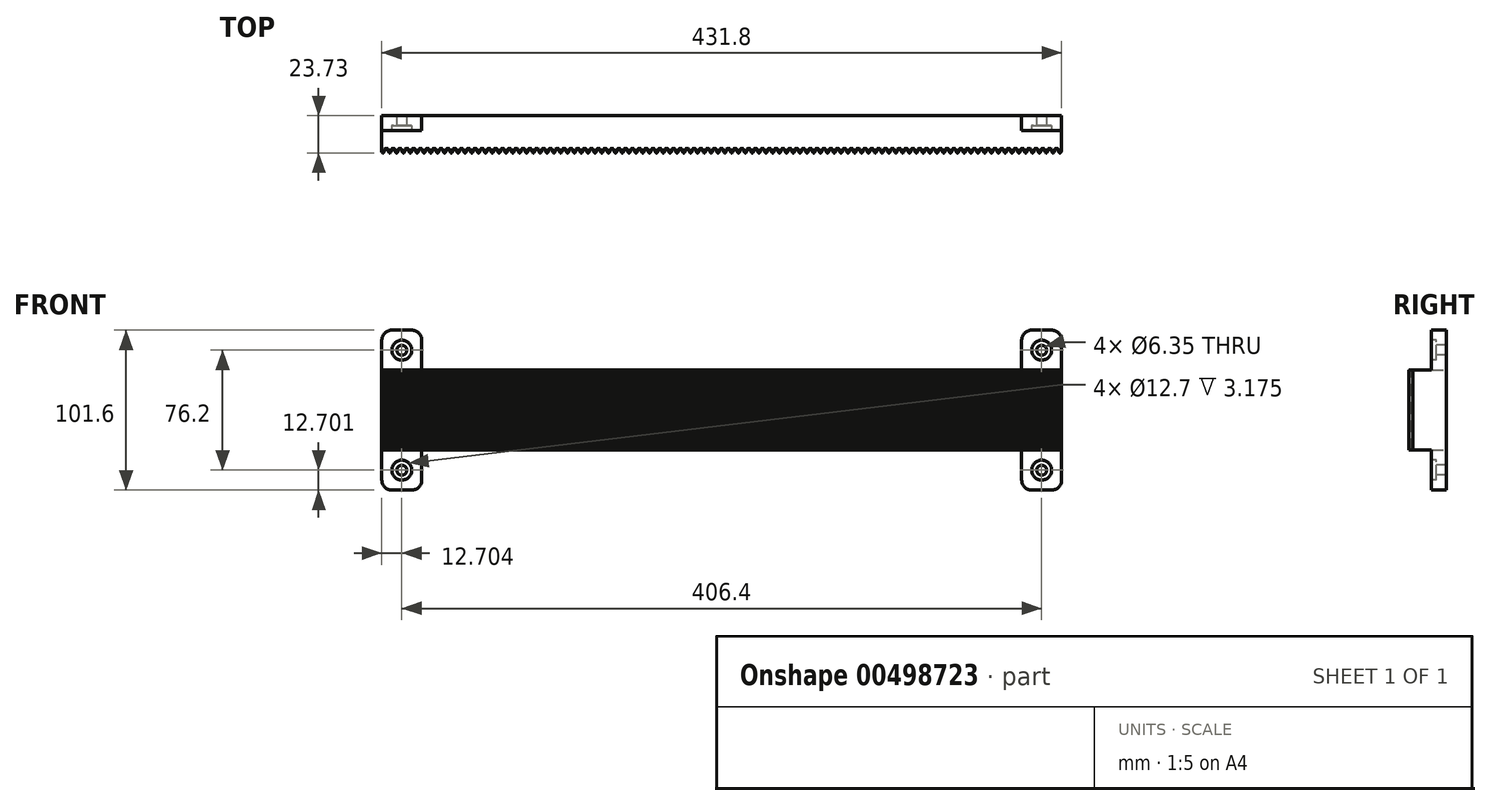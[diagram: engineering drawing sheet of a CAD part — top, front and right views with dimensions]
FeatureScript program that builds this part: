
annotation { "Feature Type Name" : "Feature", "Feature Type Description" : "" }
export const myFeature = defineFeature(function(context is Context, id is Id, definition is map)
    precondition{}
    {
        {
            var Q0;
            Q0=qCreatedBy(makeId("Front.planeOp"),FACE);
            var sketch = newSketch(context, id + "F0", { "sketchPlane" : qUnion([Q0])});
            skLineSegment(sketch, "E0.bottom", {"start": v(-70.87, -34.72) * mm, "end": v(360.93, -34.72) * mm});
            skLineSegment(sketch, "E0.top", {"start": v(-70.87, 16.08) * mm, "end": v(360.93, 16.08) * mm});
            skLineSegment(sketch, "E0.left", {"start": v(-70.87, -34.72) * mm, "end": v(-70.87, 16.08) * mm});
            skLineSegment(sketch, "E0.right", {"start": v(360.93, -34.72) * mm, "end": v(360.93, 16.08) * mm});
            skLineSegment(sketch, "E1", {"start": v(-70.87, 16.08) * mm, "end": v(-70.87, 35.13) * mm});
            skLineSegment(sketch, "E2", {"start": v(-64.52, 41.48) * mm, "end": v(-51.82, 41.48) * mm});
            skLineSegment(sketch, "E3", {"start": v(-45.47, 35.13) * mm, "end": v(-45.47, 16.08) * mm});
            skLineSegment(sketch, "E4", {"start": v(-70.87, -34.72) * mm, "end": v(-70.87, -53.77) * mm});
            skLineSegment(sketch, "E5", {"start": v(-64.52, -60.12) * mm, "end": v(-51.82, -60.12) * mm});
            skLineSegment(sketch, "E6", {"start": v(-45.47, -53.77) * mm, "end": v(-45.47, -34.72) * mm});
            skLineSegment(sketch, "E7", {"start": v(360.93, 16.08) * mm, "end": v(360.93, 35.13) * mm});
            skLineSegment(sketch, "E8", {"start": v(354.58, 41.48) * mm, "end": v(341.88, 41.48) * mm});
            skLineSegment(sketch, "E9", {"start": v(335.53, 35.13) * mm, "end": v(335.53, 16.08) * mm});
            skLineSegment(sketch, "E10", {"start": v(360.93, -34.72) * mm, "end": v(360.93, -53.77) * mm});
            skLineSegment(sketch, "E11", {"start": v(354.58, -60.12) * mm, "end": v(341.88, -60.12) * mm});
            skLineSegment(sketch, "E12", {"start": v(335.53, -53.77) * mm, "end": v(335.53, -34.72) * mm});
            skPoint(sketch, "E13.visualSharp", {"position": v(-70.87, 41.48) * mm});
            skArc(sketch, "E13.filletArc", {"start": v(-64.52, 41.48) * mm, "mid": v(-69, 39.62) * mm, "end": v(-70.87, 35.13) * mm});
            skPoint(sketch, "E14.visualSharp", {"position": v(-45.47, 41.48) * mm});
            skArc(sketch, "E14.filletArc", {"start": v(-45.47, 35.13) * mm, "mid": v(-47.33, 39.62) * mm, "end": v(-51.82, 41.48) * mm});
            skPoint(sketch, "E15.visualSharp", {"position": v(-45.47, -60.12) * mm});
            skArc(sketch, "E15.filletArc", {"start": v(-51.82, -60.12) * mm, "mid": v(-47.33, -58.26) * mm, "end": v(-45.47, -53.77) * mm});
            skPoint(sketch, "E16.visualSharp", {"position": v(360.93, -60.12) * mm});
            skArc(sketch, "E16.filletArc", {"start": v(354.58, -60.12) * mm, "mid": v(359.07, -58.26) * mm, "end": v(360.93, -53.77) * mm});
            skPoint(sketch, "E17.visualSharp", {"position": v(360.93, 41.48) * mm});
            skArc(sketch, "E17.filletArc", {"start": v(360.93, 35.13) * mm, "mid": v(359.07, 39.62) * mm, "end": v(354.58, 41.48) * mm});
            skPoint(sketch, "E18.visualSharp", {"position": v(335.53, 41.48) * mm});
            skArc(sketch, "E18.filletArc", {"start": v(341.88, 41.48) * mm, "mid": v(337.4, 39.62) * mm, "end": v(335.53, 35.13) * mm});
            skPoint(sketch, "E19.visualSharp", {"position": v(335.53, -60.12) * mm});
            skArc(sketch, "E19.filletArc", {"start": v(335.53, -53.77) * mm, "mid": v(337.4, -58.26) * mm, "end": v(341.88, -60.12) * mm});
            skPoint(sketch, "E20.visualSharp", {"position": v(-70.87, -60.12) * mm});
            skArc(sketch, "E20.filletArc", {"start": v(-70.87, -53.77) * mm, "mid": v(-69, -58.26) * mm, "end": v(-64.52, -60.12) * mm});
            skSolve(sketch);
        }
        {
            var Q0;
            {var subQ1=sQuery(id+"F0.wireOp",EDGE,"E4");Q0=makeQuery(id+"F0.imprint","IMPRINT",FACE,{"disambiguationData":[TD([[makeQuery(id+"F0.imprint","IMPRINT",EDGE,{"derivedFrom":subQ1}),1.0]])]});}
            var Q1;
            {var subQ1=sQuery(id+"F0.wireOp",EDGE,"E10");Q1=makeQuery(id+"F0.imprint","IMPRINT",FACE,{"disambiguationData":[TD([[makeQuery(id+"F0.imprint","IMPRINT",EDGE,{"derivedFrom":subQ1}),-1.0]])]});}
            var Q2;
            {var subQ1=sQuery(id+"F0.wireOp",EDGE,"E1");Q2=makeQuery(id+"F0.imprint","IMPRINT",FACE,{"disambiguationData":[TD([[makeQuery(id+"F0.imprint","IMPRINT",EDGE,{"derivedFrom":subQ1}),-1.0]])]});}
            var Q3;
            {var subQ1=sQuery(id+"F0.wireOp",EDGE,"E7");Q3=makeQuery(id+"F0.imprint","IMPRINT",FACE,{"disambiguationData":[TD([[makeQuery(id+"F0.imprint","IMPRINT",EDGE,{"derivedFrom":subQ1}),1.0]])]});}
            var Q4;
            {var subQ0=sQuery(id+"F0.wireOp",EDGE,"E0.left");Q4=makeQuery(id+"F0.imprint","IMPRINT",FACE,{"disambiguationData":[TD([[makeQuery(id+"F0.imprint","IMPRINT",EDGE,{"derivedFrom":subQ0}),-1.0]])]});}
            extrude(context, id + "F1", {"entities" : qUnion([Q0, Q1, Q2, Q3, Q4]), "depth" : 9.52 * mm});
        }
        {
            var Q0;
            Q0=makeQuery(id+"F1.opExtrude","CAP_FACE",FACE,{"disambiguationData":[OSD([sQuery(id+"F0.wireOp",EDGE,"E0.bottom"),sQuery(id+"F0.wireOp",EDGE,"E0.top"),sQuery(id+"F0.wireOp",EDGE,"E0.left"),sQuery(id+"F0.wireOp",EDGE,"E0.right"),sQuery(id+"F0.wireOp",EDGE,"E1"),sQuery(id+"F0.wireOp",EDGE,"E2"),sQuery(id+"F0.wireOp",EDGE,"E3"),sQuery(id+"F0.wireOp",EDGE,"E4"),sQuery(id+"F0.wireOp",EDGE,"E5"),sQuery(id+"F0.wireOp",EDGE,"E6"),sQuery(id+"F0.wireOp",EDGE,"E7"),sQuery(id+"F0.wireOp",EDGE,"E8"),sQuery(id+"F0.wireOp",EDGE,"E9"),sQuery(id+"F0.wireOp",EDGE,"E10"),sQuery(id+"F0.wireOp",EDGE,"E11"),sQuery(id+"F0.wireOp",EDGE,"E12"),sQuery(id+"F0.wireOp",EDGE,"E13.filletArc"),sQuery(id+"F0.wireOp",EDGE,"E14.filletArc"),sQuery(id+"F0.wireOp",EDGE,"E15.filletArc"),sQuery(id+"F0.wireOp",EDGE,"E16.filletArc"),sQuery(id+"F0.wireOp",EDGE,"E17.filletArc"),sQuery(id+"F0.wireOp",EDGE,"E18.filletArc"),sQuery(id+"F0.wireOp",EDGE,"E19.filletArc"),sQuery(id+"F0.wireOp",EDGE,"E20.filletArc")])],"isStart":false});
            var sketch = newSketch(context, id + "F2", { "sketchPlane" : qUnion([Q0])});
            skLineSegment(sketch, "E21", {"start": v(-45.47, -34.72) * mm, "end": v(-70.87, -34.72) * mm});
            skLineSegment(sketch, "E22", {"start": v(-45.47, 16.08) * mm, "end": v(-70.87, 16.08) * mm});
            skLineSegment(sketch, "E23", {"start": v(335.53, 16.08) * mm, "end": v(360.93, 16.08) * mm});
            skLineSegment(sketch, "E24", {"start": v(335.53, -34.72) * mm, "end": v(360.93, -34.72) * mm});
            skCircle(sketch, "E25", {"center": v(-58.17, 28.78) * mm, "radius": 6.35 * mm});
            skCircle(sketch, "E26", {"center": v(-58.17, -47.42) * mm, "radius": 6.35 * mm});
            skCircle(sketch, "E27", {"center": v(348.23, 28.78) * mm, "radius": 6.35 * mm});
            skCircle(sketch, "E28", {"center": v(348.23, -47.42) * mm, "radius": 6.35 * mm});
            skSolve(sketch);
        }
        {
            var Q0;
            Q0=sQuery(id+"F2.wireOp",VERTEX,"E25.center");
            var Q1;
            Q1=sQuery(id+"F2.wireOp",VERTEX,"E26.center");
            var Q2;
            Q2=sQuery(id+"F2.wireOp",VERTEX,"E27.center");
            var Q3;
            Q3=sQuery(id+"F2.wireOp",VERTEX,"E28.center");
            var Q4;
            Q4=makeQuery(id+"F1.opExtrude","SWEPT_BODY",BODY,{"disambiguationData":[OSD([sQuery(id+"F0.wireOp",EDGE,"E0.bottom"),sQuery(id+"F0.wireOp",EDGE,"E0.top"),sQuery(id+"F0.wireOp",EDGE,"E0.left"),sQuery(id+"F0.wireOp",EDGE,"E0.right"),sQuery(id+"F0.wireOp",EDGE,"E1"),sQuery(id+"F0.wireOp",EDGE,"E2"),sQuery(id+"F0.wireOp",EDGE,"E3"),sQuery(id+"F0.wireOp",EDGE,"E4"),sQuery(id+"F0.wireOp",EDGE,"E5"),sQuery(id+"F0.wireOp",EDGE,"E6"),sQuery(id+"F0.wireOp",EDGE,"E7"),sQuery(id+"F0.wireOp",EDGE,"E8"),sQuery(id+"F0.wireOp",EDGE,"E9"),sQuery(id+"F0.wireOp",EDGE,"E10"),sQuery(id+"F0.wireOp",EDGE,"E11"),sQuery(id+"F0.wireOp",EDGE,"E12"),sQuery(id+"F0.wireOp",EDGE,"E13.filletArc"),sQuery(id+"F0.wireOp",EDGE,"E14.filletArc"),sQuery(id+"F0.wireOp",EDGE,"E15.filletArc"),sQuery(id+"F0.wireOp",EDGE,"E16.filletArc"),sQuery(id+"F0.wireOp",EDGE,"E17.filletArc"),sQuery(id+"F0.wireOp",EDGE,"E18.filletArc"),sQuery(id+"F0.wireOp",EDGE,"E19.filletArc"),sQuery(id+"F0.wireOp",EDGE,"E20.filletArc")])]});
            hole(context, id + "F3", {"style" : HoleStyle.C_BORE, "endStyle" : HoleEndStyle.BLIND, "holeDiameter" : 6.35 * mm, "cBoreDiameter" : 12.7 * mm, "cBoreDepth" : 3.17 * mm, "holeDepth" : 76.2 * mm, "tappedDepth" : 12.7 * mm, "tapClearance" : 3, "startFromSketch" : true, "locations" : qUnion([Q0, Q1, Q2, Q3]), "scope" : qUnion([Q4])});
        }
        {
            var Q0;
            {var subQ3=sQuery(id+"F2.wireOp",EDGE,"E21");Q0=makeQuery(id+"F2.imprint","IMPRINT",FACE,{"disambiguationData":[TD([[makeQuery(id+"F2.imprint","IMPRINT",EDGE,{"derivedFrom":subQ3}),-1.0]])]});}
            extrude(context, id + "F4", {"entities" : qUnion([Q0]), "operationType" : NewBodyOperationType.ADD, "depth" : 11.2 * mm});
        }
        {
            var Q0;
            {var subQ0=sQuery(id+"F0.wireOp",EDGE,"E0.top");Q0=makeQuery(id+"F4.boolean.opBoolean","MERGE",FACE,{"derivedFrom":[makeQuery(id+"F1.opExtrude","SWEPT_FACE",FACE,{"disambiguationData":[OSD([subQ0])]}),makeQuery(id+"F4.opExtrude","SWEPT_FACE",FACE,{"disambiguationData":[OSD([subQ0,sQuery(id+"F2.wireOp",EDGE,"E22"),sQuery(id+"F2.wireOp",EDGE,"E23")])]})]});}
            var sketch = newSketch(context, id + "F5", { "sketchPlane" : qUnion([Q0])});
            skArc(sketch, "E29.trimOffspring", {"start": v(358.88, -22.45) * mm, "mid": v(359.12, -22.98) * mm, "end": v(359.4, -23.48) * mm});
            skLineSegment(sketch, "E30", {"start": v(359.83, -23.72) * mm, "end": v(359.84, -23.73) * mm});
            skLineSegment(sketch, "E31", {"start": v(358.77, -21.8) * mm, "end": v(358.78, -21.55) * mm});
            skLineSegment(sketch, "E32.MirrorCS", {"start": v(359.84, -23.73) * mm, "end": v(359.83, -23.72) * mm});
            skArc(sketch, "E33.MirrorCS", {"start": v(360.8, -22.45) * mm, "mid": v(360.56, -22.98) * mm, "end": v(360.28, -23.48) * mm});
            skLineSegment(sketch, "E34.MirrorCS", {"start": v(360.9, -21.8) * mm, "end": v(360.9, -21.55) * mm});
            skPoint(sketch, "E35.orphan", {"position": v(358.82, -20.63) * mm});
            skPoint(sketch, "E36.visualSharp", {"position": v(360.12, -23.73) * mm});
            skArc(sketch, "E36.filletArc", {"start": v(359.84, -23.73) * mm, "mid": v(360.1, -23.66) * mm, "end": v(360.28, -23.48) * mm});
            skPoint(sketch, "E37.visualSharp", {"position": v(359.55, -23.72) * mm});
            skArc(sketch, "E37.filletArc", {"start": v(359.4, -23.48) * mm, "mid": v(359.58, -23.66) * mm, "end": v(359.83, -23.72) * mm});
            skPoint(sketch, "E38.visualSharp", {"position": v(358.76, -22.11) * mm});
            skArc(sketch, "E38.filletArc", {"start": v(358.77, -21.8) * mm, "mid": v(358.8, -22.13) * mm, "end": v(358.88, -22.45) * mm});
            skPoint(sketch, "E39.visualSharp", {"position": v(360.92, -22.11) * mm});
            skArc(sketch, "E39.filletArc", {"start": v(360.8, -22.45) * mm, "mid": v(360.88, -22.13) * mm, "end": v(360.9, -21.8) * mm});
            skPoint(sketch, "E40.orphan", {"position": v(359.93, -23.73) * mm});
            skArc(sketch, "E41.filletArc", {"start": v(358.78, -21.55) * mm, "mid": v(358.57, -20.97) * mm, "end": v(358, -20.73) * mm});
            skArc(sketch, "E42.filletArc", {"start": v(360.93, -21.26) * mm, "mid": v(360.9, -21.4) * mm, "end": v(360.9, -21.55) * mm});
            skArc(sketch, "E43.1.0.0", {"start": v(354.54, -22.45) * mm, "mid": v(354.78, -22.98) * mm, "end": v(355.06, -23.48) * mm});
            skPoint(sketch, "E43.1.0.1", {"position": v(354.48, -20.63) * mm});
            skLineSegment(sketch, "E43.1.0.2", {"start": v(354.43, -21.8) * mm, "end": v(354.44, -21.55) * mm});
            skPoint(sketch, "E43.1.0.3", {"position": v(356.57, -22.11) * mm});
            skPoint(sketch, "E43.1.0.4", {"position": v(355.78, -23.73) * mm});
            skArc(sketch, "E43.1.0.5", {"start": v(356.45, -22.45) * mm, "mid": v(356.21, -22.98) * mm, "end": v(355.94, -23.48) * mm});
            skPoint(sketch, "E43.1.0.6", {"position": v(354.42, -22.11) * mm});
            skLineSegment(sketch, "E43.1.0.7", {"start": v(356.56, -21.8) * mm, "end": v(356.55, -21.55) * mm});
            skPoint(sketch, "E43.1.0.8", {"position": v(355.21, -23.72) * mm});
            skArc(sketch, "E43.1.0.9", {"start": v(354.44, -21.55) * mm, "mid": v(354.22, -20.97) * mm, "end": v(353.65, -20.73) * mm});
            skLineSegment(sketch, "E43.1.0.10", {"start": v(357.34, -20.73) * mm, "end": v(356.6, -20.73) * mm});
            skArc(sketch, "E43.1.0.11", {"start": v(356.45, -22.45) * mm, "mid": v(356.54, -22.13) * mm, "end": v(356.56, -21.8) * mm});
            skArc(sketch, "E43.1.0.12", {"start": v(354.43, -21.8) * mm, "mid": v(354.45, -22.13) * mm, "end": v(354.54, -22.45) * mm});
            skPoint(sketch, "E43.1.0.13", {"position": v(355.59, -23.73) * mm});
            skArc(sketch, "E43.1.0.14", {"start": v(355.06, -23.48) * mm, "mid": v(355.24, -23.66) * mm, "end": v(355.48, -23.72) * mm});
            skArc(sketch, "E43.1.0.15", {"start": v(357.34, -20.73) * mm, "mid": v(356.77, -20.97) * mm, "end": v(356.55, -21.55) * mm});
            skArc(sketch, "E43.1.0.16", {"start": v(355.5, -23.73) * mm, "mid": v(355.75, -23.66) * mm, "end": v(355.94, -23.48) * mm});
            skLineSegment(sketch, "E43.1.0.17", {"start": v(355.5, -23.73) * mm, "end": v(355.48, -23.72) * mm});
            skLineSegment(sketch, "E43.1.0.18", {"start": v(355.48, -23.72) * mm, "end": v(355.5, -23.73) * mm});
            skArc(sketch, "E43.2.0.0", {"start": v(350.2, -22.45) * mm, "mid": v(350.43, -22.98) * mm, "end": v(350.71, -23.48) * mm});
            skPoint(sketch, "E43.2.0.1", {"position": v(350.14, -20.63) * mm});
            skLineSegment(sketch, "E43.2.0.2", {"start": v(350.09, -21.8) * mm, "end": v(350.1, -21.55) * mm});
            skPoint(sketch, "E43.2.0.3", {"position": v(352.23, -22.11) * mm});
            skPoint(sketch, "E43.2.0.4", {"position": v(351.43, -23.73) * mm});
            skArc(sketch, "E43.2.0.5", {"start": v(352.1, -22.45) * mm, "mid": v(351.87, -22.98) * mm, "end": v(351.6, -23.48) * mm});
            skPoint(sketch, "E43.2.0.6", {"position": v(350.07, -22.11) * mm});
            skLineSegment(sketch, "E43.2.0.7", {"start": v(352.22, -21.8) * mm, "end": v(352.2, -21.55) * mm});
            skPoint(sketch, "E43.2.0.8", {"position": v(350.87, -23.72) * mm});
            skArc(sketch, "E43.2.0.9", {"start": v(350.1, -21.55) * mm, "mid": v(349.88, -20.97) * mm, "end": v(349.31, -20.73) * mm});
            skLineSegment(sketch, "E43.2.0.10", {"start": v(353, -20.73) * mm, "end": v(352.25, -20.73) * mm});
            skArc(sketch, "E43.2.0.11", {"start": v(352.1, -22.45) * mm, "mid": v(352.2, -22.13) * mm, "end": v(352.22, -21.8) * mm});
            skArc(sketch, "E43.2.0.12", {"start": v(350.09, -21.8) * mm, "mid": v(350.1, -22.13) * mm, "end": v(350.2, -22.45) * mm});
            skPoint(sketch, "E43.2.0.13", {"position": v(351.24, -23.73) * mm});
            skArc(sketch, "E43.2.0.14", {"start": v(350.71, -23.48) * mm, "mid": v(350.9, -23.66) * mm, "end": v(351.14, -23.72) * mm});
            skArc(sketch, "E43.2.0.15", {"start": v(353, -20.73) * mm, "mid": v(352.42, -20.97) * mm, "end": v(352.2, -21.55) * mm});
            skArc(sketch, "E43.2.0.16", {"start": v(351.15, -23.73) * mm, "mid": v(351.4, -23.66) * mm, "end": v(351.6, -23.48) * mm});
            skLineSegment(sketch, "E43.2.0.17", {"start": v(351.15, -23.73) * mm, "end": v(351.14, -23.72) * mm});
            skLineSegment(sketch, "E43.2.0.18", {"start": v(351.14, -23.72) * mm, "end": v(351.15, -23.73) * mm});
            skArc(sketch, "E43.3.0.0", {"start": v(345.85, -22.45) * mm, "mid": v(346.1, -22.98) * mm, "end": v(346.37, -23.48) * mm});
            skPoint(sketch, "E43.3.0.1", {"position": v(345.8, -20.63) * mm});
            skLineSegment(sketch, "E43.3.0.2", {"start": v(345.74, -21.8) * mm, "end": v(345.75, -21.55) * mm});
            skPoint(sketch, "E43.3.0.3", {"position": v(347.89, -22.11) * mm});
            skPoint(sketch, "E43.3.0.4", {"position": v(347.1, -23.73) * mm});
            skArc(sketch, "E43.3.0.5", {"start": v(347.76, -22.45) * mm, "mid": v(347.53, -22.98) * mm, "end": v(347.25, -23.48) * mm});
            skPoint(sketch, "E43.3.0.6", {"position": v(345.73, -22.11) * mm});
            skLineSegment(sketch, "E43.3.0.7", {"start": v(347.87, -21.8) * mm, "end": v(347.86, -21.55) * mm});
            skPoint(sketch, "E43.3.0.8", {"position": v(346.52, -23.72) * mm});
            skArc(sketch, "E43.3.0.9", {"start": v(345.75, -21.55) * mm, "mid": v(345.54, -20.97) * mm, "end": v(344.97, -20.73) * mm});
            skLineSegment(sketch, "E43.3.0.10", {"start": v(348.65, -20.73) * mm, "end": v(347.9, -20.73) * mm});
            skArc(sketch, "E43.3.0.11", {"start": v(347.76, -22.45) * mm, "mid": v(347.85, -22.13) * mm, "end": v(347.87, -21.8) * mm});
            skArc(sketch, "E43.3.0.12", {"start": v(345.74, -21.8) * mm, "mid": v(345.76, -22.13) * mm, "end": v(345.85, -22.45) * mm});
            skPoint(sketch, "E43.3.0.13", {"position": v(346.9, -23.73) * mm});
            skArc(sketch, "E43.3.0.14", {"start": v(346.37, -23.48) * mm, "mid": v(346.55, -23.66) * mm, "end": v(346.8, -23.72) * mm});
            skArc(sketch, "E43.3.0.15", {"start": v(348.65, -20.73) * mm, "mid": v(348.08, -20.97) * mm, "end": v(347.86, -21.55) * mm});
            skArc(sketch, "E43.3.0.16", {"start": v(346.8, -23.73) * mm, "mid": v(347.06, -23.66) * mm, "end": v(347.25, -23.48) * mm});
            skLineSegment(sketch, "E43.3.0.17", {"start": v(346.8, -23.73) * mm, "end": v(346.8, -23.72) * mm});
            skLineSegment(sketch, "E43.3.0.18", {"start": v(346.8, -23.72) * mm, "end": v(346.8, -23.73) * mm});
            skArc(sketch, "E43.4.0.0", {"start": v(341.51, -22.45) * mm, "mid": v(341.75, -22.98) * mm, "end": v(342.03, -23.48) * mm});
            skPoint(sketch, "E43.4.0.1", {"position": v(341.45, -20.63) * mm});
            skLineSegment(sketch, "E43.4.0.2", {"start": v(341.4, -21.8) * mm, "end": v(341.41, -21.55) * mm});
            skPoint(sketch, "E43.4.0.3", {"position": v(343.54, -22.11) * mm});
            skPoint(sketch, "E43.4.0.4", {"position": v(342.75, -23.73) * mm});
            skArc(sketch, "E43.4.0.5", {"start": v(343.42, -22.45) * mm, "mid": v(343.18, -22.98) * mm, "end": v(342.9, -23.48) * mm});
            skPoint(sketch, "E43.4.0.6", {"position": v(341.39, -22.11) * mm});
            skLineSegment(sketch, "E43.4.0.7", {"start": v(343.53, -21.8) * mm, "end": v(343.52, -21.55) * mm});
            skPoint(sketch, "E43.4.0.8", {"position": v(342.18, -23.72) * mm});
            skArc(sketch, "E43.4.0.9", {"start": v(341.41, -21.55) * mm, "mid": v(341.2, -20.97) * mm, "end": v(340.62, -20.73) * mm});
            skLineSegment(sketch, "E43.4.0.10", {"start": v(344.3, -20.73) * mm, "end": v(343.56, -20.73) * mm});
            skArc(sketch, "E43.4.0.11", {"start": v(343.42, -22.45) * mm, "mid": v(343.51, -22.13) * mm, "end": v(343.53, -21.8) * mm});
            skArc(sketch, "E43.4.0.12", {"start": v(341.4, -21.8) * mm, "mid": v(341.42, -22.13) * mm, "end": v(341.51, -22.45) * mm});
            skPoint(sketch, "E43.4.0.13", {"position": v(342.56, -23.73) * mm});
            skArc(sketch, "E43.4.0.14", {"start": v(342.03, -23.48) * mm, "mid": v(342.2, -23.66) * mm, "end": v(342.45, -23.72) * mm});
            skArc(sketch, "E43.4.0.15", {"start": v(344.3, -20.73) * mm, "mid": v(343.74, -20.97) * mm, "end": v(343.52, -21.55) * mm});
            skArc(sketch, "E43.4.0.16", {"start": v(342.47, -23.73) * mm, "mid": v(342.72, -23.66) * mm, "end": v(342.9, -23.48) * mm});
            skLineSegment(sketch, "E43.4.0.17", {"start": v(342.47, -23.73) * mm, "end": v(342.45, -23.72) * mm});
            skLineSegment(sketch, "E43.4.0.18", {"start": v(342.45, -23.72) * mm, "end": v(342.47, -23.73) * mm});
            skArc(sketch, "E43.5.0.0", {"start": v(337.17, -22.45) * mm, "mid": v(337.4, -22.98) * mm, "end": v(337.68, -23.48) * mm});
            skPoint(sketch, "E43.5.0.1", {"position": v(337.1, -20.63) * mm});
            skLineSegment(sketch, "E43.5.0.2", {"start": v(337.06, -21.8) * mm, "end": v(337.07, -21.55) * mm});
            skPoint(sketch, "E43.5.0.3", {"position": v(339.2, -22.11) * mm});
            skPoint(sketch, "E43.5.0.4", {"position": v(338.4, -23.73) * mm});
            skArc(sketch, "E43.5.0.5", {"start": v(339.08, -22.45) * mm, "mid": v(338.84, -22.98) * mm, "end": v(338.56, -23.48) * mm});
            skPoint(sketch, "E43.5.0.6", {"position": v(337.04, -22.11) * mm});
            skLineSegment(sketch, "E43.5.0.7", {"start": v(339.19, -21.8) * mm, "end": v(339.18, -21.55) * mm});
            skPoint(sketch, "E43.5.0.8", {"position": v(337.84, -23.72) * mm});
            skArc(sketch, "E43.5.0.9", {"start": v(337.07, -21.55) * mm, "mid": v(336.85, -20.97) * mm, "end": v(336.28, -20.73) * mm});
            skLineSegment(sketch, "E43.5.0.10", {"start": v(339.96, -20.73) * mm, "end": v(339.22, -20.73) * mm});
            skArc(sketch, "E43.5.0.11", {"start": v(339.08, -22.45) * mm, "mid": v(339.17, -22.13) * mm, "end": v(339.19, -21.8) * mm});
            skArc(sketch, "E43.5.0.12", {"start": v(337.06, -21.8) * mm, "mid": v(337.08, -22.13) * mm, "end": v(337.17, -22.45) * mm});
            skPoint(sketch, "E43.5.0.13", {"position": v(338.21, -23.73) * mm});
            skArc(sketch, "E43.5.0.14", {"start": v(337.68, -23.48) * mm, "mid": v(337.87, -23.66) * mm, "end": v(338.1, -23.72) * mm});
            skArc(sketch, "E43.5.0.15", {"start": v(339.96, -20.73) * mm, "mid": v(339.4, -20.97) * mm, "end": v(339.18, -21.55) * mm});
            skArc(sketch, "E43.5.0.16", {"start": v(338.12, -23.73) * mm, "mid": v(338.37, -23.66) * mm, "end": v(338.56, -23.48) * mm});
            skLineSegment(sketch, "E43.5.0.17", {"start": v(338.12, -23.73) * mm, "end": v(338.1, -23.72) * mm});
            skLineSegment(sketch, "E43.5.0.18", {"start": v(338.1, -23.72) * mm, "end": v(338.12, -23.73) * mm});
            skArc(sketch, "E43.6.0.0", {"start": v(332.82, -22.45) * mm, "mid": v(333.06, -22.98) * mm, "end": v(333.34, -23.48) * mm});
            skPoint(sketch, "E43.6.0.1", {"position": v(332.76, -20.63) * mm});
            skLineSegment(sketch, "E43.6.0.2", {"start": v(332.71, -21.8) * mm, "end": v(332.72, -21.55) * mm});
            skPoint(sketch, "E43.6.0.3", {"position": v(334.86, -22.11) * mm});
            skPoint(sketch, "E43.6.0.4", {"position": v(334.06, -23.73) * mm});
            skArc(sketch, "E43.6.0.5", {"start": v(334.73, -22.45) * mm, "mid": v(334.5, -22.98) * mm, "end": v(334.22, -23.48) * mm});
            skPoint(sketch, "E43.6.0.6", {"position": v(332.7, -22.11) * mm});
            skLineSegment(sketch, "E43.6.0.7", {"start": v(334.84, -21.8) * mm, "end": v(334.83, -21.55) * mm});
            skPoint(sketch, "E43.6.0.8", {"position": v(333.5, -23.72) * mm});
            skArc(sketch, "E43.6.0.9", {"start": v(332.72, -21.55) * mm, "mid": v(332.5, -20.97) * mm, "end": v(331.94, -20.73) * mm});
            skLineSegment(sketch, "E43.6.0.10", {"start": v(335.62, -20.73) * mm, "end": v(334.87, -20.73) * mm});
            skArc(sketch, "E43.6.0.11", {"start": v(334.73, -22.45) * mm, "mid": v(334.82, -22.13) * mm, "end": v(334.84, -21.8) * mm});
            skArc(sketch, "E43.6.0.12", {"start": v(332.71, -21.8) * mm, "mid": v(332.73, -22.13) * mm, "end": v(332.82, -22.45) * mm});
            skPoint(sketch, "E43.6.0.13", {"position": v(333.87, -23.73) * mm});
            skArc(sketch, "E43.6.0.14", {"start": v(333.34, -23.48) * mm, "mid": v(333.52, -23.66) * mm, "end": v(333.77, -23.72) * mm});
            skArc(sketch, "E43.6.0.15", {"start": v(335.62, -20.73) * mm, "mid": v(335.05, -20.97) * mm, "end": v(334.83, -21.55) * mm});
            skArc(sketch, "E43.6.0.16", {"start": v(333.78, -23.73) * mm, "mid": v(334.03, -23.66) * mm, "end": v(334.22, -23.48) * mm});
            skLineSegment(sketch, "E43.6.0.17", {"start": v(333.78, -23.73) * mm, "end": v(333.77, -23.72) * mm});
            skLineSegment(sketch, "E43.6.0.18", {"start": v(333.77, -23.72) * mm, "end": v(333.78, -23.73) * mm});
            skArc(sketch, "E43.7.0.0", {"start": v(328.48, -22.45) * mm, "mid": v(328.72, -22.98) * mm, "end": v(329, -23.48) * mm});
            skPoint(sketch, "E43.7.0.1", {"position": v(328.42, -20.63) * mm});
            skLineSegment(sketch, "E43.7.0.2", {"start": v(328.37, -21.8) * mm, "end": v(328.38, -21.55) * mm});
            skPoint(sketch, "E43.7.0.3", {"position": v(330.51, -22.11) * mm});
            skPoint(sketch, "E43.7.0.4", {"position": v(329.72, -23.73) * mm});
            skArc(sketch, "E43.7.0.5", {"start": v(330.39, -22.45) * mm, "mid": v(330.15, -22.98) * mm, "end": v(329.87, -23.48) * mm});
            skPoint(sketch, "E43.7.0.6", {"position": v(328.36, -22.11) * mm});
            skLineSegment(sketch, "E43.7.0.7", {"start": v(330.5, -21.8) * mm, "end": v(330.49, -21.55) * mm});
            skPoint(sketch, "E43.7.0.8", {"position": v(329.15, -23.72) * mm});
            skArc(sketch, "E43.7.0.9", {"start": v(328.38, -21.55) * mm, "mid": v(328.16, -20.97) * mm, "end": v(327.6, -20.73) * mm});
            skLineSegment(sketch, "E43.7.0.10", {"start": v(331.28, -20.73) * mm, "end": v(330.53, -20.73) * mm});
            skArc(sketch, "E43.7.0.11", {"start": v(330.39, -22.45) * mm, "mid": v(330.48, -22.13) * mm, "end": v(330.5, -21.8) * mm});
            skArc(sketch, "E43.7.0.12", {"start": v(328.37, -21.8) * mm, "mid": v(328.4, -22.13) * mm, "end": v(328.48, -22.45) * mm});
            skPoint(sketch, "E43.7.0.13", {"position": v(329.53, -23.73) * mm});
            skArc(sketch, "E43.7.0.14", {"start": v(329, -23.48) * mm, "mid": v(329.18, -23.66) * mm, "end": v(329.42, -23.72) * mm});
            skArc(sketch, "E43.7.0.15", {"start": v(331.28, -20.73) * mm, "mid": v(330.7, -20.97) * mm, "end": v(330.49, -21.55) * mm});
            skArc(sketch, "E43.7.0.16", {"start": v(329.44, -23.73) * mm, "mid": v(329.69, -23.66) * mm, "end": v(329.87, -23.48) * mm});
            skLineSegment(sketch, "E43.7.0.17", {"start": v(329.44, -23.73) * mm, "end": v(329.42, -23.72) * mm});
            skLineSegment(sketch, "E43.7.0.18", {"start": v(329.42, -23.72) * mm, "end": v(329.44, -23.73) * mm});
            skArc(sketch, "E43.8.0.0", {"start": v(324.14, -22.45) * mm, "mid": v(324.37, -22.98) * mm, "end": v(324.65, -23.48) * mm});
            skPoint(sketch, "E43.8.0.1", {"position": v(324.08, -20.63) * mm});
            skLineSegment(sketch, "E43.8.0.2", {"start": v(324.03, -21.8) * mm, "end": v(324.04, -21.55) * mm});
            skPoint(sketch, "E43.8.0.3", {"position": v(326.17, -22.11) * mm});
            skPoint(sketch, "E43.8.0.4", {"position": v(325.37, -23.73) * mm});
            skArc(sketch, "E43.8.0.5", {"start": v(326.05, -22.45) * mm, "mid": v(325.81, -22.98) * mm, "end": v(325.53, -23.48) * mm});
            skPoint(sketch, "E43.8.0.6", {"position": v(324.01, -22.11) * mm});
            skLineSegment(sketch, "E43.8.0.7", {"start": v(326.16, -21.8) * mm, "end": v(326.15, -21.55) * mm});
            skPoint(sketch, "E43.8.0.8", {"position": v(324.8, -23.72) * mm});
            skArc(sketch, "E43.8.0.9", {"start": v(324.04, -21.55) * mm, "mid": v(323.82, -20.97) * mm, "end": v(323.25, -20.73) * mm});
            skLineSegment(sketch, "E43.8.0.10", {"start": v(326.93, -20.73) * mm, "end": v(326.19, -20.73) * mm});
            skArc(sketch, "E43.8.0.11", {"start": v(326.05, -22.45) * mm, "mid": v(326.14, -22.13) * mm, "end": v(326.16, -21.8) * mm});
            skArc(sketch, "E43.8.0.12", {"start": v(324.03, -21.8) * mm, "mid": v(324.05, -22.13) * mm, "end": v(324.14, -22.45) * mm});
            skPoint(sketch, "E43.8.0.13", {"position": v(325.18, -23.73) * mm});
            skArc(sketch, "E43.8.0.14", {"start": v(324.65, -23.48) * mm, "mid": v(324.84, -23.66) * mm, "end": v(325.08, -23.72) * mm});
            skArc(sketch, "E43.8.0.15", {"start": v(326.93, -20.73) * mm, "mid": v(326.36, -20.97) * mm, "end": v(326.15, -21.55) * mm});
            skArc(sketch, "E43.8.0.16", {"start": v(325.1, -23.73) * mm, "mid": v(325.34, -23.66) * mm, "end": v(325.53, -23.48) * mm});
            skLineSegment(sketch, "E43.8.0.17", {"start": v(325.1, -23.73) * mm, "end": v(325.08, -23.72) * mm});
            skLineSegment(sketch, "E43.8.0.18", {"start": v(325.08, -23.72) * mm, "end": v(325.1, -23.73) * mm});
            skArc(sketch, "E43.9.0.0", {"start": v(319.8, -22.45) * mm, "mid": v(320.03, -22.98) * mm, "end": v(320.3, -23.48) * mm});
            skPoint(sketch, "E43.9.0.1", {"position": v(319.73, -20.63) * mm});
            skLineSegment(sketch, "E43.9.0.2", {"start": v(319.68, -21.8) * mm, "end": v(319.7, -21.55) * mm});
            skPoint(sketch, "E43.9.0.3", {"position": v(321.83, -22.11) * mm});
            skPoint(sketch, "E43.9.0.4", {"position": v(321.03, -23.73) * mm});
            skArc(sketch, "E43.9.0.5", {"start": v(321.7, -22.45) * mm, "mid": v(321.47, -22.98) * mm, "end": v(321.19, -23.48) * mm});
            skPoint(sketch, "E43.9.0.6", {"position": v(319.67, -22.11) * mm});
            skLineSegment(sketch, "E43.9.0.7", {"start": v(321.81, -21.8) * mm, "end": v(321.8, -21.55) * mm});
            skPoint(sketch, "E43.9.0.8", {"position": v(320.46, -23.72) * mm});
            skArc(sketch, "E43.9.0.9", {"start": v(319.7, -21.55) * mm, "mid": v(319.47, -20.97) * mm, "end": v(318.9, -20.73) * mm});
            skLineSegment(sketch, "E43.9.0.10", {"start": v(322.59, -20.73) * mm, "end": v(321.84, -20.73) * mm});
            skArc(sketch, "E43.9.0.11", {"start": v(321.7, -22.45) * mm, "mid": v(321.8, -22.13) * mm, "end": v(321.81, -21.8) * mm});
            skArc(sketch, "E43.9.0.12", {"start": v(319.68, -21.8) * mm, "mid": v(319.7, -22.13) * mm, "end": v(319.8, -22.45) * mm});
            skPoint(sketch, "E43.9.0.13", {"position": v(320.84, -23.73) * mm});
            skArc(sketch, "E43.9.0.14", {"start": v(320.3, -23.48) * mm, "mid": v(320.5, -23.66) * mm, "end": v(320.74, -23.72) * mm});
            skArc(sketch, "E43.9.0.15", {"start": v(322.59, -20.73) * mm, "mid": v(322.02, -20.97) * mm, "end": v(321.8, -21.55) * mm});
            skArc(sketch, "E43.9.0.16", {"start": v(320.75, -23.73) * mm, "mid": v(321, -23.66) * mm, "end": v(321.19, -23.48) * mm});
            skLineSegment(sketch, "E43.9.0.17", {"start": v(320.75, -23.73) * mm, "end": v(320.74, -23.72) * mm});
            skLineSegment(sketch, "E43.9.0.18", {"start": v(320.74, -23.72) * mm, "end": v(320.75, -23.73) * mm});
            skArc(sketch, "E43.10.0.0", {"start": v(315.45, -22.45) * mm, "mid": v(315.69, -22.98) * mm, "end": v(315.97, -23.48) * mm});
            skPoint(sketch, "E43.10.0.1", {"position": v(315.39, -20.63) * mm});
            skLineSegment(sketch, "E43.10.0.2", {"start": v(315.34, -21.8) * mm, "end": v(315.35, -21.55) * mm});
            skPoint(sketch, "E43.10.0.3", {"position": v(317.48, -22.11) * mm});
            skPoint(sketch, "E43.10.0.4", {"position": v(316.69, -23.73) * mm});
            skArc(sketch, "E43.10.0.5", {"start": v(317.36, -22.45) * mm, "mid": v(317.12, -22.98) * mm, "end": v(316.84, -23.48) * mm});
            skPoint(sketch, "E43.10.0.6", {"position": v(315.33, -22.11) * mm});
            skLineSegment(sketch, "E43.10.0.7", {"start": v(317.47, -21.8) * mm, "end": v(317.46, -21.55) * mm});
            skPoint(sketch, "E43.10.0.8", {"position": v(316.12, -23.72) * mm});
            skArc(sketch, "E43.10.0.9", {"start": v(315.35, -21.55) * mm, "mid": v(315.13, -20.97) * mm, "end": v(314.56, -20.73) * mm});
            skLineSegment(sketch, "E43.10.0.10", {"start": v(318.25, -20.73) * mm, "end": v(317.5, -20.73) * mm});
            skArc(sketch, "E43.10.0.11", {"start": v(317.36, -22.45) * mm, "mid": v(317.45, -22.13) * mm, "end": v(317.47, -21.8) * mm});
            skArc(sketch, "E43.10.0.12", {"start": v(315.34, -21.8) * mm, "mid": v(315.36, -22.13) * mm, "end": v(315.45, -22.45) * mm});
            skPoint(sketch, "E43.10.0.13", {"position": v(316.5, -23.73) * mm});
            skArc(sketch, "E43.10.0.14", {"start": v(315.97, -23.48) * mm, "mid": v(316.15, -23.66) * mm, "end": v(316.4, -23.72) * mm});
            skArc(sketch, "E43.10.0.15", {"start": v(318.25, -20.73) * mm, "mid": v(317.68, -20.97) * mm, "end": v(317.46, -21.55) * mm});
            skArc(sketch, "E43.10.0.16", {"start": v(316.4, -23.73) * mm, "mid": v(316.66, -23.66) * mm, "end": v(316.84, -23.48) * mm});
            skLineSegment(sketch, "E43.10.0.17", {"start": v(316.4, -23.73) * mm, "end": v(316.4, -23.72) * mm});
            skLineSegment(sketch, "E43.10.0.18", {"start": v(316.4, -23.72) * mm, "end": v(316.4, -23.73) * mm});
            skArc(sketch, "E43.11.0.0", {"start": v(311.1, -22.45) * mm, "mid": v(311.34, -22.98) * mm, "end": v(311.62, -23.48) * mm});
            skPoint(sketch, "E43.11.0.1", {"position": v(311.05, -20.63) * mm});
            skLineSegment(sketch, "E43.11.0.2", {"start": v(311, -21.8) * mm, "end": v(311, -21.55) * mm});
            skPoint(sketch, "E43.11.0.3", {"position": v(313.14, -22.11) * mm});
            skPoint(sketch, "E43.11.0.4", {"position": v(312.34, -23.73) * mm});
            skArc(sketch, "E43.11.0.5", {"start": v(313.02, -22.45) * mm, "mid": v(312.78, -22.98) * mm, "end": v(312.5, -23.48) * mm});
            skPoint(sketch, "E43.11.0.6", {"position": v(310.98, -22.11) * mm});
            skLineSegment(sketch, "E43.11.0.7", {"start": v(313.13, -21.8) * mm, "end": v(313.12, -21.55) * mm});
            skPoint(sketch, "E43.11.0.8", {"position": v(311.78, -23.72) * mm});
            skArc(sketch, "E43.11.0.9", {"start": v(311, -21.55) * mm, "mid": v(310.79, -20.97) * mm, "end": v(310.22, -20.73) * mm});
            skLineSegment(sketch, "E43.11.0.10", {"start": v(313.9, -20.73) * mm, "end": v(313.16, -20.73) * mm});
            skArc(sketch, "E43.11.0.11", {"start": v(313.02, -22.45) * mm, "mid": v(313.1, -22.13) * mm, "end": v(313.13, -21.8) * mm});
            skArc(sketch, "E43.11.0.12", {"start": v(311, -21.8) * mm, "mid": v(311.02, -22.13) * mm, "end": v(311.1, -22.45) * mm});
            skPoint(sketch, "E43.11.0.13", {"position": v(312.15, -23.73) * mm});
            skArc(sketch, "E43.11.0.14", {"start": v(311.62, -23.48) * mm, "mid": v(311.8, -23.66) * mm, "end": v(312.05, -23.72) * mm});
            skArc(sketch, "E43.11.0.15", {"start": v(313.9, -20.73) * mm, "mid": v(313.33, -20.97) * mm, "end": v(313.12, -21.55) * mm});
            skArc(sketch, "E43.11.0.16", {"start": v(312.06, -23.73) * mm, "mid": v(312.31, -23.66) * mm, "end": v(312.5, -23.48) * mm});
            skLineSegment(sketch, "E43.11.0.17", {"start": v(312.06, -23.73) * mm, "end": v(312.05, -23.72) * mm});
            skLineSegment(sketch, "E43.11.0.18", {"start": v(312.05, -23.72) * mm, "end": v(312.06, -23.73) * mm});
            skArc(sketch, "E43.12.0.0", {"start": v(306.76, -22.45) * mm, "mid": v(307, -22.98) * mm, "end": v(307.28, -23.48) * mm});
            skPoint(sketch, "E43.12.0.1", {"position": v(306.7, -20.63) * mm});
            skLineSegment(sketch, "E43.12.0.2", {"start": v(306.65, -21.8) * mm, "end": v(306.66, -21.55) * mm});
            skPoint(sketch, "E43.12.0.3", {"position": v(308.8, -22.11) * mm});
            skPoint(sketch, "E43.12.0.4", {"position": v(308, -23.73) * mm});
            skArc(sketch, "E43.12.0.5", {"start": v(308.67, -22.45) * mm, "mid": v(308.44, -22.98) * mm, "end": v(308.16, -23.48) * mm});
            skPoint(sketch, "E43.12.0.6", {"position": v(306.64, -22.11) * mm});
            skLineSegment(sketch, "E43.12.0.7", {"start": v(308.78, -21.8) * mm, "end": v(308.77, -21.55) * mm});
            skPoint(sketch, "E43.12.0.8", {"position": v(307.43, -23.72) * mm});
            skArc(sketch, "E43.12.0.9", {"start": v(306.66, -21.55) * mm, "mid": v(306.44, -20.97) * mm, "end": v(305.88, -20.73) * mm});
            skLineSegment(sketch, "E43.12.0.10", {"start": v(309.56, -20.73) * mm, "end": v(308.81, -20.73) * mm});
            skArc(sketch, "E43.12.0.11", {"start": v(308.67, -22.45) * mm, "mid": v(308.76, -22.13) * mm, "end": v(308.78, -21.8) * mm});
            skArc(sketch, "E43.12.0.12", {"start": v(306.65, -21.8) * mm, "mid": v(306.67, -22.13) * mm, "end": v(306.76, -22.45) * mm});
            skPoint(sketch, "E43.12.0.13", {"position": v(307.8, -23.73) * mm});
            skArc(sketch, "E43.12.0.14", {"start": v(307.28, -23.48) * mm, "mid": v(307.46, -23.66) * mm, "end": v(307.7, -23.72) * mm});
            skArc(sketch, "E43.12.0.15", {"start": v(309.56, -20.73) * mm, "mid": v(309, -20.97) * mm, "end": v(308.77, -21.55) * mm});
            skArc(sketch, "E43.12.0.16", {"start": v(307.72, -23.73) * mm, "mid": v(307.97, -23.66) * mm, "end": v(308.16, -23.48) * mm});
            skLineSegment(sketch, "E43.12.0.17", {"start": v(307.72, -23.73) * mm, "end": v(307.7, -23.72) * mm});
            skLineSegment(sketch, "E43.12.0.18", {"start": v(307.7, -23.72) * mm, "end": v(307.72, -23.73) * mm});
            skArc(sketch, "E43.13.0.0", {"start": v(302.42, -22.45) * mm, "mid": v(302.66, -22.98) * mm, "end": v(302.94, -23.48) * mm});
            skPoint(sketch, "E43.13.0.1", {"position": v(302.36, -20.63) * mm});
            skLineSegment(sketch, "E43.13.0.2", {"start": v(302.3, -21.8) * mm, "end": v(302.32, -21.55) * mm});
            skPoint(sketch, "E43.13.0.3", {"position": v(304.45, -22.11) * mm});
            skPoint(sketch, "E43.13.0.4", {"position": v(303.66, -23.73) * mm});
            skArc(sketch, "E43.13.0.5", {"start": v(304.33, -22.45) * mm, "mid": v(304.1, -22.98) * mm, "end": v(303.81, -23.48) * mm});
            skPoint(sketch, "E43.13.0.6", {"position": v(302.3, -22.11) * mm});
            skLineSegment(sketch, "E43.13.0.7", {"start": v(304.44, -21.8) * mm, "end": v(304.43, -21.55) * mm});
            skPoint(sketch, "E43.13.0.8", {"position": v(303.09, -23.72) * mm});
            skArc(sketch, "E43.13.0.9", {"start": v(302.32, -21.55) * mm, "mid": v(302.1, -20.97) * mm, "end": v(301.53, -20.73) * mm});
            skLineSegment(sketch, "E43.13.0.10", {"start": v(305.22, -20.73) * mm, "end": v(304.47, -20.73) * mm});
            skArc(sketch, "E43.13.0.11", {"start": v(304.33, -22.45) * mm, "mid": v(304.42, -22.13) * mm, "end": v(304.44, -21.8) * mm});
            skArc(sketch, "E43.13.0.12", {"start": v(302.3, -21.8) * mm, "mid": v(302.33, -22.13) * mm, "end": v(302.42, -22.45) * mm});
            skPoint(sketch, "E43.13.0.13", {"position": v(303.46, -23.73) * mm});
            skArc(sketch, "E43.13.0.14", {"start": v(302.94, -23.48) * mm, "mid": v(303.12, -23.66) * mm, "end": v(303.36, -23.72) * mm});
            skArc(sketch, "E43.13.0.15", {"start": v(305.22, -20.73) * mm, "mid": v(304.65, -20.97) * mm, "end": v(304.43, -21.55) * mm});
            skArc(sketch, "E43.13.0.16", {"start": v(303.37, -23.73) * mm, "mid": v(303.63, -23.66) * mm, "end": v(303.81, -23.48) * mm});
            skLineSegment(sketch, "E43.13.0.17", {"start": v(303.37, -23.73) * mm, "end": v(303.36, -23.72) * mm});
            skLineSegment(sketch, "E43.13.0.18", {"start": v(303.36, -23.72) * mm, "end": v(303.37, -23.73) * mm});
            skArc(sketch, "E43.14.0.0", {"start": v(298.08, -22.45) * mm, "mid": v(298.31, -22.98) * mm, "end": v(298.6, -23.48) * mm});
            skPoint(sketch, "E43.14.0.1", {"position": v(298.02, -20.63) * mm});
            skLineSegment(sketch, "E43.14.0.2", {"start": v(297.97, -21.8) * mm, "end": v(297.98, -21.55) * mm});
            skPoint(sketch, "E43.14.0.3", {"position": v(300.11, -22.11) * mm});
            skPoint(sketch, "E43.14.0.4", {"position": v(299.31, -23.73) * mm});
            skArc(sketch, "E43.14.0.5", {"start": v(299.99, -22.45) * mm, "mid": v(299.75, -22.98) * mm, "end": v(299.47, -23.48) * mm});
            skPoint(sketch, "E43.14.0.6", {"position": v(297.95, -22.11) * mm});
            skLineSegment(sketch, "E43.14.0.7", {"start": v(300.1, -21.8) * mm, "end": v(300.09, -21.55) * mm});
            skPoint(sketch, "E43.14.0.8", {"position": v(298.75, -23.72) * mm});
            skArc(sketch, "E43.14.0.9", {"start": v(297.98, -21.55) * mm, "mid": v(297.76, -20.97) * mm, "end": v(297.19, -20.73) * mm});
            skLineSegment(sketch, "E43.14.0.10", {"start": v(300.87, -20.73) * mm, "end": v(300.13, -20.73) * mm});
            skArc(sketch, "E43.14.0.11", {"start": v(299.99, -22.45) * mm, "mid": v(300.08, -22.13) * mm, "end": v(300.1, -21.8) * mm});
            skArc(sketch, "E43.14.0.12", {"start": v(297.97, -21.8) * mm, "mid": v(297.99, -22.13) * mm, "end": v(298.08, -22.45) * mm});
            skPoint(sketch, "E43.14.0.13", {"position": v(299.12, -23.73) * mm});
            skArc(sketch, "E43.14.0.14", {"start": v(298.6, -23.48) * mm, "mid": v(298.77, -23.66) * mm, "end": v(299.02, -23.72) * mm});
            skArc(sketch, "E43.14.0.15", {"start": v(300.87, -20.73) * mm, "mid": v(300.3, -20.97) * mm, "end": v(300.09, -21.55) * mm});
            skArc(sketch, "E43.14.0.16", {"start": v(299.03, -23.73) * mm, "mid": v(299.28, -23.66) * mm, "end": v(299.47, -23.48) * mm});
            skLineSegment(sketch, "E43.14.0.17", {"start": v(299.03, -23.73) * mm, "end": v(299.02, -23.72) * mm});
            skLineSegment(sketch, "E43.14.0.18", {"start": v(299.02, -23.72) * mm, "end": v(299.03, -23.73) * mm});
            skArc(sketch, "E43.15.0.0", {"start": v(293.73, -22.45) * mm, "mid": v(293.97, -22.98) * mm, "end": v(294.25, -23.48) * mm});
            skPoint(sketch, "E43.15.0.1", {"position": v(293.67, -20.63) * mm});
            skLineSegment(sketch, "E43.15.0.2", {"start": v(293.62, -21.8) * mm, "end": v(293.63, -21.55) * mm});
            skPoint(sketch, "E43.15.0.3", {"position": v(295.77, -22.11) * mm});
            skPoint(sketch, "E43.15.0.4", {"position": v(294.97, -23.73) * mm});
            skArc(sketch, "E43.15.0.5", {"start": v(295.64, -22.45) * mm, "mid": v(295.4, -22.98) * mm, "end": v(295.13, -23.48) * mm});
            skPoint(sketch, "E43.15.0.6", {"position": v(293.6, -22.11) * mm});
            skLineSegment(sketch, "E43.15.0.7", {"start": v(295.75, -21.8) * mm, "end": v(295.74, -21.55) * mm});
            skPoint(sketch, "E43.15.0.8", {"position": v(294.4, -23.72) * mm});
            skArc(sketch, "E43.15.0.9", {"start": v(293.63, -21.55) * mm, "mid": v(293.41, -20.97) * mm, "end": v(292.85, -20.73) * mm});
            skLineSegment(sketch, "E43.15.0.10", {"start": v(296.53, -20.73) * mm, "end": v(295.78, -20.73) * mm});
            skArc(sketch, "E43.15.0.11", {"start": v(295.64, -22.45) * mm, "mid": v(295.73, -22.13) * mm, "end": v(295.75, -21.8) * mm});
            skArc(sketch, "E43.15.0.12", {"start": v(293.62, -21.8) * mm, "mid": v(293.64, -22.13) * mm, "end": v(293.73, -22.45) * mm});
            skPoint(sketch, "E43.15.0.13", {"position": v(294.78, -23.73) * mm});
            skArc(sketch, "E43.15.0.14", {"start": v(294.25, -23.48) * mm, "mid": v(294.43, -23.66) * mm, "end": v(294.68, -23.72) * mm});
            skArc(sketch, "E43.15.0.15", {"start": v(296.53, -20.73) * mm, "mid": v(295.96, -20.97) * mm, "end": v(295.74, -21.55) * mm});
            skArc(sketch, "E43.15.0.16", {"start": v(294.69, -23.73) * mm, "mid": v(294.94, -23.66) * mm, "end": v(295.13, -23.48) * mm});
            skLineSegment(sketch, "E43.15.0.17", {"start": v(294.69, -23.73) * mm, "end": v(294.68, -23.72) * mm});
            skLineSegment(sketch, "E43.15.0.18", {"start": v(294.68, -23.72) * mm, "end": v(294.69, -23.73) * mm});
            skArc(sketch, "E43.16.0.0", {"start": v(289.4, -22.45) * mm, "mid": v(289.63, -22.98) * mm, "end": v(289.9, -23.48) * mm});
            skPoint(sketch, "E43.16.0.1", {"position": v(289.33, -20.63) * mm});
            skLineSegment(sketch, "E43.16.0.2", {"start": v(289.28, -21.8) * mm, "end": v(289.29, -21.55) * mm});
            skPoint(sketch, "E43.16.0.3", {"position": v(291.42, -22.11) * mm});
            skPoint(sketch, "E43.16.0.4", {"position": v(290.63, -23.73) * mm});
            skArc(sketch, "E43.16.0.5", {"start": v(291.3, -22.45) * mm, "mid": v(291.06, -22.98) * mm, "end": v(290.78, -23.48) * mm});
            skPoint(sketch, "E43.16.0.6", {"position": v(289.26, -22.11) * mm});
            skLineSegment(sketch, "E43.16.0.7", {"start": v(291.4, -21.8) * mm, "end": v(291.4, -21.55) * mm});
            skPoint(sketch, "E43.16.0.8", {"position": v(290.06, -23.72) * mm});
            skArc(sketch, "E43.16.0.9", {"start": v(289.29, -21.55) * mm, "mid": v(289.07, -20.97) * mm, "end": v(288.5, -20.73) * mm});
            skLineSegment(sketch, "E43.16.0.10", {"start": v(292.19, -20.73) * mm, "end": v(291.44, -20.73) * mm});
            skArc(sketch, "E43.16.0.11", {"start": v(291.3, -22.45) * mm, "mid": v(291.39, -22.13) * mm, "end": v(291.4, -21.8) * mm});
            skArc(sketch, "E43.16.0.12", {"start": v(289.28, -21.8) * mm, "mid": v(289.3, -22.13) * mm, "end": v(289.4, -22.45) * mm});
            skPoint(sketch, "E43.16.0.13", {"position": v(290.43, -23.73) * mm});
            skArc(sketch, "E43.16.0.14", {"start": v(289.9, -23.48) * mm, "mid": v(290.09, -23.66) * mm, "end": v(290.33, -23.72) * mm});
            skArc(sketch, "E43.16.0.15", {"start": v(292.19, -20.73) * mm, "mid": v(291.62, -20.97) * mm, "end": v(291.4, -21.55) * mm});
            skArc(sketch, "E43.16.0.16", {"start": v(290.34, -23.73) * mm, "mid": v(290.6, -23.66) * mm, "end": v(290.78, -23.48) * mm});
            skLineSegment(sketch, "E43.16.0.17", {"start": v(290.34, -23.73) * mm, "end": v(290.33, -23.72) * mm});
            skLineSegment(sketch, "E43.16.0.18", {"start": v(290.33, -23.72) * mm, "end": v(290.34, -23.73) * mm});
            skArc(sketch, "E43.17.0.0", {"start": v(285.05, -22.45) * mm, "mid": v(285.28, -22.98) * mm, "end": v(285.56, -23.48) * mm});
            skPoint(sketch, "E43.17.0.1", {"position": v(284.99, -20.63) * mm});
            skLineSegment(sketch, "E43.17.0.2", {"start": v(284.94, -21.8) * mm, "end": v(284.95, -21.55) * mm});
            skPoint(sketch, "E43.17.0.3", {"position": v(287.08, -22.11) * mm});
            skPoint(sketch, "E43.17.0.4", {"position": v(286.28, -23.73) * mm});
            skArc(sketch, "E43.17.0.5", {"start": v(286.96, -22.45) * mm, "mid": v(286.72, -22.98) * mm, "end": v(286.44, -23.48) * mm});
            skPoint(sketch, "E43.17.0.6", {"position": v(284.92, -22.11) * mm});
            skLineSegment(sketch, "E43.17.0.7", {"start": v(287.07, -21.8) * mm, "end": v(287.06, -21.55) * mm});
            skPoint(sketch, "E43.17.0.8", {"position": v(285.72, -23.72) * mm});
            skArc(sketch, "E43.17.0.9", {"start": v(284.95, -21.55) * mm, "mid": v(284.73, -20.97) * mm, "end": v(284.16, -20.73) * mm});
            skLineSegment(sketch, "E43.17.0.10", {"start": v(287.84, -20.73) * mm, "end": v(287.1, -20.73) * mm});
            skArc(sketch, "E43.17.0.11", {"start": v(286.96, -22.45) * mm, "mid": v(287.05, -22.13) * mm, "end": v(287.07, -21.8) * mm});
            skArc(sketch, "E43.17.0.12", {"start": v(284.94, -21.8) * mm, "mid": v(284.96, -22.13) * mm, "end": v(285.05, -22.45) * mm});
            skPoint(sketch, "E43.17.0.13", {"position": v(286.1, -23.73) * mm});
            skArc(sketch, "E43.17.0.14", {"start": v(285.56, -23.48) * mm, "mid": v(285.74, -23.66) * mm, "end": v(285.99, -23.72) * mm});
            skArc(sketch, "E43.17.0.15", {"start": v(287.84, -20.73) * mm, "mid": v(287.27, -20.97) * mm, "end": v(287.06, -21.55) * mm});
            skArc(sketch, "E43.17.0.16", {"start": v(286, -23.73) * mm, "mid": v(286.25, -23.66) * mm, "end": v(286.44, -23.48) * mm});
            skLineSegment(sketch, "E43.17.0.17", {"start": v(286, -23.73) * mm, "end": v(285.99, -23.72) * mm});
            skLineSegment(sketch, "E43.17.0.18", {"start": v(285.99, -23.72) * mm, "end": v(286, -23.73) * mm});
            skArc(sketch, "E43.18.0.0", {"start": v(280.7, -22.45) * mm, "mid": v(280.94, -22.98) * mm, "end": v(281.22, -23.48) * mm});
            skPoint(sketch, "E43.18.0.1", {"position": v(280.64, -20.63) * mm});
            skLineSegment(sketch, "E43.18.0.2", {"start": v(280.6, -21.8) * mm, "end": v(280.6, -21.55) * mm});
            skPoint(sketch, "E43.18.0.3", {"position": v(282.74, -22.11) * mm});
            skPoint(sketch, "E43.18.0.4", {"position": v(281.94, -23.73) * mm});
            skArc(sketch, "E43.18.0.5", {"start": v(282.61, -22.45) * mm, "mid": v(282.38, -22.98) * mm, "end": v(282.1, -23.48) * mm});
            skPoint(sketch, "E43.18.0.6", {"position": v(280.58, -22.11) * mm});
            skLineSegment(sketch, "E43.18.0.7", {"start": v(282.72, -21.8) * mm, "end": v(282.71, -21.55) * mm});
            skPoint(sketch, "E43.18.0.8", {"position": v(281.37, -23.72) * mm});
            skArc(sketch, "E43.18.0.9", {"start": v(280.6, -21.55) * mm, "mid": v(280.38, -20.97) * mm, "end": v(279.82, -20.73) * mm});
            skLineSegment(sketch, "E43.18.0.10", {"start": v(283.5, -20.73) * mm, "end": v(282.75, -20.73) * mm});
            skArc(sketch, "E43.18.0.11", {"start": v(282.61, -22.45) * mm, "mid": v(282.7, -22.13) * mm, "end": v(282.72, -21.8) * mm});
            skArc(sketch, "E43.18.0.12", {"start": v(280.6, -21.8) * mm, "mid": v(280.61, -22.13) * mm, "end": v(280.7, -22.45) * mm});
            skPoint(sketch, "E43.18.0.13", {"position": v(281.75, -23.73) * mm});
            skArc(sketch, "E43.18.0.14", {"start": v(281.22, -23.48) * mm, "mid": v(281.4, -23.66) * mm, "end": v(281.65, -23.72) * mm});
            skArc(sketch, "E43.18.0.15", {"start": v(283.5, -20.73) * mm, "mid": v(282.93, -20.97) * mm, "end": v(282.71, -21.55) * mm});
            skArc(sketch, "E43.18.0.16", {"start": v(281.66, -23.73) * mm, "mid": v(281.9, -23.66) * mm, "end": v(282.1, -23.48) * mm});
            skLineSegment(sketch, "E43.18.0.17", {"start": v(281.66, -23.73) * mm, "end": v(281.65, -23.72) * mm});
            skLineSegment(sketch, "E43.18.0.18", {"start": v(281.65, -23.72) * mm, "end": v(281.66, -23.73) * mm});
            skArc(sketch, "E43.19.0.0", {"start": v(276.36, -22.45) * mm, "mid": v(276.6, -22.98) * mm, "end": v(276.88, -23.48) * mm});
            skPoint(sketch, "E43.19.0.1", {"position": v(276.3, -20.63) * mm});
            skLineSegment(sketch, "E43.19.0.2", {"start": v(276.25, -21.8) * mm, "end": v(276.26, -21.55) * mm});
            skPoint(sketch, "E43.19.0.3", {"position": v(278.4, -22.11) * mm});
            skPoint(sketch, "E43.19.0.4", {"position": v(277.6, -23.73) * mm});
            skArc(sketch, "E43.19.0.5", {"start": v(278.27, -22.45) * mm, "mid": v(278.03, -22.98) * mm, "end": v(277.75, -23.48) * mm});
            skPoint(sketch, "E43.19.0.6", {"position": v(276.23, -22.11) * mm});
            skLineSegment(sketch, "E43.19.0.7", {"start": v(278.38, -21.8) * mm, "end": v(278.37, -21.55) * mm});
            skPoint(sketch, "E43.19.0.8", {"position": v(277.03, -23.72) * mm});
            skArc(sketch, "E43.19.0.9", {"start": v(276.26, -21.55) * mm, "mid": v(276.04, -20.97) * mm, "end": v(275.47, -20.73) * mm});
            skLineSegment(sketch, "E43.19.0.10", {"start": v(279.16, -20.73) * mm, "end": v(278.4, -20.73) * mm});
            skArc(sketch, "E43.19.0.11", {"start": v(278.27, -22.45) * mm, "mid": v(278.36, -22.13) * mm, "end": v(278.38, -21.8) * mm});
            skArc(sketch, "E43.19.0.12", {"start": v(276.25, -21.8) * mm, "mid": v(276.27, -22.13) * mm, "end": v(276.36, -22.45) * mm});
            skPoint(sketch, "E43.19.0.13", {"position": v(277.4, -23.73) * mm});
            skArc(sketch, "E43.19.0.14", {"start": v(276.88, -23.48) * mm, "mid": v(277.06, -23.66) * mm, "end": v(277.3, -23.72) * mm});
            skArc(sketch, "E43.19.0.15", {"start": v(279.16, -20.73) * mm, "mid": v(278.59, -20.97) * mm, "end": v(278.37, -21.55) * mm});
            skArc(sketch, "E43.19.0.16", {"start": v(277.31, -23.73) * mm, "mid": v(277.57, -23.66) * mm, "end": v(277.75, -23.48) * mm});
            skLineSegment(sketch, "E43.19.0.17", {"start": v(277.31, -23.73) * mm, "end": v(277.3, -23.72) * mm});
            skLineSegment(sketch, "E43.19.0.18", {"start": v(277.3, -23.72) * mm, "end": v(277.31, -23.73) * mm});
            skArc(sketch, "E43.20.0.0", {"start": v(272.02, -22.45) * mm, "mid": v(272.25, -22.98) * mm, "end": v(272.53, -23.48) * mm});
            skPoint(sketch, "E43.20.0.1", {"position": v(271.96, -20.63) * mm});
            skLineSegment(sketch, "E43.20.0.2", {"start": v(271.9, -21.8) * mm, "end": v(271.92, -21.55) * mm});
            skPoint(sketch, "E43.20.0.3", {"position": v(274.05, -22.11) * mm});
            skPoint(sketch, "E43.20.0.4", {"position": v(273.25, -23.73) * mm});
            skArc(sketch, "E43.20.0.5", {"start": v(273.93, -22.45) * mm, "mid": v(273.7, -22.98) * mm, "end": v(273.41, -23.48) * mm});
            skPoint(sketch, "E43.20.0.6", {"position": v(271.9, -22.11) * mm});
            skLineSegment(sketch, "E43.20.0.7", {"start": v(274.04, -21.8) * mm, "end": v(274.03, -21.55) * mm});
            skPoint(sketch, "E43.20.0.8", {"position": v(272.69, -23.72) * mm});
            skArc(sketch, "E43.20.0.9", {"start": v(271.92, -21.55) * mm, "mid": v(271.7, -20.97) * mm, "end": v(271.13, -20.73) * mm});
            skLineSegment(sketch, "E43.20.0.10", {"start": v(274.81, -20.73) * mm, "end": v(274.07, -20.73) * mm});
            skArc(sketch, "E43.20.0.11", {"start": v(273.93, -22.45) * mm, "mid": v(274.02, -22.13) * mm, "end": v(274.04, -21.8) * mm});
            skArc(sketch, "E43.20.0.12", {"start": v(271.9, -21.8) * mm, "mid": v(271.93, -22.13) * mm, "end": v(272.02, -22.45) * mm});
            skPoint(sketch, "E43.20.0.13", {"position": v(273.06, -23.73) * mm});
            skArc(sketch, "E43.20.0.14", {"start": v(272.53, -23.48) * mm, "mid": v(272.71, -23.66) * mm, "end": v(272.96, -23.72) * mm});
            skArc(sketch, "E43.20.0.15", {"start": v(274.81, -20.73) * mm, "mid": v(274.24, -20.97) * mm, "end": v(274.03, -21.55) * mm});
            skArc(sketch, "E43.20.0.16", {"start": v(272.97, -23.73) * mm, "mid": v(273.22, -23.66) * mm, "end": v(273.41, -23.48) * mm});
            skLineSegment(sketch, "E43.20.0.17", {"start": v(272.97, -23.73) * mm, "end": v(272.96, -23.72) * mm});
            skLineSegment(sketch, "E43.20.0.18", {"start": v(272.96, -23.72) * mm, "end": v(272.97, -23.73) * mm});
            skArc(sketch, "E43.21.0.0", {"start": v(267.67, -22.45) * mm, "mid": v(267.9, -22.98) * mm, "end": v(268.19, -23.48) * mm});
            skPoint(sketch, "E43.21.0.1", {"position": v(267.61, -20.63) * mm});
            skLineSegment(sketch, "E43.21.0.2", {"start": v(267.56, -21.8) * mm, "end": v(267.57, -21.55) * mm});
            skPoint(sketch, "E43.21.0.3", {"position": v(269.7, -22.11) * mm});
            skPoint(sketch, "E43.21.0.4", {"position": v(268.9, -23.73) * mm});
            skArc(sketch, "E43.21.0.5", {"start": v(269.58, -22.45) * mm, "mid": v(269.35, -22.98) * mm, "end": v(269.07, -23.48) * mm});
            skPoint(sketch, "E43.21.0.6", {"position": v(267.55, -22.11) * mm});
            skLineSegment(sketch, "E43.21.0.7", {"start": v(269.7, -21.8) * mm, "end": v(269.68, -21.55) * mm});
            skPoint(sketch, "E43.21.0.8", {"position": v(268.34, -23.72) * mm});
            skArc(sketch, "E43.21.0.9", {"start": v(267.57, -21.55) * mm, "mid": v(267.35, -20.97) * mm, "end": v(266.79, -20.73) * mm});
            skLineSegment(sketch, "E43.21.0.10", {"start": v(270.47, -20.73) * mm, "end": v(269.72, -20.73) * mm});
            skArc(sketch, "E43.21.0.11", {"start": v(269.58, -22.45) * mm, "mid": v(269.67, -22.13) * mm, "end": v(269.7, -21.8) * mm});
            skArc(sketch, "E43.21.0.12", {"start": v(267.56, -21.8) * mm, "mid": v(267.58, -22.13) * mm, "end": v(267.67, -22.45) * mm});
            skPoint(sketch, "E43.21.0.13", {"position": v(268.72, -23.73) * mm});
            skArc(sketch, "E43.21.0.14", {"start": v(268.19, -23.48) * mm, "mid": v(268.37, -23.66) * mm, "end": v(268.62, -23.72) * mm});
            skArc(sketch, "E43.21.0.15", {"start": v(270.47, -20.73) * mm, "mid": v(269.9, -20.97) * mm, "end": v(269.68, -21.55) * mm});
            skArc(sketch, "E43.21.0.16", {"start": v(268.63, -23.73) * mm, "mid": v(268.88, -23.66) * mm, "end": v(269.07, -23.48) * mm});
            skLineSegment(sketch, "E43.21.0.17", {"start": v(268.63, -23.73) * mm, "end": v(268.62, -23.72) * mm});
            skLineSegment(sketch, "E43.21.0.18", {"start": v(268.62, -23.72) * mm, "end": v(268.63, -23.73) * mm});
            skArc(sketch, "E43.22.0.0", {"start": v(263.33, -22.45) * mm, "mid": v(263.57, -22.98) * mm, "end": v(263.85, -23.48) * mm});
            skPoint(sketch, "E43.22.0.1", {"position": v(263.27, -20.63) * mm});
            skLineSegment(sketch, "E43.22.0.2", {"start": v(263.22, -21.8) * mm, "end": v(263.23, -21.55) * mm});
            skPoint(sketch, "E43.22.0.3", {"position": v(265.36, -22.11) * mm});
            skPoint(sketch, "E43.22.0.4", {"position": v(264.57, -23.73) * mm});
            skArc(sketch, "E43.22.0.5", {"start": v(265.24, -22.45) * mm, "mid": v(265, -22.98) * mm, "end": v(264.72, -23.48) * mm});
            skPoint(sketch, "E43.22.0.6", {"position": v(263.2, -22.11) * mm});
            skLineSegment(sketch, "E43.22.0.7", {"start": v(265.35, -21.8) * mm, "end": v(265.34, -21.55) * mm});
            skPoint(sketch, "E43.22.0.8", {"position": v(264, -23.72) * mm});
            skArc(sketch, "E43.22.0.9", {"start": v(263.23, -21.55) * mm, "mid": v(263.01, -20.97) * mm, "end": v(262.44, -20.73) * mm});
            skLineSegment(sketch, "E43.22.0.10", {"start": v(266.13, -20.73) * mm, "end": v(265.38, -20.73) * mm});
            skArc(sketch, "E43.22.0.11", {"start": v(265.24, -22.45) * mm, "mid": v(265.33, -22.13) * mm, "end": v(265.35, -21.8) * mm});
            skArc(sketch, "E43.22.0.12", {"start": v(263.22, -21.8) * mm, "mid": v(263.24, -22.13) * mm, "end": v(263.33, -22.45) * mm});
            skPoint(sketch, "E43.22.0.13", {"position": v(264.37, -23.73) * mm});
            skArc(sketch, "E43.22.0.14", {"start": v(263.85, -23.48) * mm, "mid": v(264.03, -23.66) * mm, "end": v(264.27, -23.72) * mm});
            skArc(sketch, "E43.22.0.15", {"start": v(266.13, -20.73) * mm, "mid": v(265.56, -20.97) * mm, "end": v(265.34, -21.55) * mm});
            skArc(sketch, "E43.22.0.16", {"start": v(264.28, -23.73) * mm, "mid": v(264.54, -23.66) * mm, "end": v(264.72, -23.48) * mm});
            skLineSegment(sketch, "E43.22.0.17", {"start": v(264.28, -23.73) * mm, "end": v(264.27, -23.72) * mm});
            skLineSegment(sketch, "E43.22.0.18", {"start": v(264.27, -23.72) * mm, "end": v(264.28, -23.73) * mm});
            skArc(sketch, "E43.23.0.0", {"start": v(258.99, -22.45) * mm, "mid": v(259.22, -22.98) * mm, "end": v(259.5, -23.48) * mm});
            skPoint(sketch, "E43.23.0.1", {"position": v(258.92, -20.63) * mm});
            skLineSegment(sketch, "E43.23.0.2", {"start": v(258.87, -21.8) * mm, "end": v(258.89, -21.55) * mm});
            skPoint(sketch, "E43.23.0.3", {"position": v(261.02, -22.11) * mm});
            skPoint(sketch, "E43.23.0.4", {"position": v(260.22, -23.73) * mm});
            skArc(sketch, "E43.23.0.5", {"start": v(260.9, -22.45) * mm, "mid": v(260.66, -22.98) * mm, "end": v(260.38, -23.48) * mm});
            skPoint(sketch, "E43.23.0.6", {"position": v(258.86, -22.11) * mm});
            skLineSegment(sketch, "E43.23.0.7", {"start": v(261, -21.8) * mm, "end": v(261, -21.55) * mm});
            skPoint(sketch, "E43.23.0.8", {"position": v(259.66, -23.72) * mm});
            skArc(sketch, "E43.23.0.9", {"start": v(258.89, -21.55) * mm, "mid": v(258.67, -20.97) * mm, "end": v(258.1, -20.73) * mm});
            skLineSegment(sketch, "E43.23.0.10", {"start": v(261.78, -20.73) * mm, "end": v(261.04, -20.73) * mm});
            skArc(sketch, "E43.23.0.11", {"start": v(260.9, -22.45) * mm, "mid": v(260.99, -22.13) * mm, "end": v(261, -21.8) * mm});
            skArc(sketch, "E43.23.0.12", {"start": v(258.87, -21.8) * mm, "mid": v(258.9, -22.13) * mm, "end": v(258.99, -22.45) * mm});
            skPoint(sketch, "E43.23.0.13", {"position": v(260.03, -23.73) * mm});
            skArc(sketch, "E43.23.0.14", {"start": v(259.5, -23.48) * mm, "mid": v(259.68, -23.66) * mm, "end": v(259.93, -23.72) * mm});
            skArc(sketch, "E43.23.0.15", {"start": v(261.78, -20.73) * mm, "mid": v(261.21, -20.97) * mm, "end": v(261, -21.55) * mm});
            skArc(sketch, "E43.23.0.16", {"start": v(259.94, -23.73) * mm, "mid": v(260.2, -23.66) * mm, "end": v(260.38, -23.48) * mm});
            skLineSegment(sketch, "E43.23.0.17", {"start": v(259.94, -23.73) * mm, "end": v(259.93, -23.72) * mm});
            skLineSegment(sketch, "E43.23.0.18", {"start": v(259.93, -23.72) * mm, "end": v(259.94, -23.73) * mm});
            skArc(sketch, "E43.24.0.0", {"start": v(254.64, -22.45) * mm, "mid": v(254.88, -22.98) * mm, "end": v(255.16, -23.48) * mm});
            skPoint(sketch, "E43.24.0.1", {"position": v(254.58, -20.63) * mm});
            skLineSegment(sketch, "E43.24.0.2", {"start": v(254.53, -21.8) * mm, "end": v(254.54, -21.55) * mm});
            skPoint(sketch, "E43.24.0.3", {"position": v(256.68, -22.11) * mm});
            skPoint(sketch, "E43.24.0.4", {"position": v(255.88, -23.73) * mm});
            skArc(sketch, "E43.24.0.5", {"start": v(256.55, -22.45) * mm, "mid": v(256.32, -22.98) * mm, "end": v(256.04, -23.48) * mm});
            skPoint(sketch, "E43.24.0.6", {"position": v(254.52, -22.11) * mm});
            skLineSegment(sketch, "E43.24.0.7", {"start": v(256.66, -21.8) * mm, "end": v(256.65, -21.55) * mm});
            skPoint(sketch, "E43.24.0.8", {"position": v(255.31, -23.72) * mm});
            skArc(sketch, "E43.24.0.9", {"start": v(254.54, -21.55) * mm, "mid": v(254.32, -20.97) * mm, "end": v(253.76, -20.73) * mm});
            skLineSegment(sketch, "E43.24.0.10", {"start": v(257.44, -20.73) * mm, "end": v(256.7, -20.73) * mm});
            skArc(sketch, "E43.24.0.11", {"start": v(256.55, -22.45) * mm, "mid": v(256.64, -22.13) * mm, "end": v(256.66, -21.8) * mm});
            skArc(sketch, "E43.24.0.12", {"start": v(254.53, -21.8) * mm, "mid": v(254.55, -22.13) * mm, "end": v(254.64, -22.45) * mm});
            skPoint(sketch, "E43.24.0.13", {"position": v(255.69, -23.73) * mm});
            skArc(sketch, "E43.24.0.14", {"start": v(255.16, -23.48) * mm, "mid": v(255.34, -23.66) * mm, "end": v(255.59, -23.72) * mm});
            skArc(sketch, "E43.24.0.15", {"start": v(257.44, -20.73) * mm, "mid": v(256.87, -20.97) * mm, "end": v(256.65, -21.55) * mm});
            skArc(sketch, "E43.24.0.16", {"start": v(255.6, -23.73) * mm, "mid": v(255.85, -23.66) * mm, "end": v(256.04, -23.48) * mm});
            skLineSegment(sketch, "E43.24.0.17", {"start": v(255.6, -23.73) * mm, "end": v(255.59, -23.72) * mm});
            skLineSegment(sketch, "E43.24.0.18", {"start": v(255.59, -23.72) * mm, "end": v(255.6, -23.73) * mm});
            skArc(sketch, "E43.25.0.0", {"start": v(250.3, -22.45) * mm, "mid": v(250.54, -22.98) * mm, "end": v(250.82, -23.48) * mm});
            skPoint(sketch, "E43.25.0.1", {"position": v(250.24, -20.63) * mm});
            skLineSegment(sketch, "E43.25.0.2", {"start": v(250.19, -21.8) * mm, "end": v(250.2, -21.55) * mm});
            skPoint(sketch, "E43.25.0.3", {"position": v(252.33, -22.11) * mm});
            skPoint(sketch, "E43.25.0.4", {"position": v(251.54, -23.73) * mm});
            skArc(sketch, "E43.25.0.5", {"start": v(252.2, -22.45) * mm, "mid": v(251.97, -22.98) * mm, "end": v(251.7, -23.48) * mm});
            skPoint(sketch, "E43.25.0.6", {"position": v(250.17, -22.11) * mm});
            skLineSegment(sketch, "E43.25.0.7", {"start": v(252.32, -21.8) * mm, "end": v(252.3, -21.55) * mm});
            skPoint(sketch, "E43.25.0.8", {"position": v(250.97, -23.72) * mm});
            skArc(sketch, "E43.25.0.9", {"start": v(250.2, -21.55) * mm, "mid": v(249.98, -20.97) * mm, "end": v(249.41, -20.73) * mm});
            skLineSegment(sketch, "E43.25.0.10", {"start": v(253.1, -20.73) * mm, "end": v(252.35, -20.73) * mm});
            skArc(sketch, "E43.25.0.11", {"start": v(252.2, -22.45) * mm, "mid": v(252.3, -22.13) * mm, "end": v(252.32, -21.8) * mm});
            skArc(sketch, "E43.25.0.12", {"start": v(250.19, -21.8) * mm, "mid": v(250.2, -22.13) * mm, "end": v(250.3, -22.45) * mm});
            skPoint(sketch, "E43.25.0.13", {"position": v(251.34, -23.73) * mm});
            skArc(sketch, "E43.25.0.14", {"start": v(250.82, -23.48) * mm, "mid": v(251, -23.66) * mm, "end": v(251.24, -23.72) * mm});
            skArc(sketch, "E43.25.0.15", {"start": v(253.1, -20.73) * mm, "mid": v(252.53, -20.97) * mm, "end": v(252.3, -21.55) * mm});
            skArc(sketch, "E43.25.0.16", {"start": v(251.25, -23.73) * mm, "mid": v(251.5, -23.66) * mm, "end": v(251.7, -23.48) * mm});
            skLineSegment(sketch, "E43.25.0.17", {"start": v(251.25, -23.73) * mm, "end": v(251.24, -23.72) * mm});
            skLineSegment(sketch, "E43.25.0.18", {"start": v(251.24, -23.72) * mm, "end": v(251.25, -23.73) * mm});
            skArc(sketch, "E43.26.0.0", {"start": v(245.96, -22.45) * mm, "mid": v(246.2, -22.98) * mm, "end": v(246.47, -23.48) * mm});
            skPoint(sketch, "E43.26.0.1", {"position": v(245.9, -20.63) * mm});
            skLineSegment(sketch, "E43.26.0.2", {"start": v(245.84, -21.8) * mm, "end": v(245.86, -21.55) * mm});
            skPoint(sketch, "E43.26.0.3", {"position": v(247.99, -22.11) * mm});
            skPoint(sketch, "E43.26.0.4", {"position": v(247.2, -23.73) * mm});
            skArc(sketch, "E43.26.0.5", {"start": v(247.86, -22.45) * mm, "mid": v(247.63, -22.98) * mm, "end": v(247.35, -23.48) * mm});
            skPoint(sketch, "E43.26.0.6", {"position": v(245.83, -22.11) * mm});
            skLineSegment(sketch, "E43.26.0.7", {"start": v(247.98, -21.8) * mm, "end": v(247.97, -21.55) * mm});
            skPoint(sketch, "E43.26.0.8", {"position": v(246.63, -23.72) * mm});
            skArc(sketch, "E43.26.0.9", {"start": v(245.86, -21.55) * mm, "mid": v(245.64, -20.97) * mm, "end": v(245.07, -20.73) * mm});
            skLineSegment(sketch, "E43.26.0.10", {"start": v(248.75, -20.73) * mm, "end": v(248, -20.73) * mm});
            skArc(sketch, "E43.26.0.11", {"start": v(247.86, -22.45) * mm, "mid": v(247.96, -22.13) * mm, "end": v(247.98, -21.8) * mm});
            skArc(sketch, "E43.26.0.12", {"start": v(245.84, -21.8) * mm, "mid": v(245.87, -22.13) * mm, "end": v(245.96, -22.45) * mm});
            skPoint(sketch, "E43.26.0.13", {"position": v(247, -23.73) * mm});
            skArc(sketch, "E43.26.0.14", {"start": v(246.47, -23.48) * mm, "mid": v(246.65, -23.66) * mm, "end": v(246.9, -23.72) * mm});
            skArc(sketch, "E43.26.0.15", {"start": v(248.75, -20.73) * mm, "mid": v(248.18, -20.97) * mm, "end": v(247.97, -21.55) * mm});
            skArc(sketch, "E43.26.0.16", {"start": v(246.91, -23.73) * mm, "mid": v(247.16, -23.66) * mm, "end": v(247.35, -23.48) * mm});
            skLineSegment(sketch, "E43.26.0.17", {"start": v(246.91, -23.73) * mm, "end": v(246.9, -23.72) * mm});
            skLineSegment(sketch, "E43.26.0.18", {"start": v(246.9, -23.72) * mm, "end": v(246.91, -23.73) * mm});
            skArc(sketch, "E43.27.0.0", {"start": v(241.61, -22.45) * mm, "mid": v(241.85, -22.98) * mm, "end": v(242.13, -23.48) * mm});
            skPoint(sketch, "E43.27.0.1", {"position": v(241.55, -20.63) * mm});
            skLineSegment(sketch, "E43.27.0.2", {"start": v(241.5, -21.8) * mm, "end": v(241.51, -21.55) * mm});
            skPoint(sketch, "E43.27.0.3", {"position": v(243.65, -22.11) * mm});
            skPoint(sketch, "E43.27.0.4", {"position": v(242.85, -23.73) * mm});
            skArc(sketch, "E43.27.0.5", {"start": v(243.52, -22.45) * mm, "mid": v(243.29, -22.98) * mm, "end": v(243, -23.48) * mm});
            skPoint(sketch, "E43.27.0.6", {"position": v(241.49, -22.11) * mm});
            skLineSegment(sketch, "E43.27.0.7", {"start": v(243.63, -21.8) * mm, "end": v(243.62, -21.55) * mm});
            skPoint(sketch, "E43.27.0.8", {"position": v(242.28, -23.72) * mm});
            skArc(sketch, "E43.27.0.9", {"start": v(241.51, -21.55) * mm, "mid": v(241.3, -20.97) * mm, "end": v(240.73, -20.73) * mm});
            skLineSegment(sketch, "E43.27.0.10", {"start": v(244.4, -20.73) * mm, "end": v(243.66, -20.73) * mm});
            skArc(sketch, "E43.27.0.11", {"start": v(243.52, -22.45) * mm, "mid": v(243.61, -22.13) * mm, "end": v(243.63, -21.8) * mm});
            skArc(sketch, "E43.27.0.12", {"start": v(241.5, -21.8) * mm, "mid": v(241.52, -22.13) * mm, "end": v(241.61, -22.45) * mm});
            skPoint(sketch, "E43.27.0.13", {"position": v(242.66, -23.73) * mm});
            skArc(sketch, "E43.27.0.14", {"start": v(242.13, -23.48) * mm, "mid": v(242.31, -23.66) * mm, "end": v(242.56, -23.72) * mm});
            skArc(sketch, "E43.27.0.15", {"start": v(244.4, -20.73) * mm, "mid": v(243.84, -20.97) * mm, "end": v(243.62, -21.55) * mm});
            skArc(sketch, "E43.27.0.16", {"start": v(242.57, -23.73) * mm, "mid": v(242.82, -23.66) * mm, "end": v(243, -23.48) * mm});
            skLineSegment(sketch, "E43.27.0.17", {"start": v(242.57, -23.73) * mm, "end": v(242.56, -23.72) * mm});
            skLineSegment(sketch, "E43.27.0.18", {"start": v(242.56, -23.72) * mm, "end": v(242.57, -23.73) * mm});
            skArc(sketch, "E43.28.0.0", {"start": v(237.27, -22.45) * mm, "mid": v(237.5, -22.98) * mm, "end": v(237.79, -23.48) * mm});
            skPoint(sketch, "E43.28.0.1", {"position": v(237.2, -20.63) * mm});
            skLineSegment(sketch, "E43.28.0.2", {"start": v(237.16, -21.8) * mm, "end": v(237.17, -21.55) * mm});
            skPoint(sketch, "E43.28.0.3", {"position": v(239.3, -22.11) * mm});
            skPoint(sketch, "E43.28.0.4", {"position": v(238.5, -23.73) * mm});
            skArc(sketch, "E43.28.0.5", {"start": v(239.18, -22.45) * mm, "mid": v(238.94, -22.98) * mm, "end": v(238.66, -23.48) * mm});
            skPoint(sketch, "E43.28.0.6", {"position": v(237.14, -22.11) * mm});
            skLineSegment(sketch, "E43.28.0.7", {"start": v(239.29, -21.8) * mm, "end": v(239.28, -21.55) * mm});
            skPoint(sketch, "E43.28.0.8", {"position": v(237.94, -23.72) * mm});
            skArc(sketch, "E43.28.0.9", {"start": v(237.17, -21.55) * mm, "mid": v(236.95, -20.97) * mm, "end": v(236.38, -20.73) * mm});
            skLineSegment(sketch, "E43.28.0.10", {"start": v(240.06, -20.73) * mm, "end": v(239.32, -20.73) * mm});
            skArc(sketch, "E43.28.0.11", {"start": v(239.18, -22.45) * mm, "mid": v(239.27, -22.13) * mm, "end": v(239.29, -21.8) * mm});
            skArc(sketch, "E43.28.0.12", {"start": v(237.16, -21.8) * mm, "mid": v(237.18, -22.13) * mm, "end": v(237.27, -22.45) * mm});
            skPoint(sketch, "E43.28.0.13", {"position": v(238.31, -23.73) * mm});
            skArc(sketch, "E43.28.0.14", {"start": v(237.79, -23.48) * mm, "mid": v(237.97, -23.66) * mm, "end": v(238.21, -23.72) * mm});
            skArc(sketch, "E43.28.0.15", {"start": v(240.06, -20.73) * mm, "mid": v(239.5, -20.97) * mm, "end": v(239.28, -21.55) * mm});
            skArc(sketch, "E43.28.0.16", {"start": v(238.22, -23.73) * mm, "mid": v(238.48, -23.66) * mm, "end": v(238.66, -23.48) * mm});
            skLineSegment(sketch, "E43.28.0.17", {"start": v(238.22, -23.73) * mm, "end": v(238.21, -23.72) * mm});
            skLineSegment(sketch, "E43.28.0.18", {"start": v(238.21, -23.72) * mm, "end": v(238.22, -23.73) * mm});
            skArc(sketch, "E43.29.0.0", {"start": v(232.93, -22.45) * mm, "mid": v(233.16, -22.98) * mm, "end": v(233.44, -23.48) * mm});
            skPoint(sketch, "E43.29.0.1", {"position": v(232.86, -20.63) * mm});
            skLineSegment(sketch, "E43.29.0.2", {"start": v(232.81, -21.8) * mm, "end": v(232.83, -21.55) * mm});
            skPoint(sketch, "E43.29.0.3", {"position": v(234.96, -22.11) * mm});
            skPoint(sketch, "E43.29.0.4", {"position": v(234.16, -23.73) * mm});
            skArc(sketch, "E43.29.0.5", {"start": v(234.83, -22.45) * mm, "mid": v(234.6, -22.98) * mm, "end": v(234.32, -23.48) * mm});
            skPoint(sketch, "E43.29.0.6", {"position": v(232.8, -22.11) * mm});
            skLineSegment(sketch, "E43.29.0.7", {"start": v(234.95, -21.8) * mm, "end": v(234.93, -21.55) * mm});
            skPoint(sketch, "E43.29.0.8", {"position": v(233.6, -23.72) * mm});
            skArc(sketch, "E43.29.0.9", {"start": v(232.83, -21.55) * mm, "mid": v(232.6, -20.97) * mm, "end": v(232.04, -20.73) * mm});
            skLineSegment(sketch, "E43.29.0.10", {"start": v(235.72, -20.73) * mm, "end": v(234.98, -20.73) * mm});
            skArc(sketch, "E43.29.0.11", {"start": v(234.83, -22.45) * mm, "mid": v(234.93, -22.13) * mm, "end": v(234.95, -21.8) * mm});
            skArc(sketch, "E43.29.0.12", {"start": v(232.81, -21.8) * mm, "mid": v(232.84, -22.13) * mm, "end": v(232.93, -22.45) * mm});
            skPoint(sketch, "E43.29.0.13", {"position": v(233.97, -23.73) * mm});
            skArc(sketch, "E43.29.0.14", {"start": v(233.44, -23.48) * mm, "mid": v(233.62, -23.66) * mm, "end": v(233.87, -23.72) * mm});
            skArc(sketch, "E43.29.0.15", {"start": v(235.72, -20.73) * mm, "mid": v(235.15, -20.97) * mm, "end": v(234.93, -21.55) * mm});
            skArc(sketch, "E43.29.0.16", {"start": v(233.88, -23.73) * mm, "mid": v(234.13, -23.66) * mm, "end": v(234.32, -23.48) * mm});
            skLineSegment(sketch, "E43.29.0.17", {"start": v(233.88, -23.73) * mm, "end": v(233.87, -23.72) * mm});
            skLineSegment(sketch, "E43.29.0.18", {"start": v(233.87, -23.72) * mm, "end": v(233.88, -23.73) * mm});
            skArc(sketch, "E43.30.0.0", {"start": v(228.58, -22.45) * mm, "mid": v(228.82, -22.98) * mm, "end": v(229.1, -23.48) * mm});
            skPoint(sketch, "E43.30.0.1", {"position": v(228.52, -20.63) * mm});
            skLineSegment(sketch, "E43.30.0.2", {"start": v(228.47, -21.8) * mm, "end": v(228.48, -21.55) * mm});
            skPoint(sketch, "E43.30.0.3", {"position": v(230.62, -22.11) * mm});
            skPoint(sketch, "E43.30.0.4", {"position": v(229.82, -23.73) * mm});
            skArc(sketch, "E43.30.0.5", {"start": v(230.5, -22.45) * mm, "mid": v(230.26, -22.98) * mm, "end": v(229.98, -23.48) * mm});
            skPoint(sketch, "E43.30.0.6", {"position": v(228.46, -22.11) * mm});
            skLineSegment(sketch, "E43.30.0.7", {"start": v(230.6, -21.8) * mm, "end": v(230.6, -21.55) * mm});
            skPoint(sketch, "E43.30.0.8", {"position": v(229.25, -23.72) * mm});
            skArc(sketch, "E43.30.0.9", {"start": v(228.48, -21.55) * mm, "mid": v(228.26, -20.97) * mm, "end": v(227.7, -20.73) * mm});
            skLineSegment(sketch, "E43.30.0.10", {"start": v(231.38, -20.73) * mm, "end": v(230.63, -20.73) * mm});
            skArc(sketch, "E43.30.0.11", {"start": v(230.5, -22.45) * mm, "mid": v(230.58, -22.13) * mm, "end": v(230.6, -21.8) * mm});
            skArc(sketch, "E43.30.0.12", {"start": v(228.47, -21.8) * mm, "mid": v(228.5, -22.13) * mm, "end": v(228.58, -22.45) * mm});
            skPoint(sketch, "E43.30.0.13", {"position": v(229.63, -23.73) * mm});
            skArc(sketch, "E43.30.0.14", {"start": v(229.1, -23.48) * mm, "mid": v(229.28, -23.66) * mm, "end": v(229.52, -23.72) * mm});
            skArc(sketch, "E43.30.0.15", {"start": v(231.38, -20.73) * mm, "mid": v(230.8, -20.97) * mm, "end": v(230.6, -21.55) * mm});
            skArc(sketch, "E43.30.0.16", {"start": v(229.54, -23.73) * mm, "mid": v(229.79, -23.66) * mm, "end": v(229.98, -23.48) * mm});
            skLineSegment(sketch, "E43.30.0.17", {"start": v(229.54, -23.73) * mm, "end": v(229.52, -23.72) * mm});
            skLineSegment(sketch, "E43.30.0.18", {"start": v(229.52, -23.72) * mm, "end": v(229.54, -23.73) * mm});
            skArc(sketch, "E43.31.0.0", {"start": v(224.24, -22.45) * mm, "mid": v(224.48, -22.98) * mm, "end": v(224.75, -23.48) * mm});
            skPoint(sketch, "E43.31.0.1", {"position": v(224.18, -20.63) * mm});
            skLineSegment(sketch, "E43.31.0.2", {"start": v(224.13, -21.8) * mm, "end": v(224.14, -21.55) * mm});
            skPoint(sketch, "E43.31.0.3", {"position": v(226.27, -22.11) * mm});
            skPoint(sketch, "E43.31.0.4", {"position": v(225.47, -23.73) * mm});
            skArc(sketch, "E43.31.0.5", {"start": v(226.15, -22.45) * mm, "mid": v(225.91, -22.98) * mm, "end": v(225.63, -23.48) * mm});
            skPoint(sketch, "E43.31.0.6", {"position": v(224.11, -22.11) * mm});
            skLineSegment(sketch, "E43.31.0.7", {"start": v(226.26, -21.8) * mm, "end": v(226.25, -21.55) * mm});
            skPoint(sketch, "E43.31.0.8", {"position": v(224.9, -23.72) * mm});
            skArc(sketch, "E43.31.0.9", {"start": v(224.14, -21.55) * mm, "mid": v(223.92, -20.97) * mm, "end": v(223.35, -20.73) * mm});
            skLineSegment(sketch, "E43.31.0.10", {"start": v(227.03, -20.73) * mm, "end": v(226.29, -20.73) * mm});
            skArc(sketch, "E43.31.0.11", {"start": v(226.15, -22.45) * mm, "mid": v(226.24, -22.13) * mm, "end": v(226.26, -21.8) * mm});
            skArc(sketch, "E43.31.0.12", {"start": v(224.13, -21.8) * mm, "mid": v(224.15, -22.13) * mm, "end": v(224.24, -22.45) * mm});
            skPoint(sketch, "E43.31.0.13", {"position": v(225.28, -23.73) * mm});
            skArc(sketch, "E43.31.0.14", {"start": v(224.75, -23.48) * mm, "mid": v(224.94, -23.66) * mm, "end": v(225.18, -23.72) * mm});
            skArc(sketch, "E43.31.0.15", {"start": v(227.03, -20.73) * mm, "mid": v(226.47, -20.97) * mm, "end": v(226.25, -21.55) * mm});
            skArc(sketch, "E43.31.0.16", {"start": v(225.2, -23.73) * mm, "mid": v(225.45, -23.66) * mm, "end": v(225.63, -23.48) * mm});
            skLineSegment(sketch, "E43.31.0.17", {"start": v(225.2, -23.73) * mm, "end": v(225.18, -23.72) * mm});
            skLineSegment(sketch, "E43.31.0.18", {"start": v(225.18, -23.72) * mm, "end": v(225.2, -23.73) * mm});
            skArc(sketch, "E43.32.0.0", {"start": v(219.9, -22.45) * mm, "mid": v(220.13, -22.98) * mm, "end": v(220.41, -23.48) * mm});
            skPoint(sketch, "E43.32.0.1", {"position": v(219.83, -20.63) * mm});
            skLineSegment(sketch, "E43.32.0.2", {"start": v(219.78, -21.8) * mm, "end": v(219.8, -21.55) * mm});
            skPoint(sketch, "E43.32.0.3", {"position": v(221.93, -22.11) * mm});
            skPoint(sketch, "E43.32.0.4", {"position": v(221.13, -23.73) * mm});
            skArc(sketch, "E43.32.0.5", {"start": v(221.8, -22.45) * mm, "mid": v(221.57, -22.98) * mm, "end": v(221.29, -23.48) * mm});
            skPoint(sketch, "E43.32.0.6", {"position": v(219.77, -22.11) * mm});
            skLineSegment(sketch, "E43.32.0.7", {"start": v(221.92, -21.8) * mm, "end": v(221.9, -21.55) * mm});
            skPoint(sketch, "E43.32.0.8", {"position": v(220.57, -23.72) * mm});
            skArc(sketch, "E43.32.0.9", {"start": v(219.8, -21.55) * mm, "mid": v(219.58, -20.97) * mm, "end": v(219, -20.73) * mm});
            skLineSegment(sketch, "E43.32.0.10", {"start": v(222.7, -20.73) * mm, "end": v(221.95, -20.73) * mm});
            skArc(sketch, "E43.32.0.11", {"start": v(221.8, -22.45) * mm, "mid": v(221.9, -22.13) * mm, "end": v(221.92, -21.8) * mm});
            skArc(sketch, "E43.32.0.12", {"start": v(219.78, -21.8) * mm, "mid": v(219.8, -22.13) * mm, "end": v(219.9, -22.45) * mm});
            skPoint(sketch, "E43.32.0.13", {"position": v(220.94, -23.73) * mm});
            skArc(sketch, "E43.32.0.14", {"start": v(220.41, -23.48) * mm, "mid": v(220.6, -23.66) * mm, "end": v(220.84, -23.72) * mm});
            skArc(sketch, "E43.32.0.15", {"start": v(222.7, -20.73) * mm, "mid": v(222.12, -20.97) * mm, "end": v(221.9, -21.55) * mm});
            skArc(sketch, "E43.32.0.16", {"start": v(220.85, -23.73) * mm, "mid": v(221.1, -23.66) * mm, "end": v(221.29, -23.48) * mm});
            skLineSegment(sketch, "E43.32.0.17", {"start": v(220.85, -23.73) * mm, "end": v(220.84, -23.72) * mm});
            skLineSegment(sketch, "E43.32.0.18", {"start": v(220.84, -23.72) * mm, "end": v(220.85, -23.73) * mm});
            skArc(sketch, "E43.33.0.0", {"start": v(215.55, -22.45) * mm, "mid": v(215.79, -22.98) * mm, "end": v(216.07, -23.48) * mm});
            skPoint(sketch, "E43.33.0.1", {"position": v(215.5, -20.63) * mm});
            skLineSegment(sketch, "E43.33.0.2", {"start": v(215.44, -21.8) * mm, "end": v(215.45, -21.55) * mm});
            skPoint(sketch, "E43.33.0.3", {"position": v(217.59, -22.11) * mm});
            skPoint(sketch, "E43.33.0.4", {"position": v(216.79, -23.73) * mm});
            skArc(sketch, "E43.33.0.5", {"start": v(217.46, -22.45) * mm, "mid": v(217.23, -22.98) * mm, "end": v(216.95, -23.48) * mm});
            skPoint(sketch, "E43.33.0.6", {"position": v(215.43, -22.11) * mm});
            skLineSegment(sketch, "E43.33.0.7", {"start": v(217.57, -21.8) * mm, "end": v(217.56, -21.55) * mm});
            skPoint(sketch, "E43.33.0.8", {"position": v(216.22, -23.72) * mm});
            skArc(sketch, "E43.33.0.9", {"start": v(215.45, -21.55) * mm, "mid": v(215.23, -20.97) * mm, "end": v(214.66, -20.73) * mm});
            skLineSegment(sketch, "E43.33.0.10", {"start": v(218.35, -20.73) * mm, "end": v(217.6, -20.73) * mm});
            skArc(sketch, "E43.33.0.11", {"start": v(217.46, -22.45) * mm, "mid": v(217.55, -22.13) * mm, "end": v(217.57, -21.8) * mm});
            skArc(sketch, "E43.33.0.12", {"start": v(215.44, -21.8) * mm, "mid": v(215.46, -22.13) * mm, "end": v(215.55, -22.45) * mm});
            skPoint(sketch, "E43.33.0.13", {"position": v(216.6, -23.73) * mm});
            skArc(sketch, "E43.33.0.14", {"start": v(216.07, -23.48) * mm, "mid": v(216.25, -23.66) * mm, "end": v(216.5, -23.72) * mm});
            skArc(sketch, "E43.33.0.15", {"start": v(218.35, -20.73) * mm, "mid": v(217.78, -20.97) * mm, "end": v(217.56, -21.55) * mm});
            skArc(sketch, "E43.33.0.16", {"start": v(216.5, -23.73) * mm, "mid": v(216.76, -23.66) * mm, "end": v(216.95, -23.48) * mm});
            skLineSegment(sketch, "E43.33.0.17", {"start": v(216.5, -23.73) * mm, "end": v(216.5, -23.72) * mm});
            skLineSegment(sketch, "E43.33.0.18", {"start": v(216.5, -23.72) * mm, "end": v(216.5, -23.73) * mm});
            skArc(sketch, "E43.34.0.0", {"start": v(211.2, -22.45) * mm, "mid": v(211.44, -22.98) * mm, "end": v(211.72, -23.48) * mm});
            skPoint(sketch, "E43.34.0.1", {"position": v(211.15, -20.63) * mm});
            skLineSegment(sketch, "E43.34.0.2", {"start": v(211.1, -21.8) * mm, "end": v(211.1, -21.55) * mm});
            skPoint(sketch, "E43.34.0.3", {"position": v(213.24, -22.11) * mm});
            skPoint(sketch, "E43.34.0.4", {"position": v(212.44, -23.73) * mm});
            skArc(sketch, "E43.34.0.5", {"start": v(213.12, -22.45) * mm, "mid": v(212.88, -22.98) * mm, "end": v(212.6, -23.48) * mm});
            skPoint(sketch, "E43.34.0.6", {"position": v(211.08, -22.11) * mm});
            skLineSegment(sketch, "E43.34.0.7", {"start": v(213.23, -21.8) * mm, "end": v(213.22, -21.55) * mm});
            skPoint(sketch, "E43.34.0.8", {"position": v(211.88, -23.72) * mm});
            skArc(sketch, "E43.34.0.9", {"start": v(211.1, -21.55) * mm, "mid": v(210.89, -20.97) * mm, "end": v(210.32, -20.73) * mm});
            skLineSegment(sketch, "E43.34.0.10", {"start": v(214, -20.73) * mm, "end": v(213.26, -20.73) * mm});
            skArc(sketch, "E43.34.0.11", {"start": v(213.12, -22.45) * mm, "mid": v(213.2, -22.13) * mm, "end": v(213.23, -21.8) * mm});
            skArc(sketch, "E43.34.0.12", {"start": v(211.1, -21.8) * mm, "mid": v(211.12, -22.13) * mm, "end": v(211.2, -22.45) * mm});
            skPoint(sketch, "E43.34.0.13", {"position": v(212.25, -23.73) * mm});
            skArc(sketch, "E43.34.0.14", {"start": v(211.72, -23.48) * mm, "mid": v(211.9, -23.66) * mm, "end": v(212.15, -23.72) * mm});
            skArc(sketch, "E43.34.0.15", {"start": v(214, -20.73) * mm, "mid": v(213.44, -20.97) * mm, "end": v(213.22, -21.55) * mm});
            skArc(sketch, "E43.34.0.16", {"start": v(212.16, -23.73) * mm, "mid": v(212.42, -23.66) * mm, "end": v(212.6, -23.48) * mm});
            skLineSegment(sketch, "E43.34.0.17", {"start": v(212.16, -23.73) * mm, "end": v(212.15, -23.72) * mm});
            skLineSegment(sketch, "E43.34.0.18", {"start": v(212.15, -23.72) * mm, "end": v(212.16, -23.73) * mm});
            skArc(sketch, "E43.35.0.0", {"start": v(206.87, -22.45) * mm, "mid": v(207.1, -22.98) * mm, "end": v(207.38, -23.48) * mm});
            skPoint(sketch, "E43.35.0.1", {"position": v(206.8, -20.63) * mm});
            skLineSegment(sketch, "E43.35.0.2", {"start": v(206.75, -21.8) * mm, "end": v(206.76, -21.55) * mm});
            skPoint(sketch, "E43.35.0.3", {"position": v(208.9, -22.11) * mm});
            skPoint(sketch, "E43.35.0.4", {"position": v(208.1, -23.73) * mm});
            skArc(sketch, "E43.35.0.5", {"start": v(208.77, -22.45) * mm, "mid": v(208.54, -22.98) * mm, "end": v(208.26, -23.48) * mm});
            skPoint(sketch, "E43.35.0.6", {"position": v(206.74, -22.11) * mm});
            skLineSegment(sketch, "E43.35.0.7", {"start": v(208.89, -21.8) * mm, "end": v(208.87, -21.55) * mm});
            skPoint(sketch, "E43.35.0.8", {"position": v(207.53, -23.72) * mm});
            skArc(sketch, "E43.35.0.9", {"start": v(206.76, -21.55) * mm, "mid": v(206.55, -20.97) * mm, "end": v(205.98, -20.73) * mm});
            skLineSegment(sketch, "E43.35.0.10", {"start": v(209.66, -20.73) * mm, "end": v(208.91, -20.73) * mm});
            skArc(sketch, "E43.35.0.11", {"start": v(208.77, -22.45) * mm, "mid": v(208.86, -22.13) * mm, "end": v(208.89, -21.8) * mm});
            skArc(sketch, "E43.35.0.12", {"start": v(206.75, -21.8) * mm, "mid": v(206.77, -22.13) * mm, "end": v(206.87, -22.45) * mm});
            skPoint(sketch, "E43.35.0.13", {"position": v(207.91, -23.73) * mm});
            skArc(sketch, "E43.35.0.14", {"start": v(207.38, -23.48) * mm, "mid": v(207.56, -23.66) * mm, "end": v(207.8, -23.72) * mm});
            skArc(sketch, "E43.35.0.15", {"start": v(209.66, -20.73) * mm, "mid": v(209.1, -20.97) * mm, "end": v(208.87, -21.55) * mm});
            skArc(sketch, "E43.35.0.16", {"start": v(207.82, -23.73) * mm, "mid": v(208.07, -23.66) * mm, "end": v(208.26, -23.48) * mm});
            skLineSegment(sketch, "E43.35.0.17", {"start": v(207.82, -23.73) * mm, "end": v(207.8, -23.72) * mm});
            skLineSegment(sketch, "E43.35.0.18", {"start": v(207.8, -23.72) * mm, "end": v(207.82, -23.73) * mm});
            skArc(sketch, "E43.36.0.0", {"start": v(202.52, -22.45) * mm, "mid": v(202.76, -22.98) * mm, "end": v(203.04, -23.48) * mm});
            skPoint(sketch, "E43.36.0.1", {"position": v(202.46, -20.63) * mm});
            skLineSegment(sketch, "E43.36.0.2", {"start": v(202.41, -21.8) * mm, "end": v(202.42, -21.55) * mm});
            skPoint(sketch, "E43.36.0.3", {"position": v(204.56, -22.11) * mm});
            skPoint(sketch, "E43.36.0.4", {"position": v(203.76, -23.73) * mm});
            skArc(sketch, "E43.36.0.5", {"start": v(204.43, -22.45) * mm, "mid": v(204.2, -22.98) * mm, "end": v(203.92, -23.48) * mm});
            skPoint(sketch, "E43.36.0.6", {"position": v(202.4, -22.11) * mm});
            skLineSegment(sketch, "E43.36.0.7", {"start": v(204.54, -21.8) * mm, "end": v(204.53, -21.55) * mm});
            skPoint(sketch, "E43.36.0.8", {"position": v(203.2, -23.72) * mm});
            skArc(sketch, "E43.36.0.9", {"start": v(202.42, -21.55) * mm, "mid": v(202.2, -20.97) * mm, "end": v(201.63, -20.73) * mm});
            skLineSegment(sketch, "E43.36.0.10", {"start": v(205.32, -20.73) * mm, "end": v(204.57, -20.73) * mm});
            skArc(sketch, "E43.36.0.11", {"start": v(204.43, -22.45) * mm, "mid": v(204.52, -22.13) * mm, "end": v(204.54, -21.8) * mm});
            skArc(sketch, "E43.36.0.12", {"start": v(202.41, -21.8) * mm, "mid": v(202.43, -22.13) * mm, "end": v(202.52, -22.45) * mm});
            skPoint(sketch, "E43.36.0.13", {"position": v(203.57, -23.73) * mm});
            skArc(sketch, "E43.36.0.14", {"start": v(203.04, -23.48) * mm, "mid": v(203.22, -23.66) * mm, "end": v(203.46, -23.72) * mm});
            skArc(sketch, "E43.36.0.15", {"start": v(205.32, -20.73) * mm, "mid": v(204.75, -20.97) * mm, "end": v(204.53, -21.55) * mm});
            skArc(sketch, "E43.36.0.16", {"start": v(203.48, -23.73) * mm, "mid": v(203.73, -23.66) * mm, "end": v(203.92, -23.48) * mm});
            skLineSegment(sketch, "E43.36.0.17", {"start": v(203.48, -23.73) * mm, "end": v(203.46, -23.72) * mm});
            skLineSegment(sketch, "E43.36.0.18", {"start": v(203.46, -23.72) * mm, "end": v(203.48, -23.73) * mm});
            skArc(sketch, "E43.37.0.0", {"start": v(198.18, -22.45) * mm, "mid": v(198.41, -22.98) * mm, "end": v(198.7, -23.48) * mm});
            skPoint(sketch, "E43.37.0.1", {"position": v(198.12, -20.63) * mm});
            skLineSegment(sketch, "E43.37.0.2", {"start": v(198.07, -21.8) * mm, "end": v(198.08, -21.55) * mm});
            skPoint(sketch, "E43.37.0.3", {"position": v(200.21, -22.11) * mm});
            skPoint(sketch, "E43.37.0.4", {"position": v(199.41, -23.73) * mm});
            skArc(sketch, "E43.37.0.5", {"start": v(200.09, -22.45) * mm, "mid": v(199.85, -22.98) * mm, "end": v(199.57, -23.48) * mm});
            skPoint(sketch, "E43.37.0.6", {"position": v(198.05, -22.11) * mm});
            skLineSegment(sketch, "E43.37.0.7", {"start": v(200.2, -21.8) * mm, "end": v(200.19, -21.55) * mm});
            skPoint(sketch, "E43.37.0.8", {"position": v(198.85, -23.72) * mm});
            skArc(sketch, "E43.37.0.9", {"start": v(198.08, -21.55) * mm, "mid": v(197.86, -20.97) * mm, "end": v(197.3, -20.73) * mm});
            skLineSegment(sketch, "E43.37.0.10", {"start": v(200.97, -20.73) * mm, "end": v(200.23, -20.73) * mm});
            skArc(sketch, "E43.37.0.11", {"start": v(200.09, -22.45) * mm, "mid": v(200.18, -22.13) * mm, "end": v(200.2, -21.8) * mm});
            skArc(sketch, "E43.37.0.12", {"start": v(198.07, -21.8) * mm, "mid": v(198.09, -22.13) * mm, "end": v(198.18, -22.45) * mm});
            skPoint(sketch, "E43.37.0.13", {"position": v(199.22, -23.73) * mm});
            skArc(sketch, "E43.37.0.14", {"start": v(198.7, -23.48) * mm, "mid": v(198.88, -23.66) * mm, "end": v(199.12, -23.72) * mm});
            skArc(sketch, "E43.37.0.15", {"start": v(200.97, -20.73) * mm, "mid": v(200.4, -20.97) * mm, "end": v(200.19, -21.55) * mm});
            skArc(sketch, "E43.37.0.16", {"start": v(199.13, -23.73) * mm, "mid": v(199.39, -23.66) * mm, "end": v(199.57, -23.48) * mm});
            skLineSegment(sketch, "E43.37.0.17", {"start": v(199.13, -23.73) * mm, "end": v(199.12, -23.72) * mm});
            skLineSegment(sketch, "E43.37.0.18", {"start": v(199.12, -23.72) * mm, "end": v(199.13, -23.73) * mm});
            skArc(sketch, "E43.38.0.0", {"start": v(193.84, -22.45) * mm, "mid": v(194.07, -22.98) * mm, "end": v(194.35, -23.48) * mm});
            skPoint(sketch, "E43.38.0.1", {"position": v(193.77, -20.63) * mm});
            skLineSegment(sketch, "E43.38.0.2", {"start": v(193.72, -21.8) * mm, "end": v(193.73, -21.55) * mm});
            skPoint(sketch, "E43.38.0.3", {"position": v(195.87, -22.11) * mm});
            skPoint(sketch, "E43.38.0.4", {"position": v(195.07, -23.73) * mm});
            skArc(sketch, "E43.38.0.5", {"start": v(195.74, -22.45) * mm, "mid": v(195.5, -22.98) * mm, "end": v(195.23, -23.48) * mm});
            skPoint(sketch, "E43.38.0.6", {"position": v(193.71, -22.11) * mm});
            skLineSegment(sketch, "E43.38.0.7", {"start": v(195.86, -21.8) * mm, "end": v(195.84, -21.55) * mm});
            skPoint(sketch, "E43.38.0.8", {"position": v(194.5, -23.72) * mm});
            skArc(sketch, "E43.38.0.9", {"start": v(193.73, -21.55) * mm, "mid": v(193.52, -20.97) * mm, "end": v(192.95, -20.73) * mm});
            skLineSegment(sketch, "E43.38.0.10", {"start": v(196.63, -20.73) * mm, "end": v(195.88, -20.73) * mm});
            skArc(sketch, "E43.38.0.11", {"start": v(195.74, -22.45) * mm, "mid": v(195.83, -22.13) * mm, "end": v(195.86, -21.8) * mm});
            skArc(sketch, "E43.38.0.12", {"start": v(193.72, -21.8) * mm, "mid": v(193.74, -22.13) * mm, "end": v(193.84, -22.45) * mm});
            skPoint(sketch, "E43.38.0.13", {"position": v(194.88, -23.73) * mm});
            skArc(sketch, "E43.38.0.14", {"start": v(194.35, -23.48) * mm, "mid": v(194.53, -23.66) * mm, "end": v(194.78, -23.72) * mm});
            skArc(sketch, "E43.38.0.15", {"start": v(196.63, -20.73) * mm, "mid": v(196.06, -20.97) * mm, "end": v(195.84, -21.55) * mm});
            skArc(sketch, "E43.38.0.16", {"start": v(194.79, -23.73) * mm, "mid": v(195.04, -23.66) * mm, "end": v(195.23, -23.48) * mm});
            skLineSegment(sketch, "E43.38.0.17", {"start": v(194.79, -23.73) * mm, "end": v(194.78, -23.72) * mm});
            skLineSegment(sketch, "E43.38.0.18", {"start": v(194.78, -23.72) * mm, "end": v(194.79, -23.73) * mm});
            skArc(sketch, "E43.39.0.0", {"start": v(189.5, -22.45) * mm, "mid": v(189.73, -22.98) * mm, "end": v(190, -23.48) * mm});
            skPoint(sketch, "E43.39.0.1", {"position": v(189.43, -20.63) * mm});
            skLineSegment(sketch, "E43.39.0.2", {"start": v(189.38, -21.8) * mm, "end": v(189.4, -21.55) * mm});
            skPoint(sketch, "E43.39.0.3", {"position": v(191.53, -22.11) * mm});
            skPoint(sketch, "E43.39.0.4", {"position": v(190.73, -23.73) * mm});
            skArc(sketch, "E43.39.0.5", {"start": v(191.4, -22.45) * mm, "mid": v(191.17, -22.98) * mm, "end": v(190.89, -23.48) * mm});
            skPoint(sketch, "E43.39.0.6", {"position": v(189.37, -22.11) * mm});
            skLineSegment(sketch, "E43.39.0.7", {"start": v(191.51, -21.8) * mm, "end": v(191.5, -21.55) * mm});
            skPoint(sketch, "E43.39.0.8", {"position": v(190.16, -23.72) * mm});
            skArc(sketch, "E43.39.0.9", {"start": v(189.4, -21.55) * mm, "mid": v(189.17, -20.97) * mm, "end": v(188.6, -20.73) * mm});
            skLineSegment(sketch, "E43.39.0.10", {"start": v(192.29, -20.73) * mm, "end": v(191.54, -20.73) * mm});
            skArc(sketch, "E43.39.0.11", {"start": v(191.4, -22.45) * mm, "mid": v(191.5, -22.13) * mm, "end": v(191.51, -21.8) * mm});
            skArc(sketch, "E43.39.0.12", {"start": v(189.38, -21.8) * mm, "mid": v(189.4, -22.13) * mm, "end": v(189.5, -22.45) * mm});
            skPoint(sketch, "E43.39.0.13", {"position": v(190.54, -23.73) * mm});
            skArc(sketch, "E43.39.0.14", {"start": v(190, -23.48) * mm, "mid": v(190.19, -23.66) * mm, "end": v(190.43, -23.72) * mm});
            skArc(sketch, "E43.39.0.15", {"start": v(192.29, -20.73) * mm, "mid": v(191.72, -20.97) * mm, "end": v(191.5, -21.55) * mm});
            skArc(sketch, "E43.39.0.16", {"start": v(190.45, -23.73) * mm, "mid": v(190.7, -23.66) * mm, "end": v(190.89, -23.48) * mm});
            skLineSegment(sketch, "E43.39.0.17", {"start": v(190.45, -23.73) * mm, "end": v(190.43, -23.72) * mm});
            skLineSegment(sketch, "E43.39.0.18", {"start": v(190.43, -23.72) * mm, "end": v(190.45, -23.73) * mm});
            skArc(sketch, "E43.40.0.0", {"start": v(185.15, -22.45) * mm, "mid": v(185.38, -22.98) * mm, "end": v(185.66, -23.48) * mm});
            skPoint(sketch, "E43.40.0.1", {"position": v(185.09, -20.63) * mm});
            skLineSegment(sketch, "E43.40.0.2", {"start": v(185.04, -21.8) * mm, "end": v(185.05, -21.55) * mm});
            skPoint(sketch, "E43.40.0.3", {"position": v(187.18, -22.11) * mm});
            skPoint(sketch, "E43.40.0.4", {"position": v(186.38, -23.73) * mm});
            skArc(sketch, "E43.40.0.5", {"start": v(187.06, -22.45) * mm, "mid": v(186.82, -22.98) * mm, "end": v(186.54, -23.48) * mm});
            skPoint(sketch, "E43.40.0.6", {"position": v(185.02, -22.11) * mm});
            skLineSegment(sketch, "E43.40.0.7", {"start": v(187.17, -21.8) * mm, "end": v(187.16, -21.55) * mm});
            skPoint(sketch, "E43.40.0.8", {"position": v(185.82, -23.72) * mm});
            skArc(sketch, "E43.40.0.9", {"start": v(185.05, -21.55) * mm, "mid": v(184.83, -20.97) * mm, "end": v(184.26, -20.73) * mm});
            skLineSegment(sketch, "E43.40.0.10", {"start": v(187.94, -20.73) * mm, "end": v(187.2, -20.73) * mm});
            skArc(sketch, "E43.40.0.11", {"start": v(187.06, -22.45) * mm, "mid": v(187.15, -22.13) * mm, "end": v(187.17, -21.8) * mm});
            skArc(sketch, "E43.40.0.12", {"start": v(185.04, -21.8) * mm, "mid": v(185.06, -22.13) * mm, "end": v(185.15, -22.45) * mm});
            skPoint(sketch, "E43.40.0.13", {"position": v(186.2, -23.73) * mm});
            skArc(sketch, "E43.40.0.14", {"start": v(185.66, -23.48) * mm, "mid": v(185.85, -23.66) * mm, "end": v(186.1, -23.72) * mm});
            skArc(sketch, "E43.40.0.15", {"start": v(187.94, -20.73) * mm, "mid": v(187.38, -20.97) * mm, "end": v(187.16, -21.55) * mm});
            skArc(sketch, "E43.40.0.16", {"start": v(186.1, -23.73) * mm, "mid": v(186.35, -23.66) * mm, "end": v(186.54, -23.48) * mm});
            skLineSegment(sketch, "E43.40.0.17", {"start": v(186.1, -23.73) * mm, "end": v(186.1, -23.72) * mm});
            skLineSegment(sketch, "E43.40.0.18", {"start": v(186.1, -23.72) * mm, "end": v(186.1, -23.73) * mm});
            skArc(sketch, "E43.41.0.0", {"start": v(180.8, -22.45) * mm, "mid": v(181.04, -22.98) * mm, "end": v(181.32, -23.48) * mm});
            skPoint(sketch, "E43.41.0.1", {"position": v(180.74, -20.63) * mm});
            skLineSegment(sketch, "E43.41.0.2", {"start": v(180.7, -21.8) * mm, "end": v(180.7, -21.55) * mm});
            skPoint(sketch, "E43.41.0.3", {"position": v(182.84, -22.11) * mm});
            skPoint(sketch, "E43.41.0.4", {"position": v(182.04, -23.73) * mm});
            skArc(sketch, "E43.41.0.5", {"start": v(182.71, -22.45) * mm, "mid": v(182.48, -22.98) * mm, "end": v(182.2, -23.48) * mm});
            skPoint(sketch, "E43.41.0.6", {"position": v(180.68, -22.11) * mm});
            skLineSegment(sketch, "E43.41.0.7", {"start": v(182.82, -21.8) * mm, "end": v(182.81, -21.55) * mm});
            skPoint(sketch, "E43.41.0.8", {"position": v(181.47, -23.72) * mm});
            skArc(sketch, "E43.41.0.9", {"start": v(180.7, -21.55) * mm, "mid": v(180.49, -20.97) * mm, "end": v(179.92, -20.73) * mm});
            skLineSegment(sketch, "E43.41.0.10", {"start": v(183.6, -20.73) * mm, "end": v(182.85, -20.73) * mm});
            skArc(sketch, "E43.41.0.11", {"start": v(182.71, -22.45) * mm, "mid": v(182.8, -22.13) * mm, "end": v(182.82, -21.8) * mm});
            skArc(sketch, "E43.41.0.12", {"start": v(180.7, -21.8) * mm, "mid": v(180.71, -22.13) * mm, "end": v(180.8, -22.45) * mm});
            skPoint(sketch, "E43.41.0.13", {"position": v(181.85, -23.73) * mm});
            skArc(sketch, "E43.41.0.14", {"start": v(181.32, -23.48) * mm, "mid": v(181.5, -23.66) * mm, "end": v(181.75, -23.72) * mm});
            skArc(sketch, "E43.41.0.15", {"start": v(183.6, -20.73) * mm, "mid": v(183.03, -20.97) * mm, "end": v(182.81, -21.55) * mm});
            skArc(sketch, "E43.41.0.16", {"start": v(181.76, -23.73) * mm, "mid": v(182.01, -23.66) * mm, "end": v(182.2, -23.48) * mm});
            skLineSegment(sketch, "E43.41.0.17", {"start": v(181.76, -23.73) * mm, "end": v(181.75, -23.72) * mm});
            skLineSegment(sketch, "E43.41.0.18", {"start": v(181.75, -23.72) * mm, "end": v(181.76, -23.73) * mm});
            skArc(sketch, "E43.42.0.0", {"start": v(176.46, -22.45) * mm, "mid": v(176.7, -22.98) * mm, "end": v(176.98, -23.48) * mm});
            skPoint(sketch, "E43.42.0.1", {"position": v(176.4, -20.63) * mm});
            skLineSegment(sketch, "E43.42.0.2", {"start": v(176.35, -21.8) * mm, "end": v(176.36, -21.55) * mm});
            skPoint(sketch, "E43.42.0.3", {"position": v(178.5, -22.11) * mm});
            skPoint(sketch, "E43.42.0.4", {"position": v(177.7, -23.73) * mm});
            skArc(sketch, "E43.42.0.5", {"start": v(178.37, -22.45) * mm, "mid": v(178.14, -22.98) * mm, "end": v(177.86, -23.48) * mm});
            skPoint(sketch, "E43.42.0.6", {"position": v(176.34, -22.11) * mm});
            skLineSegment(sketch, "E43.42.0.7", {"start": v(178.48, -21.8) * mm, "end": v(178.47, -21.55) * mm});
            skPoint(sketch, "E43.42.0.8", {"position": v(177.13, -23.72) * mm});
            skArc(sketch, "E43.42.0.9", {"start": v(176.36, -21.55) * mm, "mid": v(176.14, -20.97) * mm, "end": v(175.57, -20.73) * mm});
            skLineSegment(sketch, "E43.42.0.10", {"start": v(179.26, -20.73) * mm, "end": v(178.51, -20.73) * mm});
            skArc(sketch, "E43.42.0.11", {"start": v(178.37, -22.45) * mm, "mid": v(178.46, -22.13) * mm, "end": v(178.48, -21.8) * mm});
            skArc(sketch, "E43.42.0.12", {"start": v(176.35, -21.8) * mm, "mid": v(176.37, -22.13) * mm, "end": v(176.46, -22.45) * mm});
            skPoint(sketch, "E43.42.0.13", {"position": v(177.5, -23.73) * mm});
            skArc(sketch, "E43.42.0.14", {"start": v(176.98, -23.48) * mm, "mid": v(177.16, -23.66) * mm, "end": v(177.4, -23.72) * mm});
            skArc(sketch, "E43.42.0.15", {"start": v(179.26, -20.73) * mm, "mid": v(178.69, -20.97) * mm, "end": v(178.47, -21.55) * mm});
            skArc(sketch, "E43.42.0.16", {"start": v(177.42, -23.73) * mm, "mid": v(177.67, -23.66) * mm, "end": v(177.86, -23.48) * mm});
            skLineSegment(sketch, "E43.42.0.17", {"start": v(177.42, -23.73) * mm, "end": v(177.4, -23.72) * mm});
            skLineSegment(sketch, "E43.42.0.18", {"start": v(177.4, -23.72) * mm, "end": v(177.42, -23.73) * mm});
            skArc(sketch, "E43.43.0.0", {"start": v(172.12, -22.45) * mm, "mid": v(172.35, -22.98) * mm, "end": v(172.63, -23.48) * mm});
            skPoint(sketch, "E43.43.0.1", {"position": v(172.06, -20.63) * mm});
            skLineSegment(sketch, "E43.43.0.2", {"start": v(172, -21.8) * mm, "end": v(172.02, -21.55) * mm});
            skPoint(sketch, "E43.43.0.3", {"position": v(174.15, -22.11) * mm});
            skPoint(sketch, "E43.43.0.4", {"position": v(173.35, -23.73) * mm});
            skArc(sketch, "E43.43.0.5", {"start": v(174.03, -22.45) * mm, "mid": v(173.8, -22.98) * mm, "end": v(173.51, -23.48) * mm});
            skPoint(sketch, "E43.43.0.6", {"position": v(172, -22.11) * mm});
            skLineSegment(sketch, "E43.43.0.7", {"start": v(174.14, -21.8) * mm, "end": v(174.13, -21.55) * mm});
            skPoint(sketch, "E43.43.0.8", {"position": v(172.79, -23.72) * mm});
            skArc(sketch, "E43.43.0.9", {"start": v(172.02, -21.55) * mm, "mid": v(171.8, -20.97) * mm, "end": v(171.23, -20.73) * mm});
            skLineSegment(sketch, "E43.43.0.10", {"start": v(174.91, -20.73) * mm, "end": v(174.17, -20.73) * mm});
            skArc(sketch, "E43.43.0.11", {"start": v(174.03, -22.45) * mm, "mid": v(174.12, -22.13) * mm, "end": v(174.14, -21.8) * mm});
            skArc(sketch, "E43.43.0.12", {"start": v(172, -21.8) * mm, "mid": v(172.03, -22.13) * mm, "end": v(172.12, -22.45) * mm});
            skPoint(sketch, "E43.43.0.13", {"position": v(173.16, -23.73) * mm});
            skArc(sketch, "E43.43.0.14", {"start": v(172.63, -23.48) * mm, "mid": v(172.82, -23.66) * mm, "end": v(173.06, -23.72) * mm});
            skArc(sketch, "E43.43.0.15", {"start": v(174.91, -20.73) * mm, "mid": v(174.34, -20.97) * mm, "end": v(174.13, -21.55) * mm});
            skArc(sketch, "E43.43.0.16", {"start": v(173.07, -23.73) * mm, "mid": v(173.32, -23.66) * mm, "end": v(173.51, -23.48) * mm});
            skLineSegment(sketch, "E43.43.0.17", {"start": v(173.07, -23.73) * mm, "end": v(173.06, -23.72) * mm});
            skLineSegment(sketch, "E43.43.0.18", {"start": v(173.06, -23.72) * mm, "end": v(173.07, -23.73) * mm});
            skArc(sketch, "E43.44.0.0", {"start": v(167.78, -22.45) * mm, "mid": v(168.01, -22.98) * mm, "end": v(168.3, -23.48) * mm});
            skPoint(sketch, "E43.44.0.1", {"position": v(167.71, -20.63) * mm});
            skLineSegment(sketch, "E43.44.0.2", {"start": v(167.66, -21.8) * mm, "end": v(167.67, -21.55) * mm});
            skPoint(sketch, "E43.44.0.3", {"position": v(169.8, -22.11) * mm});
            skPoint(sketch, "E43.44.0.4", {"position": v(169.01, -23.73) * mm});
            skArc(sketch, "E43.44.0.5", {"start": v(169.68, -22.45) * mm, "mid": v(169.45, -22.98) * mm, "end": v(169.17, -23.48) * mm});
            skPoint(sketch, "E43.44.0.6", {"position": v(167.65, -22.11) * mm});
            skLineSegment(sketch, "E43.44.0.7", {"start": v(169.8, -21.8) * mm, "end": v(169.78, -21.55) * mm});
            skPoint(sketch, "E43.44.0.8", {"position": v(168.44, -23.72) * mm});
            skArc(sketch, "E43.44.0.9", {"start": v(167.67, -21.55) * mm, "mid": v(167.46, -20.97) * mm, "end": v(166.89, -20.73) * mm});
            skLineSegment(sketch, "E43.44.0.10", {"start": v(170.57, -20.73) * mm, "end": v(169.82, -20.73) * mm});
            skArc(sketch, "E43.44.0.11", {"start": v(169.68, -22.45) * mm, "mid": v(169.77, -22.13) * mm, "end": v(169.8, -21.8) * mm});
            skArc(sketch, "E43.44.0.12", {"start": v(167.66, -21.8) * mm, "mid": v(167.68, -22.13) * mm, "end": v(167.78, -22.45) * mm});
            skPoint(sketch, "E43.44.0.13", {"position": v(168.82, -23.73) * mm});
            skArc(sketch, "E43.44.0.14", {"start": v(168.3, -23.48) * mm, "mid": v(168.47, -23.66) * mm, "end": v(168.72, -23.72) * mm});
            skArc(sketch, "E43.44.0.15", {"start": v(170.57, -20.73) * mm, "mid": v(170, -20.97) * mm, "end": v(169.78, -21.55) * mm});
            skArc(sketch, "E43.44.0.16", {"start": v(168.73, -23.73) * mm, "mid": v(168.98, -23.66) * mm, "end": v(169.17, -23.48) * mm});
            skLineSegment(sketch, "E43.44.0.17", {"start": v(168.73, -23.73) * mm, "end": v(168.72, -23.72) * mm});
            skLineSegment(sketch, "E43.44.0.18", {"start": v(168.72, -23.72) * mm, "end": v(168.73, -23.73) * mm});
            skArc(sketch, "E43.45.0.0", {"start": v(163.43, -22.45) * mm, "mid": v(163.67, -22.98) * mm, "end": v(163.95, -23.48) * mm});
            skPoint(sketch, "E43.45.0.1", {"position": v(163.37, -20.63) * mm});
            skLineSegment(sketch, "E43.45.0.2", {"start": v(163.32, -21.8) * mm, "end": v(163.33, -21.55) * mm});
            skPoint(sketch, "E43.45.0.3", {"position": v(165.47, -22.11) * mm});
            skPoint(sketch, "E43.45.0.4", {"position": v(164.67, -23.73) * mm});
            skArc(sketch, "E43.45.0.5", {"start": v(165.34, -22.45) * mm, "mid": v(165.1, -22.98) * mm, "end": v(164.83, -23.48) * mm});
            skPoint(sketch, "E43.45.0.6", {"position": v(163.3, -22.11) * mm});
            skLineSegment(sketch, "E43.45.0.7", {"start": v(165.45, -21.8) * mm, "end": v(165.44, -21.55) * mm});
            skPoint(sketch, "E43.45.0.8", {"position": v(164.1, -23.72) * mm});
            skArc(sketch, "E43.45.0.9", {"start": v(163.33, -21.55) * mm, "mid": v(163.11, -20.97) * mm, "end": v(162.54, -20.73) * mm});
            skLineSegment(sketch, "E43.45.0.10", {"start": v(166.23, -20.73) * mm, "end": v(165.48, -20.73) * mm});
            skArc(sketch, "E43.45.0.11", {"start": v(165.34, -22.45) * mm, "mid": v(165.43, -22.13) * mm, "end": v(165.45, -21.8) * mm});
            skArc(sketch, "E43.45.0.12", {"start": v(163.32, -21.8) * mm, "mid": v(163.34, -22.13) * mm, "end": v(163.43, -22.45) * mm});
            skPoint(sketch, "E43.45.0.13", {"position": v(164.48, -23.73) * mm});
            skArc(sketch, "E43.45.0.14", {"start": v(163.95, -23.48) * mm, "mid": v(164.13, -23.66) * mm, "end": v(164.37, -23.72) * mm});
            skArc(sketch, "E43.45.0.15", {"start": v(166.23, -20.73) * mm, "mid": v(165.66, -20.97) * mm, "end": v(165.44, -21.55) * mm});
            skArc(sketch, "E43.45.0.16", {"start": v(164.39, -23.73) * mm, "mid": v(164.64, -23.66) * mm, "end": v(164.83, -23.48) * mm});
            skLineSegment(sketch, "E43.45.0.17", {"start": v(164.39, -23.73) * mm, "end": v(164.37, -23.72) * mm});
            skLineSegment(sketch, "E43.45.0.18", {"start": v(164.37, -23.72) * mm, "end": v(164.39, -23.73) * mm});
            skArc(sketch, "E43.46.0.0", {"start": v(159.09, -22.45) * mm, "mid": v(159.32, -22.98) * mm, "end": v(159.6, -23.48) * mm});
            skPoint(sketch, "E43.46.0.1", {"position": v(159.03, -20.63) * mm});
            skLineSegment(sketch, "E43.46.0.2", {"start": v(158.98, -21.8) * mm, "end": v(158.99, -21.55) * mm});
            skPoint(sketch, "E43.46.0.3", {"position": v(161.12, -22.11) * mm});
            skPoint(sketch, "E43.46.0.4", {"position": v(160.32, -23.73) * mm});
            skArc(sketch, "E43.46.0.5", {"start": v(161, -22.45) * mm, "mid": v(160.76, -22.98) * mm, "end": v(160.48, -23.48) * mm});
            skPoint(sketch, "E43.46.0.6", {"position": v(158.96, -22.11) * mm});
            skLineSegment(sketch, "E43.46.0.7", {"start": v(161.1, -21.8) * mm, "end": v(161.1, -21.55) * mm});
            skPoint(sketch, "E43.46.0.8", {"position": v(159.76, -23.72) * mm});
            skArc(sketch, "E43.46.0.9", {"start": v(158.99, -21.55) * mm, "mid": v(158.77, -20.97) * mm, "end": v(158.2, -20.73) * mm});
            skLineSegment(sketch, "E43.46.0.10", {"start": v(161.88, -20.73) * mm, "end": v(161.14, -20.73) * mm});
            skArc(sketch, "E43.46.0.11", {"start": v(161, -22.45) * mm, "mid": v(161.09, -22.13) * mm, "end": v(161.1, -21.8) * mm});
            skArc(sketch, "E43.46.0.12", {"start": v(158.98, -21.8) * mm, "mid": v(159, -22.13) * mm, "end": v(159.09, -22.45) * mm});
            skPoint(sketch, "E43.46.0.13", {"position": v(160.13, -23.73) * mm});
            skArc(sketch, "E43.46.0.14", {"start": v(159.6, -23.48) * mm, "mid": v(159.79, -23.66) * mm, "end": v(160.03, -23.72) * mm});
            skArc(sketch, "E43.46.0.15", {"start": v(161.88, -20.73) * mm, "mid": v(161.31, -20.97) * mm, "end": v(161.1, -21.55) * mm});
            skArc(sketch, "E43.46.0.16", {"start": v(160.04, -23.73) * mm, "mid": v(160.3, -23.66) * mm, "end": v(160.48, -23.48) * mm});
            skLineSegment(sketch, "E43.46.0.17", {"start": v(160.04, -23.73) * mm, "end": v(160.03, -23.72) * mm});
            skLineSegment(sketch, "E43.46.0.18", {"start": v(160.03, -23.72) * mm, "end": v(160.04, -23.73) * mm});
            skArc(sketch, "E43.47.0.0", {"start": v(154.74, -22.45) * mm, "mid": v(154.98, -22.98) * mm, "end": v(155.26, -23.48) * mm});
            skPoint(sketch, "E43.47.0.1", {"position": v(154.68, -20.63) * mm});
            skLineSegment(sketch, "E43.47.0.2", {"start": v(154.63, -21.8) * mm, "end": v(154.64, -21.55) * mm});
            skPoint(sketch, "E43.47.0.3", {"position": v(156.78, -22.11) * mm});
            skPoint(sketch, "E43.47.0.4", {"position": v(155.98, -23.73) * mm});
            skArc(sketch, "E43.47.0.5", {"start": v(156.65, -22.45) * mm, "mid": v(156.42, -22.98) * mm, "end": v(156.14, -23.48) * mm});
            skPoint(sketch, "E43.47.0.6", {"position": v(154.62, -22.11) * mm});
            skLineSegment(sketch, "E43.47.0.7", {"start": v(156.76, -21.8) * mm, "end": v(156.75, -21.55) * mm});
            skPoint(sketch, "E43.47.0.8", {"position": v(155.41, -23.72) * mm});
            skArc(sketch, "E43.47.0.9", {"start": v(154.64, -21.55) * mm, "mid": v(154.43, -20.97) * mm, "end": v(153.86, -20.73) * mm});
            skLineSegment(sketch, "E43.47.0.10", {"start": v(157.54, -20.73) * mm, "end": v(156.8, -20.73) * mm});
            skArc(sketch, "E43.47.0.11", {"start": v(156.65, -22.45) * mm, "mid": v(156.74, -22.13) * mm, "end": v(156.76, -21.8) * mm});
            skArc(sketch, "E43.47.0.12", {"start": v(154.63, -21.8) * mm, "mid": v(154.65, -22.13) * mm, "end": v(154.74, -22.45) * mm});
            skPoint(sketch, "E43.47.0.13", {"position": v(155.79, -23.73) * mm});
            skArc(sketch, "E43.47.0.14", {"start": v(155.26, -23.48) * mm, "mid": v(155.44, -23.66) * mm, "end": v(155.69, -23.72) * mm});
            skArc(sketch, "E43.47.0.15", {"start": v(157.54, -20.73) * mm, "mid": v(156.97, -20.97) * mm, "end": v(156.75, -21.55) * mm});
            skArc(sketch, "E43.47.0.16", {"start": v(155.7, -23.73) * mm, "mid": v(155.95, -23.66) * mm, "end": v(156.14, -23.48) * mm});
            skLineSegment(sketch, "E43.47.0.17", {"start": v(155.7, -23.73) * mm, "end": v(155.69, -23.72) * mm});
            skLineSegment(sketch, "E43.47.0.18", {"start": v(155.69, -23.72) * mm, "end": v(155.7, -23.73) * mm});
            skArc(sketch, "E43.48.0.0", {"start": v(150.4, -22.45) * mm, "mid": v(150.64, -22.98) * mm, "end": v(150.92, -23.48) * mm});
            skPoint(sketch, "E43.48.0.1", {"position": v(150.34, -20.63) * mm});
            skLineSegment(sketch, "E43.48.0.2", {"start": v(150.29, -21.8) * mm, "end": v(150.3, -21.55) * mm});
            skPoint(sketch, "E43.48.0.3", {"position": v(152.44, -22.11) * mm});
            skPoint(sketch, "E43.48.0.4", {"position": v(151.64, -23.73) * mm});
            skArc(sketch, "E43.48.0.5", {"start": v(152.31, -22.45) * mm, "mid": v(152.07, -22.98) * mm, "end": v(151.8, -23.48) * mm});
            skPoint(sketch, "E43.48.0.6", {"position": v(150.28, -22.11) * mm});
            skLineSegment(sketch, "E43.48.0.7", {"start": v(152.42, -21.8) * mm, "end": v(152.41, -21.55) * mm});
            skPoint(sketch, "E43.48.0.8", {"position": v(151.07, -23.72) * mm});
            skArc(sketch, "E43.48.0.9", {"start": v(150.3, -21.55) * mm, "mid": v(150.08, -20.97) * mm, "end": v(149.51, -20.73) * mm});
            skLineSegment(sketch, "E43.48.0.10", {"start": v(153.2, -20.73) * mm, "end": v(152.45, -20.73) * mm});
            skArc(sketch, "E43.48.0.11", {"start": v(152.31, -22.45) * mm, "mid": v(152.4, -22.13) * mm, "end": v(152.42, -21.8) * mm});
            skArc(sketch, "E43.48.0.12", {"start": v(150.29, -21.8) * mm, "mid": v(150.31, -22.13) * mm, "end": v(150.4, -22.45) * mm});
            skPoint(sketch, "E43.48.0.13", {"position": v(151.45, -23.73) * mm});
            skArc(sketch, "E43.48.0.14", {"start": v(150.92, -23.48) * mm, "mid": v(151.1, -23.66) * mm, "end": v(151.34, -23.72) * mm});
            skArc(sketch, "E43.48.0.15", {"start": v(153.2, -20.73) * mm, "mid": v(152.63, -20.97) * mm, "end": v(152.41, -21.55) * mm});
            skArc(sketch, "E43.48.0.16", {"start": v(151.36, -23.73) * mm, "mid": v(151.6, -23.66) * mm, "end": v(151.8, -23.48) * mm});
            skLineSegment(sketch, "E43.48.0.17", {"start": v(151.36, -23.73) * mm, "end": v(151.34, -23.72) * mm});
            skLineSegment(sketch, "E43.48.0.18", {"start": v(151.34, -23.72) * mm, "end": v(151.36, -23.73) * mm});
            skArc(sketch, "E43.49.0.0", {"start": v(146.06, -22.45) * mm, "mid": v(146.3, -22.98) * mm, "end": v(146.57, -23.48) * mm});
            skPoint(sketch, "E43.49.0.1", {"position": v(146, -20.63) * mm});
            skLineSegment(sketch, "E43.49.0.2", {"start": v(145.95, -21.8) * mm, "end": v(145.96, -21.55) * mm});
            skPoint(sketch, "E43.49.0.3", {"position": v(148.1, -22.11) * mm});
            skPoint(sketch, "E43.49.0.4", {"position": v(147.3, -23.73) * mm});
            skArc(sketch, "E43.49.0.5", {"start": v(147.97, -22.45) * mm, "mid": v(147.73, -22.98) * mm, "end": v(147.45, -23.48) * mm});
            skPoint(sketch, "E43.49.0.6", {"position": v(145.93, -22.11) * mm});
            skLineSegment(sketch, "E43.49.0.7", {"start": v(148.08, -21.8) * mm, "end": v(148.07, -21.55) * mm});
            skPoint(sketch, "E43.49.0.8", {"position": v(146.73, -23.72) * mm});
            skArc(sketch, "E43.49.0.9", {"start": v(145.96, -21.55) * mm, "mid": v(145.74, -20.97) * mm, "end": v(145.17, -20.73) * mm});
            skLineSegment(sketch, "E43.49.0.10", {"start": v(148.85, -20.73) * mm, "end": v(148.1, -20.73) * mm});
            skArc(sketch, "E43.49.0.11", {"start": v(147.97, -22.45) * mm, "mid": v(148.06, -22.13) * mm, "end": v(148.08, -21.8) * mm});
            skArc(sketch, "E43.49.0.12", {"start": v(145.95, -21.8) * mm, "mid": v(145.97, -22.13) * mm, "end": v(146.06, -22.45) * mm});
            skPoint(sketch, "E43.49.0.13", {"position": v(147.1, -23.73) * mm});
            skArc(sketch, "E43.49.0.14", {"start": v(146.57, -23.48) * mm, "mid": v(146.76, -23.66) * mm, "end": v(147, -23.72) * mm});
            skArc(sketch, "E43.49.0.15", {"start": v(148.85, -20.73) * mm, "mid": v(148.28, -20.97) * mm, "end": v(148.07, -21.55) * mm});
            skArc(sketch, "E43.49.0.16", {"start": v(147.01, -23.73) * mm, "mid": v(147.26, -23.66) * mm, "end": v(147.45, -23.48) * mm});
            skLineSegment(sketch, "E43.49.0.17", {"start": v(147.01, -23.73) * mm, "end": v(147, -23.72) * mm});
            skLineSegment(sketch, "E43.49.0.18", {"start": v(147, -23.72) * mm, "end": v(147.01, -23.73) * mm});
            skArc(sketch, "E43.50.0.0", {"start": v(141.71, -22.45) * mm, "mid": v(141.95, -22.98) * mm, "end": v(142.23, -23.48) * mm});
            skPoint(sketch, "E43.50.0.1", {"position": v(141.65, -20.63) * mm});
            skLineSegment(sketch, "E43.50.0.2", {"start": v(141.6, -21.8) * mm, "end": v(141.61, -21.55) * mm});
            skPoint(sketch, "E43.50.0.3", {"position": v(143.75, -22.11) * mm});
            skPoint(sketch, "E43.50.0.4", {"position": v(142.95, -23.73) * mm});
            skArc(sketch, "E43.50.0.5", {"start": v(143.62, -22.45) * mm, "mid": v(143.39, -22.98) * mm, "end": v(143.1, -23.48) * mm});
            skPoint(sketch, "E43.50.0.6", {"position": v(141.59, -22.11) * mm});
            skLineSegment(sketch, "E43.50.0.7", {"start": v(143.73, -21.8) * mm, "end": v(143.72, -21.55) * mm});
            skPoint(sketch, "E43.50.0.8", {"position": v(142.38, -23.72) * mm});
            skArc(sketch, "E43.50.0.9", {"start": v(141.61, -21.55) * mm, "mid": v(141.4, -20.97) * mm, "end": v(140.83, -20.73) * mm});
            skLineSegment(sketch, "E43.50.0.10", {"start": v(144.51, -20.73) * mm, "end": v(143.76, -20.73) * mm});
            skArc(sketch, "E43.50.0.11", {"start": v(143.62, -22.45) * mm, "mid": v(143.71, -22.13) * mm, "end": v(143.73, -21.8) * mm});
            skArc(sketch, "E43.50.0.12", {"start": v(141.6, -21.8) * mm, "mid": v(141.62, -22.13) * mm, "end": v(141.71, -22.45) * mm});
            skPoint(sketch, "E43.50.0.13", {"position": v(142.76, -23.73) * mm});
            skArc(sketch, "E43.50.0.14", {"start": v(142.23, -23.48) * mm, "mid": v(142.41, -23.66) * mm, "end": v(142.66, -23.72) * mm});
            skArc(sketch, "E43.50.0.15", {"start": v(144.51, -20.73) * mm, "mid": v(143.94, -20.97) * mm, "end": v(143.72, -21.55) * mm});
            skArc(sketch, "E43.50.0.16", {"start": v(142.67, -23.73) * mm, "mid": v(142.92, -23.66) * mm, "end": v(143.1, -23.48) * mm});
            skLineSegment(sketch, "E43.50.0.17", {"start": v(142.67, -23.73) * mm, "end": v(142.66, -23.72) * mm});
            skLineSegment(sketch, "E43.50.0.18", {"start": v(142.66, -23.72) * mm, "end": v(142.67, -23.73) * mm});
            skArc(sketch, "E43.51.0.0", {"start": v(137.37, -22.45) * mm, "mid": v(137.6, -22.98) * mm, "end": v(137.89, -23.48) * mm});
            skPoint(sketch, "E43.51.0.1", {"position": v(137.3, -20.63) * mm});
            skLineSegment(sketch, "E43.51.0.2", {"start": v(137.26, -21.8) * mm, "end": v(137.27, -21.55) * mm});
            skPoint(sketch, "E43.51.0.3", {"position": v(139.4, -22.11) * mm});
            skPoint(sketch, "E43.51.0.4", {"position": v(138.6, -23.73) * mm});
            skArc(sketch, "E43.51.0.5", {"start": v(139.28, -22.45) * mm, "mid": v(139.04, -22.98) * mm, "end": v(138.77, -23.48) * mm});
            skPoint(sketch, "E43.51.0.6", {"position": v(137.25, -22.11) * mm});
            skLineSegment(sketch, "E43.51.0.7", {"start": v(139.4, -21.8) * mm, "end": v(139.38, -21.55) * mm});
            skPoint(sketch, "E43.51.0.8", {"position": v(138.04, -23.72) * mm});
            skArc(sketch, "E43.51.0.9", {"start": v(137.27, -21.55) * mm, "mid": v(137.05, -20.97) * mm, "end": v(136.48, -20.73) * mm});
            skLineSegment(sketch, "E43.51.0.10", {"start": v(140.17, -20.73) * mm, "end": v(139.42, -20.73) * mm});
            skArc(sketch, "E43.51.0.11", {"start": v(139.28, -22.45) * mm, "mid": v(139.37, -22.13) * mm, "end": v(139.4, -21.8) * mm});
            skArc(sketch, "E43.51.0.12", {"start": v(137.26, -21.8) * mm, "mid": v(137.28, -22.13) * mm, "end": v(137.37, -22.45) * mm});
            skPoint(sketch, "E43.51.0.13", {"position": v(138.42, -23.73) * mm});
            skArc(sketch, "E43.51.0.14", {"start": v(137.89, -23.48) * mm, "mid": v(138.07, -23.66) * mm, "end": v(138.31, -23.72) * mm});
            skArc(sketch, "E43.51.0.15", {"start": v(140.17, -20.73) * mm, "mid": v(139.6, -20.97) * mm, "end": v(139.38, -21.55) * mm});
            skArc(sketch, "E43.51.0.16", {"start": v(138.33, -23.73) * mm, "mid": v(138.58, -23.66) * mm, "end": v(138.77, -23.48) * mm});
            skLineSegment(sketch, "E43.51.0.17", {"start": v(138.33, -23.73) * mm, "end": v(138.31, -23.72) * mm});
            skLineSegment(sketch, "E43.51.0.18", {"start": v(138.31, -23.72) * mm, "end": v(138.33, -23.73) * mm});
            skArc(sketch, "E43.52.0.0", {"start": v(133.03, -22.45) * mm, "mid": v(133.26, -22.98) * mm, "end": v(133.54, -23.48) * mm});
            skPoint(sketch, "E43.52.0.1", {"position": v(132.97, -20.63) * mm});
            skLineSegment(sketch, "E43.52.0.2", {"start": v(132.92, -21.8) * mm, "end": v(132.93, -21.55) * mm});
            skPoint(sketch, "E43.52.0.3", {"position": v(135.06, -22.11) * mm});
            skPoint(sketch, "E43.52.0.4", {"position": v(134.26, -23.73) * mm});
            skArc(sketch, "E43.52.0.5", {"start": v(134.94, -22.45) * mm, "mid": v(134.7, -22.98) * mm, "end": v(134.42, -23.48) * mm});
            skPoint(sketch, "E43.52.0.6", {"position": v(132.9, -22.11) * mm});
            skLineSegment(sketch, "E43.52.0.7", {"start": v(135.05, -21.8) * mm, "end": v(135.04, -21.55) * mm});
            skPoint(sketch, "E43.52.0.8", {"position": v(133.7, -23.72) * mm});
            skArc(sketch, "E43.52.0.9", {"start": v(132.93, -21.55) * mm, "mid": v(132.7, -20.97) * mm, "end": v(132.14, -20.73) * mm});
            skLineSegment(sketch, "E43.52.0.10", {"start": v(135.82, -20.73) * mm, "end": v(135.08, -20.73) * mm});
            skArc(sketch, "E43.52.0.11", {"start": v(134.94, -22.45) * mm, "mid": v(135.03, -22.13) * mm, "end": v(135.05, -21.8) * mm});
            skArc(sketch, "E43.52.0.12", {"start": v(132.92, -21.8) * mm, "mid": v(132.94, -22.13) * mm, "end": v(133.03, -22.45) * mm});
            skPoint(sketch, "E43.52.0.13", {"position": v(134.07, -23.73) * mm});
            skArc(sketch, "E43.52.0.14", {"start": v(133.54, -23.48) * mm, "mid": v(133.73, -23.66) * mm, "end": v(133.97, -23.72) * mm});
            skArc(sketch, "E43.52.0.15", {"start": v(135.82, -20.73) * mm, "mid": v(135.25, -20.97) * mm, "end": v(135.04, -21.55) * mm});
            skArc(sketch, "E43.52.0.16", {"start": v(133.98, -23.73) * mm, "mid": v(134.23, -23.66) * mm, "end": v(134.42, -23.48) * mm});
            skLineSegment(sketch, "E43.52.0.17", {"start": v(133.98, -23.73) * mm, "end": v(133.97, -23.72) * mm});
            skLineSegment(sketch, "E43.52.0.18", {"start": v(133.97, -23.72) * mm, "end": v(133.98, -23.73) * mm});
            skArc(sketch, "E43.53.0.0", {"start": v(128.68, -22.45) * mm, "mid": v(128.92, -22.98) * mm, "end": v(129.2, -23.48) * mm});
            skPoint(sketch, "E43.53.0.1", {"position": v(128.62, -20.63) * mm});
            skLineSegment(sketch, "E43.53.0.2", {"start": v(128.57, -21.8) * mm, "end": v(128.58, -21.55) * mm});
            skPoint(sketch, "E43.53.0.3", {"position": v(130.72, -22.11) * mm});
            skPoint(sketch, "E43.53.0.4", {"position": v(129.92, -23.73) * mm});
            skArc(sketch, "E43.53.0.5", {"start": v(130.6, -22.45) * mm, "mid": v(130.36, -22.98) * mm, "end": v(130.08, -23.48) * mm});
            skPoint(sketch, "E43.53.0.6", {"position": v(128.56, -22.11) * mm});
            skLineSegment(sketch, "E43.53.0.7", {"start": v(130.7, -21.8) * mm, "end": v(130.7, -21.55) * mm});
            skPoint(sketch, "E43.53.0.8", {"position": v(129.35, -23.72) * mm});
            skArc(sketch, "E43.53.0.9", {"start": v(128.58, -21.55) * mm, "mid": v(128.37, -20.97) * mm, "end": v(127.8, -20.73) * mm});
            skLineSegment(sketch, "E43.53.0.10", {"start": v(131.48, -20.73) * mm, "end": v(130.73, -20.73) * mm});
            skArc(sketch, "E43.53.0.11", {"start": v(130.6, -22.45) * mm, "mid": v(130.68, -22.13) * mm, "end": v(130.7, -21.8) * mm});
            skArc(sketch, "E43.53.0.12", {"start": v(128.57, -21.8) * mm, "mid": v(128.6, -22.13) * mm, "end": v(128.68, -22.45) * mm});
            skPoint(sketch, "E43.53.0.13", {"position": v(129.73, -23.73) * mm});
            skArc(sketch, "E43.53.0.14", {"start": v(129.2, -23.48) * mm, "mid": v(129.38, -23.66) * mm, "end": v(129.63, -23.72) * mm});
            skArc(sketch, "E43.53.0.15", {"start": v(131.48, -20.73) * mm, "mid": v(130.91, -20.97) * mm, "end": v(130.7, -21.55) * mm});
            skArc(sketch, "E43.53.0.16", {"start": v(129.64, -23.73) * mm, "mid": v(129.9, -23.66) * mm, "end": v(130.08, -23.48) * mm});
            skLineSegment(sketch, "E43.53.0.17", {"start": v(129.64, -23.73) * mm, "end": v(129.63, -23.72) * mm});
            skLineSegment(sketch, "E43.53.0.18", {"start": v(129.63, -23.72) * mm, "end": v(129.64, -23.73) * mm});
            skArc(sketch, "E43.54.0.0", {"start": v(124.34, -22.45) * mm, "mid": v(124.58, -22.98) * mm, "end": v(124.86, -23.48) * mm});
            skPoint(sketch, "E43.54.0.1", {"position": v(124.28, -20.63) * mm});
            skLineSegment(sketch, "E43.54.0.2", {"start": v(124.23, -21.8) * mm, "end": v(124.24, -21.55) * mm});
            skPoint(sketch, "E43.54.0.3", {"position": v(126.37, -22.11) * mm});
            skPoint(sketch, "E43.54.0.4", {"position": v(125.58, -23.73) * mm});
            skArc(sketch, "E43.54.0.5", {"start": v(126.25, -22.45) * mm, "mid": v(126.01, -22.98) * mm, "end": v(125.74, -23.48) * mm});
            skPoint(sketch, "E43.54.0.6", {"position": v(124.22, -22.11) * mm});
            skLineSegment(sketch, "E43.54.0.7", {"start": v(126.36, -21.8) * mm, "end": v(126.35, -21.55) * mm});
            skPoint(sketch, "E43.54.0.8", {"position": v(125.01, -23.72) * mm});
            skArc(sketch, "E43.54.0.9", {"start": v(124.24, -21.55) * mm, "mid": v(124.02, -20.97) * mm, "end": v(123.45, -20.73) * mm});
            skLineSegment(sketch, "E43.54.0.10", {"start": v(127.14, -20.73) * mm, "end": v(126.4, -20.73) * mm});
            skArc(sketch, "E43.54.0.11", {"start": v(126.25, -22.45) * mm, "mid": v(126.34, -22.13) * mm, "end": v(126.36, -21.8) * mm});
            skArc(sketch, "E43.54.0.12", {"start": v(124.23, -21.8) * mm, "mid": v(124.25, -22.13) * mm, "end": v(124.34, -22.45) * mm});
            skPoint(sketch, "E43.54.0.13", {"position": v(125.39, -23.73) * mm});
            skArc(sketch, "E43.54.0.14", {"start": v(124.86, -23.48) * mm, "mid": v(125.04, -23.66) * mm, "end": v(125.28, -23.72) * mm});
            skArc(sketch, "E43.54.0.15", {"start": v(127.14, -20.73) * mm, "mid": v(126.57, -20.97) * mm, "end": v(126.35, -21.55) * mm});
            skArc(sketch, "E43.54.0.16", {"start": v(125.3, -23.73) * mm, "mid": v(125.55, -23.66) * mm, "end": v(125.74, -23.48) * mm});
            skLineSegment(sketch, "E43.54.0.17", {"start": v(125.3, -23.73) * mm, "end": v(125.28, -23.72) * mm});
            skLineSegment(sketch, "E43.54.0.18", {"start": v(125.28, -23.72) * mm, "end": v(125.3, -23.73) * mm});
            skArc(sketch, "E43.55.0.0", {"start": v(120, -22.45) * mm, "mid": v(120.23, -22.98) * mm, "end": v(120.51, -23.48) * mm});
            skPoint(sketch, "E43.55.0.1", {"position": v(119.94, -20.63) * mm});
            skLineSegment(sketch, "E43.55.0.2", {"start": v(119.89, -21.8) * mm, "end": v(119.9, -21.55) * mm});
            skPoint(sketch, "E43.55.0.3", {"position": v(122.03, -22.11) * mm});
            skPoint(sketch, "E43.55.0.4", {"position": v(121.23, -23.73) * mm});
            skArc(sketch, "E43.55.0.5", {"start": v(121.9, -22.45) * mm, "mid": v(121.67, -22.98) * mm, "end": v(121.4, -23.48) * mm});
            skPoint(sketch, "E43.55.0.6", {"position": v(119.87, -22.11) * mm});
            skLineSegment(sketch, "E43.55.0.7", {"start": v(122.02, -21.8) * mm, "end": v(122, -21.55) * mm});
            skPoint(sketch, "E43.55.0.8", {"position": v(120.67, -23.72) * mm});
            skArc(sketch, "E43.55.0.9", {"start": v(119.9, -21.55) * mm, "mid": v(119.68, -20.97) * mm, "end": v(119.1, -20.73) * mm});
            skLineSegment(sketch, "E43.55.0.10", {"start": v(122.8, -20.73) * mm, "end": v(122.05, -20.73) * mm});
            skArc(sketch, "E43.55.0.11", {"start": v(121.9, -22.45) * mm, "mid": v(122, -22.13) * mm, "end": v(122.02, -21.8) * mm});
            skArc(sketch, "E43.55.0.12", {"start": v(119.89, -21.8) * mm, "mid": v(119.9, -22.13) * mm, "end": v(120, -22.45) * mm});
            skPoint(sketch, "E43.55.0.13", {"position": v(121.04, -23.73) * mm});
            skArc(sketch, "E43.55.0.14", {"start": v(120.51, -23.48) * mm, "mid": v(120.7, -23.66) * mm, "end": v(120.94, -23.72) * mm});
            skArc(sketch, "E43.55.0.15", {"start": v(122.8, -20.73) * mm, "mid": v(122.22, -20.97) * mm, "end": v(122, -21.55) * mm});
            skArc(sketch, "E43.55.0.16", {"start": v(120.95, -23.73) * mm, "mid": v(121.2, -23.66) * mm, "end": v(121.4, -23.48) * mm});
            skLineSegment(sketch, "E43.55.0.17", {"start": v(120.95, -23.73) * mm, "end": v(120.94, -23.72) * mm});
            skLineSegment(sketch, "E43.55.0.18", {"start": v(120.94, -23.72) * mm, "end": v(120.95, -23.73) * mm});
            skArc(sketch, "E43.56.0.0", {"start": v(115.65, -22.45) * mm, "mid": v(115.9, -22.98) * mm, "end": v(116.17, -23.48) * mm});
            skPoint(sketch, "E43.56.0.1", {"position": v(115.6, -20.63) * mm});
            skLineSegment(sketch, "E43.56.0.2", {"start": v(115.54, -21.8) * mm, "end": v(115.55, -21.55) * mm});
            skPoint(sketch, "E43.56.0.3", {"position": v(117.69, -22.11) * mm});
            skPoint(sketch, "E43.56.0.4", {"position": v(116.89, -23.73) * mm});
            skArc(sketch, "E43.56.0.5", {"start": v(117.56, -22.45) * mm, "mid": v(117.33, -22.98) * mm, "end": v(117.05, -23.48) * mm});
            skPoint(sketch, "E43.56.0.6", {"position": v(115.53, -22.11) * mm});
            skLineSegment(sketch, "E43.56.0.7", {"start": v(117.67, -21.8) * mm, "end": v(117.66, -21.55) * mm});
            skPoint(sketch, "E43.56.0.8", {"position": v(116.32, -23.72) * mm});
            skArc(sketch, "E43.56.0.9", {"start": v(115.55, -21.55) * mm, "mid": v(115.34, -20.97) * mm, "end": v(114.77, -20.73) * mm});
            skLineSegment(sketch, "E43.56.0.10", {"start": v(118.45, -20.73) * mm, "end": v(117.7, -20.73) * mm});
            skArc(sketch, "E43.56.0.11", {"start": v(117.56, -22.45) * mm, "mid": v(117.65, -22.13) * mm, "end": v(117.67, -21.8) * mm});
            skArc(sketch, "E43.56.0.12", {"start": v(115.54, -21.8) * mm, "mid": v(115.56, -22.13) * mm, "end": v(115.65, -22.45) * mm});
            skPoint(sketch, "E43.56.0.13", {"position": v(116.7, -23.73) * mm});
            skArc(sketch, "E43.56.0.14", {"start": v(116.17, -23.48) * mm, "mid": v(116.35, -23.66) * mm, "end": v(116.6, -23.72) * mm});
            skArc(sketch, "E43.56.0.15", {"start": v(118.45, -20.73) * mm, "mid": v(117.88, -20.97) * mm, "end": v(117.66, -21.55) * mm});
            skArc(sketch, "E43.56.0.16", {"start": v(116.6, -23.73) * mm, "mid": v(116.86, -23.66) * mm, "end": v(117.05, -23.48) * mm});
            skLineSegment(sketch, "E43.56.0.17", {"start": v(116.6, -23.73) * mm, "end": v(116.6, -23.72) * mm});
            skLineSegment(sketch, "E43.56.0.18", {"start": v(116.6, -23.72) * mm, "end": v(116.6, -23.73) * mm});
            skArc(sketch, "E43.57.0.0", {"start": v(111.31, -22.45) * mm, "mid": v(111.55, -22.98) * mm, "end": v(111.83, -23.48) * mm});
            skPoint(sketch, "E43.57.0.1", {"position": v(111.25, -20.63) * mm});
            skLineSegment(sketch, "E43.57.0.2", {"start": v(111.2, -21.8) * mm, "end": v(111.2, -21.55) * mm});
            skPoint(sketch, "E43.57.0.3", {"position": v(113.34, -22.11) * mm});
            skPoint(sketch, "E43.57.0.4", {"position": v(112.55, -23.73) * mm});
            skArc(sketch, "E43.57.0.5", {"start": v(113.22, -22.45) * mm, "mid": v(112.98, -22.98) * mm, "end": v(112.7, -23.48) * mm});
            skPoint(sketch, "E43.57.0.6", {"position": v(111.19, -22.11) * mm});
            skLineSegment(sketch, "E43.57.0.7", {"start": v(113.33, -21.8) * mm, "end": v(113.32, -21.55) * mm});
            skPoint(sketch, "E43.57.0.8", {"position": v(111.98, -23.72) * mm});
            skArc(sketch, "E43.57.0.9", {"start": v(111.2, -21.55) * mm, "mid": v(111, -20.97) * mm, "end": v(110.42, -20.73) * mm});
            skLineSegment(sketch, "E43.57.0.10", {"start": v(114.1, -20.73) * mm, "end": v(113.36, -20.73) * mm});
            skArc(sketch, "E43.57.0.11", {"start": v(113.22, -22.45) * mm, "mid": v(113.3, -22.13) * mm, "end": v(113.33, -21.8) * mm});
            skArc(sketch, "E43.57.0.12", {"start": v(111.2, -21.8) * mm, "mid": v(111.22, -22.13) * mm, "end": v(111.31, -22.45) * mm});
            skPoint(sketch, "E43.57.0.13", {"position": v(112.36, -23.73) * mm});
            skArc(sketch, "E43.57.0.14", {"start": v(111.83, -23.48) * mm, "mid": v(112, -23.66) * mm, "end": v(112.25, -23.72) * mm});
            skArc(sketch, "E43.57.0.15", {"start": v(114.1, -20.73) * mm, "mid": v(113.54, -20.97) * mm, "end": v(113.32, -21.55) * mm});
            skArc(sketch, "E43.57.0.16", {"start": v(112.27, -23.73) * mm, "mid": v(112.52, -23.66) * mm, "end": v(112.7, -23.48) * mm});
            skLineSegment(sketch, "E43.57.0.17", {"start": v(112.27, -23.73) * mm, "end": v(112.25, -23.72) * mm});
            skLineSegment(sketch, "E43.57.0.18", {"start": v(112.25, -23.72) * mm, "end": v(112.27, -23.73) * mm});
            skArc(sketch, "E43.58.0.0", {"start": v(106.97, -22.45) * mm, "mid": v(107.2, -22.98) * mm, "end": v(107.48, -23.48) * mm});
            skPoint(sketch, "E43.58.0.1", {"position": v(106.9, -20.63) * mm});
            skLineSegment(sketch, "E43.58.0.2", {"start": v(106.86, -21.8) * mm, "end": v(106.87, -21.55) * mm});
            skPoint(sketch, "E43.58.0.3", {"position": v(109, -22.11) * mm});
            skPoint(sketch, "E43.58.0.4", {"position": v(108.2, -23.73) * mm});
            skArc(sketch, "E43.58.0.5", {"start": v(108.88, -22.45) * mm, "mid": v(108.64, -22.98) * mm, "end": v(108.36, -23.48) * mm});
            skPoint(sketch, "E43.58.0.6", {"position": v(106.84, -22.11) * mm});
            skLineSegment(sketch, "E43.58.0.7", {"start": v(108.99, -21.8) * mm, "end": v(108.98, -21.55) * mm});
            skPoint(sketch, "E43.58.0.8", {"position": v(107.64, -23.72) * mm});
            skArc(sketch, "E43.58.0.9", {"start": v(106.87, -21.55) * mm, "mid": v(106.65, -20.97) * mm, "end": v(106.08, -20.73) * mm});
            skLineSegment(sketch, "E43.58.0.10", {"start": v(109.76, -20.73) * mm, "end": v(109.02, -20.73) * mm});
            skArc(sketch, "E43.58.0.11", {"start": v(108.88, -22.45) * mm, "mid": v(108.97, -22.13) * mm, "end": v(108.99, -21.8) * mm});
            skArc(sketch, "E43.58.0.12", {"start": v(106.86, -21.8) * mm, "mid": v(106.88, -22.13) * mm, "end": v(106.97, -22.45) * mm});
            skPoint(sketch, "E43.58.0.13", {"position": v(108.01, -23.73) * mm});
            skArc(sketch, "E43.58.0.14", {"start": v(107.48, -23.48) * mm, "mid": v(107.67, -23.66) * mm, "end": v(107.9, -23.72) * mm});
            skArc(sketch, "E43.58.0.15", {"start": v(109.76, -20.73) * mm, "mid": v(109.2, -20.97) * mm, "end": v(108.98, -21.55) * mm});
            skArc(sketch, "E43.58.0.16", {"start": v(107.92, -23.73) * mm, "mid": v(108.17, -23.66) * mm, "end": v(108.36, -23.48) * mm});
            skLineSegment(sketch, "E43.58.0.17", {"start": v(107.92, -23.73) * mm, "end": v(107.9, -23.72) * mm});
            skLineSegment(sketch, "E43.58.0.18", {"start": v(107.9, -23.72) * mm, "end": v(107.92, -23.73) * mm});
            skArc(sketch, "E43.59.0.0", {"start": v(102.62, -22.45) * mm, "mid": v(102.86, -22.98) * mm, "end": v(103.14, -23.48) * mm});
            skPoint(sketch, "E43.59.0.1", {"position": v(102.56, -20.63) * mm});
            skLineSegment(sketch, "E43.59.0.2", {"start": v(102.51, -21.8) * mm, "end": v(102.52, -21.55) * mm});
            skPoint(sketch, "E43.59.0.3", {"position": v(104.66, -22.11) * mm});
            skPoint(sketch, "E43.59.0.4", {"position": v(103.86, -23.73) * mm});
            skArc(sketch, "E43.59.0.5", {"start": v(104.53, -22.45) * mm, "mid": v(104.3, -22.98) * mm, "end": v(104.02, -23.48) * mm});
            skPoint(sketch, "E43.59.0.6", {"position": v(102.5, -22.11) * mm});
            skLineSegment(sketch, "E43.59.0.7", {"start": v(104.64, -21.8) * mm, "end": v(104.63, -21.55) * mm});
            skPoint(sketch, "E43.59.0.8", {"position": v(103.3, -23.72) * mm});
            skArc(sketch, "E43.59.0.9", {"start": v(102.52, -21.55) * mm, "mid": v(102.3, -20.97) * mm, "end": v(101.74, -20.73) * mm});
            skLineSegment(sketch, "E43.59.0.10", {"start": v(105.42, -20.73) * mm, "end": v(104.67, -20.73) * mm});
            skArc(sketch, "E43.59.0.11", {"start": v(104.53, -22.45) * mm, "mid": v(104.62, -22.13) * mm, "end": v(104.64, -21.8) * mm});
            skArc(sketch, "E43.59.0.12", {"start": v(102.51, -21.8) * mm, "mid": v(102.53, -22.13) * mm, "end": v(102.62, -22.45) * mm});
            skPoint(sketch, "E43.59.0.13", {"position": v(103.67, -23.73) * mm});
            skArc(sketch, "E43.59.0.14", {"start": v(103.14, -23.48) * mm, "mid": v(103.32, -23.66) * mm, "end": v(103.57, -23.72) * mm});
            skArc(sketch, "E43.59.0.15", {"start": v(105.42, -20.73) * mm, "mid": v(104.85, -20.97) * mm, "end": v(104.63, -21.55) * mm});
            skArc(sketch, "E43.59.0.16", {"start": v(103.58, -23.73) * mm, "mid": v(103.83, -23.66) * mm, "end": v(104.02, -23.48) * mm});
            skLineSegment(sketch, "E43.59.0.17", {"start": v(103.58, -23.73) * mm, "end": v(103.57, -23.72) * mm});
            skLineSegment(sketch, "E43.59.0.18", {"start": v(103.57, -23.72) * mm, "end": v(103.58, -23.73) * mm});
            skArc(sketch, "E43.60.0.0", {"start": v(98.28, -22.45) * mm, "mid": v(98.52, -22.98) * mm, "end": v(98.8, -23.48) * mm});
            skPoint(sketch, "E43.60.0.1", {"position": v(98.22, -20.63) * mm});
            skLineSegment(sketch, "E43.60.0.2", {"start": v(98.17, -21.8) * mm, "end": v(98.18, -21.55) * mm});
            skPoint(sketch, "E43.60.0.3", {"position": v(100.31, -22.11) * mm});
            skPoint(sketch, "E43.60.0.4", {"position": v(99.52, -23.73) * mm});
            skArc(sketch, "E43.60.0.5", {"start": v(100.19, -22.45) * mm, "mid": v(99.95, -22.98) * mm, "end": v(99.67, -23.48) * mm});
            skPoint(sketch, "E43.60.0.6", {"position": v(98.16, -22.11) * mm});
            skLineSegment(sketch, "E43.60.0.7", {"start": v(100.3, -21.8) * mm, "end": v(100.29, -21.55) * mm});
            skPoint(sketch, "E43.60.0.8", {"position": v(98.95, -23.72) * mm});
            skArc(sketch, "E43.60.0.9", {"start": v(98.18, -21.55) * mm, "mid": v(97.96, -20.97) * mm, "end": v(97.4, -20.73) * mm});
            skLineSegment(sketch, "E43.60.0.10", {"start": v(101.08, -20.73) * mm, "end": v(100.33, -20.73) * mm});
            skArc(sketch, "E43.60.0.11", {"start": v(100.19, -22.45) * mm, "mid": v(100.28, -22.13) * mm, "end": v(100.3, -21.8) * mm});
            skArc(sketch, "E43.60.0.12", {"start": v(98.17, -21.8) * mm, "mid": v(98.19, -22.13) * mm, "end": v(98.28, -22.45) * mm});
            skPoint(sketch, "E43.60.0.13", {"position": v(99.33, -23.73) * mm});
            skArc(sketch, "E43.60.0.14", {"start": v(98.8, -23.48) * mm, "mid": v(98.98, -23.66) * mm, "end": v(99.22, -23.72) * mm});
            skArc(sketch, "E43.60.0.15", {"start": v(101.08, -20.73) * mm, "mid": v(100.5, -20.97) * mm, "end": v(100.29, -21.55) * mm});
            skArc(sketch, "E43.60.0.16", {"start": v(99.23, -23.73) * mm, "mid": v(99.49, -23.66) * mm, "end": v(99.67, -23.48) * mm});
            skLineSegment(sketch, "E43.60.0.17", {"start": v(99.23, -23.73) * mm, "end": v(99.22, -23.72) * mm});
            skLineSegment(sketch, "E43.60.0.18", {"start": v(99.22, -23.72) * mm, "end": v(99.23, -23.73) * mm});
            skArc(sketch, "E43.61.0.0", {"start": v(93.94, -22.45) * mm, "mid": v(94.17, -22.98) * mm, "end": v(94.45, -23.48) * mm});
            skPoint(sketch, "E43.61.0.1", {"position": v(93.88, -20.63) * mm});
            skLineSegment(sketch, "E43.61.0.2", {"start": v(93.83, -21.8) * mm, "end": v(93.84, -21.55) * mm});
            skPoint(sketch, "E43.61.0.3", {"position": v(95.97, -22.11) * mm});
            skPoint(sketch, "E43.61.0.4", {"position": v(95.17, -23.73) * mm});
            skArc(sketch, "E43.61.0.5", {"start": v(95.85, -22.45) * mm, "mid": v(95.61, -22.98) * mm, "end": v(95.33, -23.48) * mm});
            skPoint(sketch, "E43.61.0.6", {"position": v(93.81, -22.11) * mm});
            skLineSegment(sketch, "E43.61.0.7", {"start": v(95.96, -21.8) * mm, "end": v(95.95, -21.55) * mm});
            skPoint(sketch, "E43.61.0.8", {"position": v(94.6, -23.72) * mm});
            skArc(sketch, "E43.61.0.9", {"start": v(93.84, -21.55) * mm, "mid": v(93.62, -20.97) * mm, "end": v(93.05, -20.73) * mm});
            skLineSegment(sketch, "E43.61.0.10", {"start": v(96.73, -20.73) * mm, "end": v(95.99, -20.73) * mm});
            skArc(sketch, "E43.61.0.11", {"start": v(95.85, -22.45) * mm, "mid": v(95.94, -22.13) * mm, "end": v(95.96, -21.8) * mm});
            skArc(sketch, "E43.61.0.12", {"start": v(93.83, -21.8) * mm, "mid": v(93.85, -22.13) * mm, "end": v(93.94, -22.45) * mm});
            skPoint(sketch, "E43.61.0.13", {"position": v(94.98, -23.73) * mm});
            skArc(sketch, "E43.61.0.14", {"start": v(94.45, -23.48) * mm, "mid": v(94.64, -23.66) * mm, "end": v(94.88, -23.72) * mm});
            skArc(sketch, "E43.61.0.15", {"start": v(96.73, -20.73) * mm, "mid": v(96.16, -20.97) * mm, "end": v(95.95, -21.55) * mm});
            skArc(sketch, "E43.61.0.16", {"start": v(94.9, -23.73) * mm, "mid": v(95.14, -23.66) * mm, "end": v(95.33, -23.48) * mm});
            skLineSegment(sketch, "E43.61.0.17", {"start": v(94.9, -23.73) * mm, "end": v(94.88, -23.72) * mm});
            skLineSegment(sketch, "E43.61.0.18", {"start": v(94.88, -23.72) * mm, "end": v(94.9, -23.73) * mm});
            skArc(sketch, "E43.62.0.0", {"start": v(89.6, -22.45) * mm, "mid": v(89.83, -22.98) * mm, "end": v(90.1, -23.48) * mm});
            skPoint(sketch, "E43.62.0.1", {"position": v(89.53, -20.63) * mm});
            skLineSegment(sketch, "E43.62.0.2", {"start": v(89.48, -21.8) * mm, "end": v(89.5, -21.55) * mm});
            skPoint(sketch, "E43.62.0.3", {"position": v(91.63, -22.11) * mm});
            skPoint(sketch, "E43.62.0.4", {"position": v(90.83, -23.73) * mm});
            skArc(sketch, "E43.62.0.5", {"start": v(91.5, -22.45) * mm, "mid": v(91.27, -22.98) * mm, "end": v(90.99, -23.48) * mm});
            skPoint(sketch, "E43.62.0.6", {"position": v(89.47, -22.11) * mm});
            skLineSegment(sketch, "E43.62.0.7", {"start": v(91.61, -21.8) * mm, "end": v(91.6, -21.55) * mm});
            skPoint(sketch, "E43.62.0.8", {"position": v(90.26, -23.72) * mm});
            skArc(sketch, "E43.62.0.9", {"start": v(89.5, -21.55) * mm, "mid": v(89.27, -20.97) * mm, "end": v(88.7, -20.73) * mm});
            skLineSegment(sketch, "E43.62.0.10", {"start": v(92.39, -20.73) * mm, "end": v(91.64, -20.73) * mm});
            skArc(sketch, "E43.62.0.11", {"start": v(91.5, -22.45) * mm, "mid": v(91.6, -22.13) * mm, "end": v(91.61, -21.8) * mm});
            skArc(sketch, "E43.62.0.12", {"start": v(89.48, -21.8) * mm, "mid": v(89.5, -22.13) * mm, "end": v(89.6, -22.45) * mm});
            skPoint(sketch, "E43.62.0.13", {"position": v(90.64, -23.73) * mm});
            skArc(sketch, "E43.62.0.14", {"start": v(90.1, -23.48) * mm, "mid": v(90.3, -23.66) * mm, "end": v(90.54, -23.72) * mm});
            skArc(sketch, "E43.62.0.15", {"start": v(92.39, -20.73) * mm, "mid": v(91.82, -20.97) * mm, "end": v(91.6, -21.55) * mm});
            skArc(sketch, "E43.62.0.16", {"start": v(90.55, -23.73) * mm, "mid": v(90.8, -23.66) * mm, "end": v(90.99, -23.48) * mm});
            skLineSegment(sketch, "E43.62.0.17", {"start": v(90.55, -23.73) * mm, "end": v(90.54, -23.72) * mm});
            skLineSegment(sketch, "E43.62.0.18", {"start": v(90.54, -23.72) * mm, "end": v(90.55, -23.73) * mm});
            skArc(sketch, "E43.63.0.0", {"start": v(85.25, -22.45) * mm, "mid": v(85.49, -22.98) * mm, "end": v(85.77, -23.48) * mm});
            skPoint(sketch, "E43.63.0.1", {"position": v(85.19, -20.63) * mm});
            skLineSegment(sketch, "E43.63.0.2", {"start": v(85.14, -21.8) * mm, "end": v(85.15, -21.55) * mm});
            skPoint(sketch, "E43.63.0.3", {"position": v(87.28, -22.11) * mm});
            skPoint(sketch, "E43.63.0.4", {"position": v(86.49, -23.73) * mm});
            skArc(sketch, "E43.63.0.5", {"start": v(87.16, -22.45) * mm, "mid": v(86.92, -22.98) * mm, "end": v(86.64, -23.48) * mm});
            skPoint(sketch, "E43.63.0.6", {"position": v(85.13, -22.11) * mm});
            skLineSegment(sketch, "E43.63.0.7", {"start": v(87.27, -21.8) * mm, "end": v(87.26, -21.55) * mm});
            skPoint(sketch, "E43.63.0.8", {"position": v(85.92, -23.72) * mm});
            skArc(sketch, "E43.63.0.9", {"start": v(85.15, -21.55) * mm, "mid": v(84.93, -20.97) * mm, "end": v(84.36, -20.73) * mm});
            skLineSegment(sketch, "E43.63.0.10", {"start": v(88.05, -20.73) * mm, "end": v(87.3, -20.73) * mm});
            skArc(sketch, "E43.63.0.11", {"start": v(87.16, -22.45) * mm, "mid": v(87.25, -22.13) * mm, "end": v(87.27, -21.8) * mm});
            skArc(sketch, "E43.63.0.12", {"start": v(85.14, -21.8) * mm, "mid": v(85.16, -22.13) * mm, "end": v(85.25, -22.45) * mm});
            skPoint(sketch, "E43.63.0.13", {"position": v(86.3, -23.73) * mm});
            skArc(sketch, "E43.63.0.14", {"start": v(85.77, -23.48) * mm, "mid": v(85.95, -23.66) * mm, "end": v(86.2, -23.72) * mm});
            skArc(sketch, "E43.63.0.15", {"start": v(88.05, -20.73) * mm, "mid": v(87.48, -20.97) * mm, "end": v(87.26, -21.55) * mm});
            skArc(sketch, "E43.63.0.16", {"start": v(86.2, -23.73) * mm, "mid": v(86.46, -23.66) * mm, "end": v(86.64, -23.48) * mm});
            skLineSegment(sketch, "E43.63.0.17", {"start": v(86.2, -23.73) * mm, "end": v(86.2, -23.72) * mm});
            skLineSegment(sketch, "E43.63.0.18", {"start": v(86.2, -23.72) * mm, "end": v(86.2, -23.73) * mm});
            skArc(sketch, "E43.64.0.0", {"start": v(80.9, -22.45) * mm, "mid": v(81.14, -22.98) * mm, "end": v(81.42, -23.48) * mm});
            skPoint(sketch, "E43.64.0.1", {"position": v(80.85, -20.63) * mm});
            skLineSegment(sketch, "E43.64.0.2", {"start": v(80.8, -21.8) * mm, "end": v(80.8, -21.55) * mm});
            skPoint(sketch, "E43.64.0.3", {"position": v(82.94, -22.11) * mm});
            skPoint(sketch, "E43.64.0.4", {"position": v(82.14, -23.73) * mm});
            skArc(sketch, "E43.64.0.5", {"start": v(82.82, -22.45) * mm, "mid": v(82.58, -22.98) * mm, "end": v(82.3, -23.48) * mm});
            skPoint(sketch, "E43.64.0.6", {"position": v(80.78, -22.11) * mm});
            skLineSegment(sketch, "E43.64.0.7", {"start": v(82.93, -21.8) * mm, "end": v(82.92, -21.55) * mm});
            skPoint(sketch, "E43.64.0.8", {"position": v(81.58, -23.72) * mm});
            skArc(sketch, "E43.64.0.9", {"start": v(80.8, -21.55) * mm, "mid": v(80.59, -20.97) * mm, "end": v(80.02, -20.73) * mm});
            skLineSegment(sketch, "E43.64.0.10", {"start": v(83.7, -20.73) * mm, "end": v(82.96, -20.73) * mm});
            skArc(sketch, "E43.64.0.11", {"start": v(82.82, -22.45) * mm, "mid": v(82.9, -22.13) * mm, "end": v(82.93, -21.8) * mm});
            skArc(sketch, "E43.64.0.12", {"start": v(80.8, -21.8) * mm, "mid": v(80.82, -22.13) * mm, "end": v(80.9, -22.45) * mm});
            skPoint(sketch, "E43.64.0.13", {"position": v(81.95, -23.73) * mm});
            skArc(sketch, "E43.64.0.14", {"start": v(81.42, -23.48) * mm, "mid": v(81.6, -23.66) * mm, "end": v(81.85, -23.72) * mm});
            skArc(sketch, "E43.64.0.15", {"start": v(83.7, -20.73) * mm, "mid": v(83.13, -20.97) * mm, "end": v(82.92, -21.55) * mm});
            skArc(sketch, "E43.64.0.16", {"start": v(81.86, -23.73) * mm, "mid": v(82.11, -23.66) * mm, "end": v(82.3, -23.48) * mm});
            skLineSegment(sketch, "E43.64.0.17", {"start": v(81.86, -23.73) * mm, "end": v(81.85, -23.72) * mm});
            skLineSegment(sketch, "E43.64.0.18", {"start": v(81.85, -23.72) * mm, "end": v(81.86, -23.73) * mm});
            skArc(sketch, "E43.65.0.0", {"start": v(76.56, -22.45) * mm, "mid": v(76.8, -22.98) * mm, "end": v(77.08, -23.48) * mm});
            skPoint(sketch, "E43.65.0.1", {"position": v(76.5, -20.63) * mm});
            skLineSegment(sketch, "E43.65.0.2", {"start": v(76.45, -21.8) * mm, "end": v(76.46, -21.55) * mm});
            skPoint(sketch, "E43.65.0.3", {"position": v(78.6, -22.11) * mm});
            skPoint(sketch, "E43.65.0.4", {"position": v(77.8, -23.73) * mm});
            skArc(sketch, "E43.65.0.5", {"start": v(78.47, -22.45) * mm, "mid": v(78.24, -22.98) * mm, "end": v(77.96, -23.48) * mm});
            skPoint(sketch, "E43.65.0.6", {"position": v(76.44, -22.11) * mm});
            skLineSegment(sketch, "E43.65.0.7", {"start": v(78.58, -21.8) * mm, "end": v(78.57, -21.55) * mm});
            skPoint(sketch, "E43.65.0.8", {"position": v(77.23, -23.72) * mm});
            skArc(sketch, "E43.65.0.9", {"start": v(76.46, -21.55) * mm, "mid": v(76.24, -20.97) * mm, "end": v(75.68, -20.73) * mm});
            skLineSegment(sketch, "E43.65.0.10", {"start": v(79.36, -20.73) * mm, "end": v(78.61, -20.73) * mm});
            skArc(sketch, "E43.65.0.11", {"start": v(78.47, -22.45) * mm, "mid": v(78.56, -22.13) * mm, "end": v(78.58, -21.8) * mm});
            skArc(sketch, "E43.65.0.12", {"start": v(76.45, -21.8) * mm, "mid": v(76.47, -22.13) * mm, "end": v(76.56, -22.45) * mm});
            skPoint(sketch, "E43.65.0.13", {"position": v(77.6, -23.73) * mm});
            skArc(sketch, "E43.65.0.14", {"start": v(77.08, -23.48) * mm, "mid": v(77.26, -23.66) * mm, "end": v(77.5, -23.72) * mm});
            skArc(sketch, "E43.65.0.15", {"start": v(79.36, -20.73) * mm, "mid": v(78.8, -20.97) * mm, "end": v(78.57, -21.55) * mm});
            skArc(sketch, "E43.65.0.16", {"start": v(77.52, -23.73) * mm, "mid": v(77.77, -23.66) * mm, "end": v(77.96, -23.48) * mm});
            skLineSegment(sketch, "E43.65.0.17", {"start": v(77.52, -23.73) * mm, "end": v(77.5, -23.72) * mm});
            skLineSegment(sketch, "E43.65.0.18", {"start": v(77.5, -23.72) * mm, "end": v(77.52, -23.73) * mm});
            skArc(sketch, "E43.66.0.0", {"start": v(72.22, -22.45) * mm, "mid": v(72.46, -22.98) * mm, "end": v(72.74, -23.48) * mm});
            skPoint(sketch, "E43.66.0.1", {"position": v(72.16, -20.63) * mm});
            skLineSegment(sketch, "E43.66.0.2", {"start": v(72.1, -21.8) * mm, "end": v(72.12, -21.55) * mm});
            skPoint(sketch, "E43.66.0.3", {"position": v(74.25, -22.11) * mm});
            skPoint(sketch, "E43.66.0.4", {"position": v(73.46, -23.73) * mm});
            skArc(sketch, "E43.66.0.5", {"start": v(74.13, -22.45) * mm, "mid": v(73.9, -22.98) * mm, "end": v(73.61, -23.48) * mm});
            skPoint(sketch, "E43.66.0.6", {"position": v(72.1, -22.11) * mm});
            skLineSegment(sketch, "E43.66.0.7", {"start": v(74.24, -21.8) * mm, "end": v(74.23, -21.55) * mm});
            skPoint(sketch, "E43.66.0.8", {"position": v(72.89, -23.72) * mm});
            skArc(sketch, "E43.66.0.9", {"start": v(72.12, -21.55) * mm, "mid": v(71.9, -20.97) * mm, "end": v(71.33, -20.73) * mm});
            skLineSegment(sketch, "E43.66.0.10", {"start": v(75.02, -20.73) * mm, "end": v(74.27, -20.73) * mm});
            skArc(sketch, "E43.66.0.11", {"start": v(74.13, -22.45) * mm, "mid": v(74.22, -22.13) * mm, "end": v(74.24, -21.8) * mm});
            skArc(sketch, "E43.66.0.12", {"start": v(72.1, -21.8) * mm, "mid": v(72.13, -22.13) * mm, "end": v(72.22, -22.45) * mm});
            skPoint(sketch, "E43.66.0.13", {"position": v(73.26, -23.73) * mm});
            skArc(sketch, "E43.66.0.14", {"start": v(72.74, -23.48) * mm, "mid": v(72.92, -23.66) * mm, "end": v(73.16, -23.72) * mm});
            skArc(sketch, "E43.66.0.15", {"start": v(75.02, -20.73) * mm, "mid": v(74.45, -20.97) * mm, "end": v(74.23, -21.55) * mm});
            skArc(sketch, "E43.66.0.16", {"start": v(73.17, -23.73) * mm, "mid": v(73.43, -23.66) * mm, "end": v(73.61, -23.48) * mm});
            skLineSegment(sketch, "E43.66.0.17", {"start": v(73.17, -23.73) * mm, "end": v(73.16, -23.72) * mm});
            skLineSegment(sketch, "E43.66.0.18", {"start": v(73.16, -23.72) * mm, "end": v(73.17, -23.73) * mm});
            skArc(sketch, "E43.67.0.0", {"start": v(67.88, -22.45) * mm, "mid": v(68.11, -22.98) * mm, "end": v(68.4, -23.48) * mm});
            skPoint(sketch, "E43.67.0.1", {"position": v(67.82, -20.63) * mm});
            skLineSegment(sketch, "E43.67.0.2", {"start": v(67.77, -21.8) * mm, "end": v(67.78, -21.55) * mm});
            skPoint(sketch, "E43.67.0.3", {"position": v(69.91, -22.11) * mm});
            skPoint(sketch, "E43.67.0.4", {"position": v(69.11, -23.73) * mm});
            skArc(sketch, "E43.67.0.5", {"start": v(69.79, -22.45) * mm, "mid": v(69.55, -22.98) * mm, "end": v(69.27, -23.48) * mm});
            skPoint(sketch, "E43.67.0.6", {"position": v(67.75, -22.11) * mm});
            skLineSegment(sketch, "E43.67.0.7", {"start": v(69.9, -21.8) * mm, "end": v(69.89, -21.55) * mm});
            skPoint(sketch, "E43.67.0.8", {"position": v(68.55, -23.72) * mm});
            skArc(sketch, "E43.67.0.9", {"start": v(67.78, -21.55) * mm, "mid": v(67.56, -20.97) * mm, "end": v(66.99, -20.73) * mm});
            skLineSegment(sketch, "E43.67.0.10", {"start": v(70.67, -20.73) * mm, "end": v(69.93, -20.73) * mm});
            skArc(sketch, "E43.67.0.11", {"start": v(69.79, -22.45) * mm, "mid": v(69.88, -22.13) * mm, "end": v(69.9, -21.8) * mm});
            skArc(sketch, "E43.67.0.12", {"start": v(67.77, -21.8) * mm, "mid": v(67.79, -22.13) * mm, "end": v(67.88, -22.45) * mm});
            skPoint(sketch, "E43.67.0.13", {"position": v(68.92, -23.73) * mm});
            skArc(sketch, "E43.67.0.14", {"start": v(68.4, -23.48) * mm, "mid": v(68.57, -23.66) * mm, "end": v(68.82, -23.72) * mm});
            skArc(sketch, "E43.67.0.15", {"start": v(70.67, -20.73) * mm, "mid": v(70.1, -20.97) * mm, "end": v(69.89, -21.55) * mm});
            skArc(sketch, "E43.67.0.16", {"start": v(68.83, -23.73) * mm, "mid": v(69.08, -23.66) * mm, "end": v(69.27, -23.48) * mm});
            skLineSegment(sketch, "E43.67.0.17", {"start": v(68.83, -23.73) * mm, "end": v(68.82, -23.72) * mm});
            skLineSegment(sketch, "E43.67.0.18", {"start": v(68.82, -23.72) * mm, "end": v(68.83, -23.73) * mm});
            skArc(sketch, "E43.68.0.0", {"start": v(63.53, -22.45) * mm, "mid": v(63.77, -22.98) * mm, "end": v(64.05, -23.48) * mm});
            skPoint(sketch, "E43.68.0.1", {"position": v(63.47, -20.63) * mm});
            skLineSegment(sketch, "E43.68.0.2", {"start": v(63.42, -21.8) * mm, "end": v(63.43, -21.55) * mm});
            skPoint(sketch, "E43.68.0.3", {"position": v(65.57, -22.11) * mm});
            skPoint(sketch, "E43.68.0.4", {"position": v(64.77, -23.73) * mm});
            skArc(sketch, "E43.68.0.5", {"start": v(65.44, -22.45) * mm, "mid": v(65.2, -22.98) * mm, "end": v(64.93, -23.48) * mm});
            skPoint(sketch, "E43.68.0.6", {"position": v(63.4, -22.11) * mm});
            skLineSegment(sketch, "E43.68.0.7", {"start": v(65.55, -21.8) * mm, "end": v(65.54, -21.55) * mm});
            skPoint(sketch, "E43.68.0.8", {"position": v(64.2, -23.72) * mm});
            skArc(sketch, "E43.68.0.9", {"start": v(63.43, -21.55) * mm, "mid": v(63.21, -20.97) * mm, "end": v(62.65, -20.73) * mm});
            skLineSegment(sketch, "E43.68.0.10", {"start": v(66.33, -20.73) * mm, "end": v(65.58, -20.73) * mm});
            skArc(sketch, "E43.68.0.11", {"start": v(65.44, -22.45) * mm, "mid": v(65.53, -22.13) * mm, "end": v(65.55, -21.8) * mm});
            skArc(sketch, "E43.68.0.12", {"start": v(63.42, -21.8) * mm, "mid": v(63.44, -22.13) * mm, "end": v(63.53, -22.45) * mm});
            skPoint(sketch, "E43.68.0.13", {"position": v(64.58, -23.73) * mm});
            skArc(sketch, "E43.68.0.14", {"start": v(64.05, -23.48) * mm, "mid": v(64.23, -23.66) * mm, "end": v(64.48, -23.72) * mm});
            skArc(sketch, "E43.68.0.15", {"start": v(66.33, -20.73) * mm, "mid": v(65.76, -20.97) * mm, "end": v(65.54, -21.55) * mm});
            skArc(sketch, "E43.68.0.16", {"start": v(64.49, -23.73) * mm, "mid": v(64.74, -23.66) * mm, "end": v(64.93, -23.48) * mm});
            skLineSegment(sketch, "E43.68.0.17", {"start": v(64.49, -23.73) * mm, "end": v(64.48, -23.72) * mm});
            skLineSegment(sketch, "E43.68.0.18", {"start": v(64.48, -23.72) * mm, "end": v(64.49, -23.73) * mm});
            skArc(sketch, "E43.69.0.0", {"start": v(59.2, -22.45) * mm, "mid": v(59.43, -22.98) * mm, "end": v(59.7, -23.48) * mm});
            skPoint(sketch, "E43.69.0.1", {"position": v(59.13, -20.63) * mm});
            skLineSegment(sketch, "E43.69.0.2", {"start": v(59.08, -21.8) * mm, "end": v(59.09, -21.55) * mm});
            skPoint(sketch, "E43.69.0.3", {"position": v(61.22, -22.11) * mm});
            skPoint(sketch, "E43.69.0.4", {"position": v(60.43, -23.73) * mm});
            skArc(sketch, "E43.69.0.5", {"start": v(61.1, -22.45) * mm, "mid": v(60.86, -22.98) * mm, "end": v(60.58, -23.48) * mm});
            skPoint(sketch, "E43.69.0.6", {"position": v(59.06, -22.11) * mm});
            skLineSegment(sketch, "E43.69.0.7", {"start": v(61.2, -21.8) * mm, "end": v(61.2, -21.55) * mm});
            skPoint(sketch, "E43.69.0.8", {"position": v(59.86, -23.72) * mm});
            skArc(sketch, "E43.69.0.9", {"start": v(59.09, -21.55) * mm, "mid": v(58.87, -20.97) * mm, "end": v(58.3, -20.73) * mm});
            skLineSegment(sketch, "E43.69.0.10", {"start": v(61.99, -20.73) * mm, "end": v(61.24, -20.73) * mm});
            skArc(sketch, "E43.69.0.11", {"start": v(61.1, -22.45) * mm, "mid": v(61.19, -22.13) * mm, "end": v(61.2, -21.8) * mm});
            skArc(sketch, "E43.69.0.12", {"start": v(59.08, -21.8) * mm, "mid": v(59.1, -22.13) * mm, "end": v(59.2, -22.45) * mm});
            skPoint(sketch, "E43.69.0.13", {"position": v(60.23, -23.73) * mm});
            skArc(sketch, "E43.69.0.14", {"start": v(59.7, -23.48) * mm, "mid": v(59.89, -23.66) * mm, "end": v(60.13, -23.72) * mm});
            skArc(sketch, "E43.69.0.15", {"start": v(61.99, -20.73) * mm, "mid": v(61.42, -20.97) * mm, "end": v(61.2, -21.55) * mm});
            skArc(sketch, "E43.69.0.16", {"start": v(60.14, -23.73) * mm, "mid": v(60.4, -23.66) * mm, "end": v(60.58, -23.48) * mm});
            skLineSegment(sketch, "E43.69.0.17", {"start": v(60.14, -23.73) * mm, "end": v(60.13, -23.72) * mm});
            skLineSegment(sketch, "E43.69.0.18", {"start": v(60.13, -23.72) * mm, "end": v(60.14, -23.73) * mm});
            skArc(sketch, "E43.70.0.0", {"start": v(54.85, -22.45) * mm, "mid": v(55.08, -22.98) * mm, "end": v(55.36, -23.48) * mm});
            skPoint(sketch, "E43.70.0.1", {"position": v(54.79, -20.63) * mm});
            skLineSegment(sketch, "E43.70.0.2", {"start": v(54.74, -21.8) * mm, "end": v(54.75, -21.55) * mm});
            skPoint(sketch, "E43.70.0.3", {"position": v(56.88, -22.11) * mm});
            skPoint(sketch, "E43.70.0.4", {"position": v(56.08, -23.73) * mm});
            skArc(sketch, "E43.70.0.5", {"start": v(56.76, -22.45) * mm, "mid": v(56.52, -22.98) * mm, "end": v(56.24, -23.48) * mm});
            skPoint(sketch, "E43.70.0.6", {"position": v(54.72, -22.11) * mm});
            skLineSegment(sketch, "E43.70.0.7", {"start": v(56.87, -21.8) * mm, "end": v(56.86, -21.55) * mm});
            skPoint(sketch, "E43.70.0.8", {"position": v(55.52, -23.72) * mm});
            skArc(sketch, "E43.70.0.9", {"start": v(54.75, -21.55) * mm, "mid": v(54.53, -20.97) * mm, "end": v(53.96, -20.73) * mm});
            skLineSegment(sketch, "E43.70.0.10", {"start": v(57.64, -20.73) * mm, "end": v(56.9, -20.73) * mm});
            skArc(sketch, "E43.70.0.11", {"start": v(56.76, -22.45) * mm, "mid": v(56.85, -22.13) * mm, "end": v(56.87, -21.8) * mm});
            skArc(sketch, "E43.70.0.12", {"start": v(54.74, -21.8) * mm, "mid": v(54.76, -22.13) * mm, "end": v(54.85, -22.45) * mm});
            skPoint(sketch, "E43.70.0.13", {"position": v(55.9, -23.73) * mm});
            skArc(sketch, "E43.70.0.14", {"start": v(55.36, -23.48) * mm, "mid": v(55.54, -23.66) * mm, "end": v(55.79, -23.72) * mm});
            skArc(sketch, "E43.70.0.15", {"start": v(57.64, -20.73) * mm, "mid": v(57.07, -20.97) * mm, "end": v(56.86, -21.55) * mm});
            skArc(sketch, "E43.70.0.16", {"start": v(55.8, -23.73) * mm, "mid": v(56.05, -23.66) * mm, "end": v(56.24, -23.48) * mm});
            skLineSegment(sketch, "E43.70.0.17", {"start": v(55.8, -23.73) * mm, "end": v(55.79, -23.72) * mm});
            skLineSegment(sketch, "E43.70.0.18", {"start": v(55.79, -23.72) * mm, "end": v(55.8, -23.73) * mm});
            skArc(sketch, "E43.71.0.0", {"start": v(50.5, -22.45) * mm, "mid": v(50.74, -22.98) * mm, "end": v(51.02, -23.48) * mm});
            skPoint(sketch, "E43.71.0.1", {"position": v(50.44, -20.63) * mm});
            skLineSegment(sketch, "E43.71.0.2", {"start": v(50.4, -21.8) * mm, "end": v(50.4, -21.55) * mm});
            skPoint(sketch, "E43.71.0.3", {"position": v(52.54, -22.11) * mm});
            skPoint(sketch, "E43.71.0.4", {"position": v(51.74, -23.73) * mm});
            skArc(sketch, "E43.71.0.5", {"start": v(52.41, -22.45) * mm, "mid": v(52.18, -22.98) * mm, "end": v(51.9, -23.48) * mm});
            skPoint(sketch, "E43.71.0.6", {"position": v(50.38, -22.11) * mm});
            skLineSegment(sketch, "E43.71.0.7", {"start": v(52.52, -21.8) * mm, "end": v(52.51, -21.55) * mm});
            skPoint(sketch, "E43.71.0.8", {"position": v(51.17, -23.72) * mm});
            skArc(sketch, "E43.71.0.9", {"start": v(50.4, -21.55) * mm, "mid": v(50.18, -20.97) * mm, "end": v(49.62, -20.73) * mm});
            skLineSegment(sketch, "E43.71.0.10", {"start": v(53.3, -20.73) * mm, "end": v(52.55, -20.73) * mm});
            skArc(sketch, "E43.71.0.11", {"start": v(52.41, -22.45) * mm, "mid": v(52.5, -22.13) * mm, "end": v(52.52, -21.8) * mm});
            skArc(sketch, "E43.71.0.12", {"start": v(50.4, -21.8) * mm, "mid": v(50.41, -22.13) * mm, "end": v(50.5, -22.45) * mm});
            skPoint(sketch, "E43.71.0.13", {"position": v(51.55, -23.73) * mm});
            skArc(sketch, "E43.71.0.14", {"start": v(51.02, -23.48) * mm, "mid": v(51.2, -23.66) * mm, "end": v(51.45, -23.72) * mm});
            skArc(sketch, "E43.71.0.15", {"start": v(53.3, -20.73) * mm, "mid": v(52.73, -20.97) * mm, "end": v(52.51, -21.55) * mm});
            skArc(sketch, "E43.71.0.16", {"start": v(51.46, -23.73) * mm, "mid": v(51.7, -23.66) * mm, "end": v(51.9, -23.48) * mm});
            skLineSegment(sketch, "E43.71.0.17", {"start": v(51.46, -23.73) * mm, "end": v(51.45, -23.72) * mm});
            skLineSegment(sketch, "E43.71.0.18", {"start": v(51.45, -23.72) * mm, "end": v(51.46, -23.73) * mm});
            skArc(sketch, "E43.72.0.0", {"start": v(46.16, -22.45) * mm, "mid": v(46.4, -22.98) * mm, "end": v(46.68, -23.48) * mm});
            skPoint(sketch, "E43.72.0.1", {"position": v(46.1, -20.63) * mm});
            skLineSegment(sketch, "E43.72.0.2", {"start": v(46.05, -21.8) * mm, "end": v(46.06, -21.55) * mm});
            skPoint(sketch, "E43.72.0.3", {"position": v(48.2, -22.11) * mm});
            skPoint(sketch, "E43.72.0.4", {"position": v(47.4, -23.73) * mm});
            skArc(sketch, "E43.72.0.5", {"start": v(48.07, -22.45) * mm, "mid": v(47.83, -22.98) * mm, "end": v(47.55, -23.48) * mm});
            skPoint(sketch, "E43.72.0.6", {"position": v(46.03, -22.11) * mm});
            skLineSegment(sketch, "E43.72.0.7", {"start": v(48.18, -21.8) * mm, "end": v(48.17, -21.55) * mm});
            skPoint(sketch, "E43.72.0.8", {"position": v(46.83, -23.72) * mm});
            skArc(sketch, "E43.72.0.9", {"start": v(46.06, -21.55) * mm, "mid": v(45.84, -20.97) * mm, "end": v(45.27, -20.73) * mm});
            skLineSegment(sketch, "E43.72.0.10", {"start": v(48.96, -20.73) * mm, "end": v(48.2, -20.73) * mm});
            skArc(sketch, "E43.72.0.11", {"start": v(48.07, -22.45) * mm, "mid": v(48.16, -22.13) * mm, "end": v(48.18, -21.8) * mm});
            skArc(sketch, "E43.72.0.12", {"start": v(46.05, -21.8) * mm, "mid": v(46.07, -22.13) * mm, "end": v(46.16, -22.45) * mm});
            skPoint(sketch, "E43.72.0.13", {"position": v(47.2, -23.73) * mm});
            skArc(sketch, "E43.72.0.14", {"start": v(46.68, -23.48) * mm, "mid": v(46.86, -23.66) * mm, "end": v(47.1, -23.72) * mm});
            skArc(sketch, "E43.72.0.15", {"start": v(48.96, -20.73) * mm, "mid": v(48.39, -20.97) * mm, "end": v(48.17, -21.55) * mm});
            skArc(sketch, "E43.72.0.16", {"start": v(47.11, -23.73) * mm, "mid": v(47.37, -23.66) * mm, "end": v(47.55, -23.48) * mm});
            skLineSegment(sketch, "E43.72.0.17", {"start": v(47.11, -23.73) * mm, "end": v(47.1, -23.72) * mm});
            skLineSegment(sketch, "E43.72.0.18", {"start": v(47.1, -23.72) * mm, "end": v(47.11, -23.73) * mm});
            skArc(sketch, "E43.73.0.0", {"start": v(41.82, -22.45) * mm, "mid": v(42.05, -22.98) * mm, "end": v(42.33, -23.48) * mm});
            skPoint(sketch, "E43.73.0.1", {"position": v(41.75, -20.63) * mm});
            skLineSegment(sketch, "E43.73.0.2", {"start": v(41.7, -21.8) * mm, "end": v(41.72, -21.55) * mm});
            skPoint(sketch, "E43.73.0.3", {"position": v(43.85, -22.11) * mm});
            skPoint(sketch, "E43.73.0.4", {"position": v(43.05, -23.73) * mm});
            skArc(sketch, "E43.73.0.5", {"start": v(43.73, -22.45) * mm, "mid": v(43.49, -22.98) * mm, "end": v(43.21, -23.48) * mm});
            skPoint(sketch, "E43.73.0.6", {"position": v(41.7, -22.11) * mm});
            skLineSegment(sketch, "E43.73.0.7", {"start": v(43.84, -21.8) * mm, "end": v(43.83, -21.55) * mm});
            skPoint(sketch, "E43.73.0.8", {"position": v(42.49, -23.72) * mm});
            skArc(sketch, "E43.73.0.9", {"start": v(41.72, -21.55) * mm, "mid": v(41.5, -20.97) * mm, "end": v(40.93, -20.73) * mm});
            skLineSegment(sketch, "E43.73.0.10", {"start": v(44.61, -20.73) * mm, "end": v(43.87, -20.73) * mm});
            skArc(sketch, "E43.73.0.11", {"start": v(43.73, -22.45) * mm, "mid": v(43.82, -22.13) * mm, "end": v(43.84, -21.8) * mm});
            skArc(sketch, "E43.73.0.12", {"start": v(41.7, -21.8) * mm, "mid": v(41.73, -22.13) * mm, "end": v(41.82, -22.45) * mm});
            skPoint(sketch, "E43.73.0.13", {"position": v(42.86, -23.73) * mm});
            skArc(sketch, "E43.73.0.14", {"start": v(42.33, -23.48) * mm, "mid": v(42.51, -23.66) * mm, "end": v(42.76, -23.72) * mm});
            skArc(sketch, "E43.73.0.15", {"start": v(44.61, -20.73) * mm, "mid": v(44.04, -20.97) * mm, "end": v(43.83, -21.55) * mm});
            skArc(sketch, "E43.73.0.16", {"start": v(42.77, -23.73) * mm, "mid": v(43.02, -23.66) * mm, "end": v(43.21, -23.48) * mm});
            skLineSegment(sketch, "E43.73.0.17", {"start": v(42.77, -23.73) * mm, "end": v(42.76, -23.72) * mm});
            skLineSegment(sketch, "E43.73.0.18", {"start": v(42.76, -23.72) * mm, "end": v(42.77, -23.73) * mm});
            skArc(sketch, "E43.74.0.0", {"start": v(37.47, -22.45) * mm, "mid": v(37.7, -22.98) * mm, "end": v(37.99, -23.48) * mm});
            skPoint(sketch, "E43.74.0.1", {"position": v(37.41, -20.63) * mm});
            skLineSegment(sketch, "E43.74.0.2", {"start": v(37.36, -21.8) * mm, "end": v(37.37, -21.55) * mm});
            skPoint(sketch, "E43.74.0.3", {"position": v(39.5, -22.11) * mm});
            skPoint(sketch, "E43.74.0.4", {"position": v(38.7, -23.73) * mm});
            skArc(sketch, "E43.74.0.5", {"start": v(39.38, -22.45) * mm, "mid": v(39.15, -22.98) * mm, "end": v(38.87, -23.48) * mm});
            skPoint(sketch, "E43.74.0.6", {"position": v(37.35, -22.11) * mm});
            skLineSegment(sketch, "E43.74.0.7", {"start": v(39.5, -21.8) * mm, "end": v(39.48, -21.55) * mm});
            skPoint(sketch, "E43.74.0.8", {"position": v(38.14, -23.72) * mm});
            skArc(sketch, "E43.74.0.9", {"start": v(37.37, -21.55) * mm, "mid": v(37.15, -20.97) * mm, "end": v(36.59, -20.73) * mm});
            skLineSegment(sketch, "E43.74.0.10", {"start": v(40.27, -20.73) * mm, "end": v(39.52, -20.73) * mm});
            skArc(sketch, "E43.74.0.11", {"start": v(39.38, -22.45) * mm, "mid": v(39.47, -22.13) * mm, "end": v(39.5, -21.8) * mm});
            skArc(sketch, "E43.74.0.12", {"start": v(37.36, -21.8) * mm, "mid": v(37.38, -22.13) * mm, "end": v(37.47, -22.45) * mm});
            skPoint(sketch, "E43.74.0.13", {"position": v(38.52, -23.73) * mm});
            skArc(sketch, "E43.74.0.14", {"start": v(37.99, -23.48) * mm, "mid": v(38.17, -23.66) * mm, "end": v(38.42, -23.72) * mm});
            skArc(sketch, "E43.74.0.15", {"start": v(40.27, -20.73) * mm, "mid": v(39.7, -20.97) * mm, "end": v(39.48, -21.55) * mm});
            skArc(sketch, "E43.74.0.16", {"start": v(38.43, -23.73) * mm, "mid": v(38.68, -23.66) * mm, "end": v(38.87, -23.48) * mm});
            skLineSegment(sketch, "E43.74.0.17", {"start": v(38.43, -23.73) * mm, "end": v(38.42, -23.72) * mm});
            skLineSegment(sketch, "E43.74.0.18", {"start": v(38.42, -23.72) * mm, "end": v(38.43, -23.73) * mm});
            skArc(sketch, "E43.75.0.0", {"start": v(33.13, -22.45) * mm, "mid": v(33.37, -22.98) * mm, "end": v(33.65, -23.48) * mm});
            skPoint(sketch, "E43.75.0.1", {"position": v(33.07, -20.63) * mm});
            skLineSegment(sketch, "E43.75.0.2", {"start": v(33.02, -21.8) * mm, "end": v(33.03, -21.55) * mm});
            skPoint(sketch, "E43.75.0.3", {"position": v(35.16, -22.11) * mm});
            skPoint(sketch, "E43.75.0.4", {"position": v(34.37, -23.73) * mm});
            skArc(sketch, "E43.75.0.5", {"start": v(35.04, -22.45) * mm, "mid": v(34.8, -22.98) * mm, "end": v(34.52, -23.48) * mm});
            skPoint(sketch, "E43.75.0.6", {"position": v(33, -22.11) * mm});
            skLineSegment(sketch, "E43.75.0.7", {"start": v(35.15, -21.8) * mm, "end": v(35.14, -21.55) * mm});
            skPoint(sketch, "E43.75.0.8", {"position": v(33.8, -23.72) * mm});
            skArc(sketch, "E43.75.0.9", {"start": v(33.03, -21.55) * mm, "mid": v(32.81, -20.97) * mm, "end": v(32.24, -20.73) * mm});
            skLineSegment(sketch, "E43.75.0.10", {"start": v(35.93, -20.73) * mm, "end": v(35.18, -20.73) * mm});
            skArc(sketch, "E43.75.0.11", {"start": v(35.04, -22.45) * mm, "mid": v(35.13, -22.13) * mm, "end": v(35.15, -21.8) * mm});
            skArc(sketch, "E43.75.0.12", {"start": v(33.02, -21.8) * mm, "mid": v(33.04, -22.13) * mm, "end": v(33.13, -22.45) * mm});
            skPoint(sketch, "E43.75.0.13", {"position": v(34.17, -23.73) * mm});
            skArc(sketch, "E43.75.0.14", {"start": v(33.65, -23.48) * mm, "mid": v(33.83, -23.66) * mm, "end": v(34.07, -23.72) * mm});
            skArc(sketch, "E43.75.0.15", {"start": v(35.93, -20.73) * mm, "mid": v(35.36, -20.97) * mm, "end": v(35.14, -21.55) * mm});
            skArc(sketch, "E43.75.0.16", {"start": v(34.08, -23.73) * mm, "mid": v(34.34, -23.66) * mm, "end": v(34.52, -23.48) * mm});
            skLineSegment(sketch, "E43.75.0.17", {"start": v(34.08, -23.73) * mm, "end": v(34.07, -23.72) * mm});
            skLineSegment(sketch, "E43.75.0.18", {"start": v(34.07, -23.72) * mm, "end": v(34.08, -23.73) * mm});
            skArc(sketch, "E43.76.0.0", {"start": v(28.79, -22.45) * mm, "mid": v(29.02, -22.98) * mm, "end": v(29.3, -23.48) * mm});
            skPoint(sketch, "E43.76.0.1", {"position": v(28.72, -20.63) * mm});
            skLineSegment(sketch, "E43.76.0.2", {"start": v(28.67, -21.8) * mm, "end": v(28.69, -21.55) * mm});
            skPoint(sketch, "E43.76.0.3", {"position": v(30.82, -22.11) * mm});
            skPoint(sketch, "E43.76.0.4", {"position": v(30.02, -23.73) * mm});
            skArc(sketch, "E43.76.0.5", {"start": v(30.7, -22.45) * mm, "mid": v(30.46, -22.98) * mm, "end": v(30.18, -23.48) * mm});
            skPoint(sketch, "E43.76.0.6", {"position": v(28.66, -22.11) * mm});
            skLineSegment(sketch, "E43.76.0.7", {"start": v(30.8, -21.8) * mm, "end": v(30.8, -21.55) * mm});
            skPoint(sketch, "E43.76.0.8", {"position": v(29.46, -23.72) * mm});
            skArc(sketch, "E43.76.0.9", {"start": v(28.69, -21.55) * mm, "mid": v(28.47, -20.97) * mm, "end": v(27.9, -20.73) * mm});
            skLineSegment(sketch, "E43.76.0.10", {"start": v(31.58, -20.73) * mm, "end": v(30.84, -20.73) * mm});
            skArc(sketch, "E43.76.0.11", {"start": v(30.7, -22.45) * mm, "mid": v(30.79, -22.13) * mm, "end": v(30.8, -21.8) * mm});
            skArc(sketch, "E43.76.0.12", {"start": v(28.67, -21.8) * mm, "mid": v(28.7, -22.13) * mm, "end": v(28.79, -22.45) * mm});
            skPoint(sketch, "E43.76.0.13", {"position": v(29.83, -23.73) * mm});
            skArc(sketch, "E43.76.0.14", {"start": v(29.3, -23.48) * mm, "mid": v(29.48, -23.66) * mm, "end": v(29.73, -23.72) * mm});
            skArc(sketch, "E43.76.0.15", {"start": v(31.58, -20.73) * mm, "mid": v(31.01, -20.97) * mm, "end": v(30.8, -21.55) * mm});
            skArc(sketch, "E43.76.0.16", {"start": v(29.74, -23.73) * mm, "mid": v(30, -23.66) * mm, "end": v(30.18, -23.48) * mm});
            skLineSegment(sketch, "E43.76.0.17", {"start": v(29.74, -23.73) * mm, "end": v(29.73, -23.72) * mm});
            skLineSegment(sketch, "E43.76.0.18", {"start": v(29.73, -23.72) * mm, "end": v(29.74, -23.73) * mm});
            skArc(sketch, "E43.77.0.0", {"start": v(24.44, -22.45) * mm, "mid": v(24.68, -22.98) * mm, "end": v(24.96, -23.48) * mm});
            skPoint(sketch, "E43.77.0.1", {"position": v(24.38, -20.63) * mm});
            skLineSegment(sketch, "E43.77.0.2", {"start": v(24.33, -21.8) * mm, "end": v(24.34, -21.55) * mm});
            skPoint(sketch, "E43.77.0.3", {"position": v(26.48, -22.11) * mm});
            skPoint(sketch, "E43.77.0.4", {"position": v(25.68, -23.73) * mm});
            skArc(sketch, "E43.77.0.5", {"start": v(26.35, -22.45) * mm, "mid": v(26.12, -22.98) * mm, "end": v(25.84, -23.48) * mm});
            skPoint(sketch, "E43.77.0.6", {"position": v(24.32, -22.11) * mm});
            skLineSegment(sketch, "E43.77.0.7", {"start": v(26.46, -21.8) * mm, "end": v(26.45, -21.55) * mm});
            skPoint(sketch, "E43.77.0.8", {"position": v(25.11, -23.72) * mm});
            skArc(sketch, "E43.77.0.9", {"start": v(24.34, -21.55) * mm, "mid": v(24.12, -20.97) * mm, "end": v(23.56, -20.73) * mm});
            skLineSegment(sketch, "E43.77.0.10", {"start": v(27.24, -20.73) * mm, "end": v(26.5, -20.73) * mm});
            skArc(sketch, "E43.77.0.11", {"start": v(26.35, -22.45) * mm, "mid": v(26.44, -22.13) * mm, "end": v(26.46, -21.8) * mm});
            skArc(sketch, "E43.77.0.12", {"start": v(24.33, -21.8) * mm, "mid": v(24.35, -22.13) * mm, "end": v(24.44, -22.45) * mm});
            skPoint(sketch, "E43.77.0.13", {"position": v(25.49, -23.73) * mm});
            skArc(sketch, "E43.77.0.14", {"start": v(24.96, -23.48) * mm, "mid": v(25.14, -23.66) * mm, "end": v(25.39, -23.72) * mm});
            skArc(sketch, "E43.77.0.15", {"start": v(27.24, -20.73) * mm, "mid": v(26.67, -20.97) * mm, "end": v(26.45, -21.55) * mm});
            skArc(sketch, "E43.77.0.16", {"start": v(25.4, -23.73) * mm, "mid": v(25.65, -23.66) * mm, "end": v(25.84, -23.48) * mm});
            skLineSegment(sketch, "E43.77.0.17", {"start": v(25.4, -23.73) * mm, "end": v(25.39, -23.72) * mm});
            skLineSegment(sketch, "E43.77.0.18", {"start": v(25.39, -23.72) * mm, "end": v(25.4, -23.73) * mm});
            skArc(sketch, "E43.78.0.0", {"start": v(20.1, -22.45) * mm, "mid": v(20.34, -22.98) * mm, "end": v(20.62, -23.48) * mm});
            skPoint(sketch, "E43.78.0.1", {"position": v(20.04, -20.63) * mm});
            skLineSegment(sketch, "E43.78.0.2", {"start": v(19.99, -21.8) * mm, "end": v(20, -21.55) * mm});
            skPoint(sketch, "E43.78.0.3", {"position": v(22.13, -22.11) * mm});
            skPoint(sketch, "E43.78.0.4", {"position": v(21.34, -23.73) * mm});
            skArc(sketch, "E43.78.0.5", {"start": v(22, -22.45) * mm, "mid": v(21.77, -22.98) * mm, "end": v(21.5, -23.48) * mm});
            skPoint(sketch, "E43.78.0.6", {"position": v(19.97, -22.11) * mm});
            skLineSegment(sketch, "E43.78.0.7", {"start": v(22.12, -21.8) * mm, "end": v(22.1, -21.55) * mm});
            skPoint(sketch, "E43.78.0.8", {"position": v(20.77, -23.72) * mm});
            skArc(sketch, "E43.78.0.9", {"start": v(20, -21.55) * mm, "mid": v(19.78, -20.97) * mm, "end": v(19.21, -20.73) * mm});
            skLineSegment(sketch, "E43.78.0.10", {"start": v(22.9, -20.73) * mm, "end": v(22.15, -20.73) * mm});
            skArc(sketch, "E43.78.0.11", {"start": v(22, -22.45) * mm, "mid": v(22.1, -22.13) * mm, "end": v(22.12, -21.8) * mm});
            skArc(sketch, "E43.78.0.12", {"start": v(19.99, -21.8) * mm, "mid": v(20, -22.13) * mm, "end": v(20.1, -22.45) * mm});
            skPoint(sketch, "E43.78.0.13", {"position": v(21.14, -23.73) * mm});
            skArc(sketch, "E43.78.0.14", {"start": v(20.62, -23.48) * mm, "mid": v(20.8, -23.66) * mm, "end": v(21.04, -23.72) * mm});
            skArc(sketch, "E43.78.0.15", {"start": v(22.9, -20.73) * mm, "mid": v(22.33, -20.97) * mm, "end": v(22.1, -21.55) * mm});
            skArc(sketch, "E43.78.0.16", {"start": v(21.05, -23.73) * mm, "mid": v(21.3, -23.66) * mm, "end": v(21.5, -23.48) * mm});
            skLineSegment(sketch, "E43.78.0.17", {"start": v(21.05, -23.73) * mm, "end": v(21.04, -23.72) * mm});
            skLineSegment(sketch, "E43.78.0.18", {"start": v(21.04, -23.72) * mm, "end": v(21.05, -23.73) * mm});
            skArc(sketch, "E43.79.0.0", {"start": v(15.76, -22.45) * mm, "mid": v(16, -22.98) * mm, "end": v(16.27, -23.48) * mm});
            skPoint(sketch, "E43.79.0.1", {"position": v(15.7, -20.63) * mm});
            skLineSegment(sketch, "E43.79.0.2", {"start": v(15.64, -21.8) * mm, "end": v(15.66, -21.55) * mm});
            skPoint(sketch, "E43.79.0.3", {"position": v(17.79, -22.11) * mm});
            skPoint(sketch, "E43.79.0.4", {"position": v(17, -23.73) * mm});
            skArc(sketch, "E43.79.0.5", {"start": v(17.66, -22.45) * mm, "mid": v(17.43, -22.98) * mm, "end": v(17.15, -23.48) * mm});
            skPoint(sketch, "E43.79.0.6", {"position": v(15.63, -22.11) * mm});
            skLineSegment(sketch, "E43.79.0.7", {"start": v(17.78, -21.8) * mm, "end": v(17.76, -21.55) * mm});
            skPoint(sketch, "E43.79.0.8", {"position": v(16.43, -23.72) * mm});
            skArc(sketch, "E43.79.0.9", {"start": v(15.66, -21.55) * mm, "mid": v(15.44, -20.97) * mm, "end": v(14.87, -20.73) * mm});
            skLineSegment(sketch, "E43.79.0.10", {"start": v(18.55, -20.73) * mm, "end": v(17.8, -20.73) * mm});
            skArc(sketch, "E43.79.0.11", {"start": v(17.66, -22.45) * mm, "mid": v(17.76, -22.13) * mm, "end": v(17.78, -21.8) * mm});
            skArc(sketch, "E43.79.0.12", {"start": v(15.64, -21.8) * mm, "mid": v(15.67, -22.13) * mm, "end": v(15.76, -22.45) * mm});
            skPoint(sketch, "E43.79.0.13", {"position": v(16.8, -23.73) * mm});
            skArc(sketch, "E43.79.0.14", {"start": v(16.27, -23.48) * mm, "mid": v(16.45, -23.66) * mm, "end": v(16.7, -23.72) * mm});
            skArc(sketch, "E43.79.0.15", {"start": v(18.55, -20.73) * mm, "mid": v(17.98, -20.97) * mm, "end": v(17.76, -21.55) * mm});
            skArc(sketch, "E43.79.0.16", {"start": v(16.71, -23.73) * mm, "mid": v(16.96, -23.66) * mm, "end": v(17.15, -23.48) * mm});
            skLineSegment(sketch, "E43.79.0.17", {"start": v(16.71, -23.73) * mm, "end": v(16.7, -23.72) * mm});
            skLineSegment(sketch, "E43.79.0.18", {"start": v(16.7, -23.72) * mm, "end": v(16.71, -23.73) * mm});
            skArc(sketch, "E43.80.0.0", {"start": v(11.41, -22.45) * mm, "mid": v(11.65, -22.98) * mm, "end": v(11.93, -23.48) * mm});
            skPoint(sketch, "E43.80.0.1", {"position": v(11.35, -20.63) * mm});
            skLineSegment(sketch, "E43.80.0.2", {"start": v(11.3, -21.8) * mm, "end": v(11.31, -21.55) * mm});
            skPoint(sketch, "E43.80.0.3", {"position": v(13.45, -22.11) * mm});
            skPoint(sketch, "E43.80.0.4", {"position": v(12.65, -23.73) * mm});
            skArc(sketch, "E43.80.0.5", {"start": v(13.32, -22.45) * mm, "mid": v(13.09, -22.98) * mm, "end": v(12.8, -23.48) * mm});
            skPoint(sketch, "E43.80.0.6", {"position": v(11.29, -22.11) * mm});
            skLineSegment(sketch, "E43.80.0.7", {"start": v(13.43, -21.8) * mm, "end": v(13.42, -21.55) * mm});
            skPoint(sketch, "E43.80.0.8", {"position": v(12.08, -23.72) * mm});
            skArc(sketch, "E43.80.0.9", {"start": v(11.31, -21.55) * mm, "mid": v(11.1, -20.97) * mm, "end": v(10.52, -20.73) * mm});
            skLineSegment(sketch, "E43.80.0.10", {"start": v(14.2, -20.73) * mm, "end": v(13.46, -20.73) * mm});
            skArc(sketch, "E43.80.0.11", {"start": v(13.32, -22.45) * mm, "mid": v(13.41, -22.13) * mm, "end": v(13.43, -21.8) * mm});
            skArc(sketch, "E43.80.0.12", {"start": v(11.3, -21.8) * mm, "mid": v(11.32, -22.13) * mm, "end": v(11.41, -22.45) * mm});
            skPoint(sketch, "E43.80.0.13", {"position": v(12.46, -23.73) * mm});
            skArc(sketch, "E43.80.0.14", {"start": v(11.93, -23.48) * mm, "mid": v(12.11, -23.66) * mm, "end": v(12.35, -23.72) * mm});
            skArc(sketch, "E43.80.0.15", {"start": v(14.2, -20.73) * mm, "mid": v(13.64, -20.97) * mm, "end": v(13.42, -21.55) * mm});
            skArc(sketch, "E43.80.0.16", {"start": v(12.37, -23.73) * mm, "mid": v(12.62, -23.66) * mm, "end": v(12.8, -23.48) * mm});
            skLineSegment(sketch, "E43.80.0.17", {"start": v(12.37, -23.73) * mm, "end": v(12.35, -23.72) * mm});
            skLineSegment(sketch, "E43.80.0.18", {"start": v(12.35, -23.72) * mm, "end": v(12.37, -23.73) * mm});
            skArc(sketch, "E43.81.0.0", {"start": v(7.07, -22.45) * mm, "mid": v(7.3, -22.98) * mm, "end": v(7.58, -23.48) * mm});
            skPoint(sketch, "E43.81.0.1", {"position": v(7, -20.63) * mm});
            skLineSegment(sketch, "E43.81.0.2", {"start": v(6.96, -21.8) * mm, "end": v(6.97, -21.55) * mm});
            skPoint(sketch, "E43.81.0.3", {"position": v(9.1, -22.11) * mm});
            skPoint(sketch, "E43.81.0.4", {"position": v(8.3, -23.73) * mm});
            skArc(sketch, "E43.81.0.5", {"start": v(8.98, -22.45) * mm, "mid": v(8.74, -22.98) * mm, "end": v(8.46, -23.48) * mm});
            skPoint(sketch, "E43.81.0.6", {"position": v(6.94, -22.11) * mm});
            skLineSegment(sketch, "E43.81.0.7", {"start": v(9.09, -21.8) * mm, "end": v(9.08, -21.55) * mm});
            skPoint(sketch, "E43.81.0.8", {"position": v(7.74, -23.72) * mm});
            skArc(sketch, "E43.81.0.9", {"start": v(6.97, -21.55) * mm, "mid": v(6.75, -20.97) * mm, "end": v(6.18, -20.73) * mm});
            skLineSegment(sketch, "E43.81.0.10", {"start": v(9.86, -20.73) * mm, "end": v(9.12, -20.73) * mm});
            skArc(sketch, "E43.81.0.11", {"start": v(8.98, -22.45) * mm, "mid": v(9.07, -22.13) * mm, "end": v(9.09, -21.8) * mm});
            skArc(sketch, "E43.81.0.12", {"start": v(6.96, -21.8) * mm, "mid": v(6.98, -22.13) * mm, "end": v(7.07, -22.45) * mm});
            skPoint(sketch, "E43.81.0.13", {"position": v(8.11, -23.73) * mm});
            skArc(sketch, "E43.81.0.14", {"start": v(7.58, -23.48) * mm, "mid": v(7.77, -23.66) * mm, "end": v(8.01, -23.72) * mm});
            skArc(sketch, "E43.81.0.15", {"start": v(9.86, -20.73) * mm, "mid": v(9.3, -20.97) * mm, "end": v(9.08, -21.55) * mm});
            skArc(sketch, "E43.81.0.16", {"start": v(8.02, -23.73) * mm, "mid": v(8.28, -23.66) * mm, "end": v(8.46, -23.48) * mm});
            skLineSegment(sketch, "E43.81.0.17", {"start": v(8.02, -23.73) * mm, "end": v(8.01, -23.72) * mm});
            skLineSegment(sketch, "E43.81.0.18", {"start": v(8.01, -23.72) * mm, "end": v(8.02, -23.73) * mm});
            skArc(sketch, "E43.82.0.0", {"start": v(2.73, -22.45) * mm, "mid": v(2.96, -22.98) * mm, "end": v(3.24, -23.48) * mm});
            skPoint(sketch, "E43.82.0.1", {"position": v(2.66, -20.63) * mm});
            skLineSegment(sketch, "E43.82.0.2", {"start": v(2.61, -21.8) * mm, "end": v(2.62, -21.55) * mm});
            skPoint(sketch, "E43.82.0.3", {"position": v(4.76, -22.11) * mm});
            skPoint(sketch, "E43.82.0.4", {"position": v(3.96, -23.73) * mm});
            skArc(sketch, "E43.82.0.5", {"start": v(4.63, -22.45) * mm, "mid": v(4.4, -22.98) * mm, "end": v(4.12, -23.48) * mm});
            skPoint(sketch, "E43.82.0.6", {"position": v(2.6, -22.11) * mm});
            skLineSegment(sketch, "E43.82.0.7", {"start": v(4.75, -21.8) * mm, "end": v(4.73, -21.55) * mm});
            skPoint(sketch, "E43.82.0.8", {"position": v(3.4, -23.72) * mm});
            skArc(sketch, "E43.82.0.9", {"start": v(2.62, -21.55) * mm, "mid": v(2.4, -20.97) * mm, "end": v(1.84, -20.73) * mm});
            skLineSegment(sketch, "E43.82.0.10", {"start": v(5.52, -20.73) * mm, "end": v(4.78, -20.73) * mm});
            skArc(sketch, "E43.82.0.11", {"start": v(4.63, -22.45) * mm, "mid": v(4.72, -22.13) * mm, "end": v(4.75, -21.8) * mm});
            skArc(sketch, "E43.82.0.12", {"start": v(2.61, -21.8) * mm, "mid": v(2.64, -22.13) * mm, "end": v(2.73, -22.45) * mm});
            skPoint(sketch, "E43.82.0.13", {"position": v(3.77, -23.73) * mm});
            skArc(sketch, "E43.82.0.14", {"start": v(3.24, -23.48) * mm, "mid": v(3.42, -23.66) * mm, "end": v(3.67, -23.72) * mm});
            skArc(sketch, "E43.82.0.15", {"start": v(5.52, -20.73) * mm, "mid": v(4.95, -20.97) * mm, "end": v(4.73, -21.55) * mm});
            skArc(sketch, "E43.82.0.16", {"start": v(3.68, -23.73) * mm, "mid": v(3.93, -23.66) * mm, "end": v(4.12, -23.48) * mm});
            skLineSegment(sketch, "E43.82.0.17", {"start": v(3.68, -23.73) * mm, "end": v(3.67, -23.72) * mm});
            skLineSegment(sketch, "E43.82.0.18", {"start": v(3.67, -23.72) * mm, "end": v(3.68, -23.73) * mm});
            skArc(sketch, "E43.83.0.0", {"start": v(-1.62, -22.45) * mm, "mid": v(-1.38, -22.98) * mm, "end": v(-1.1, -23.48) * mm});
            skPoint(sketch, "E43.83.0.1", {"position": v(-1.68, -20.63) * mm});
            skLineSegment(sketch, "E43.83.0.2", {"start": v(-1.73, -21.8) * mm, "end": v(-1.72, -21.55) * mm});
            skPoint(sketch, "E43.83.0.3", {"position": v(0.42, -22.11) * mm});
            skPoint(sketch, "E43.83.0.4", {"position": v(-0.38, -23.73) * mm});
            skArc(sketch, "E43.83.0.5", {"start": v(0.3, -22.45) * mm, "mid": v(0.06, -22.98) * mm, "end": v(-0.22, -23.48) * mm});
            skPoint(sketch, "E43.83.0.6", {"position": v(-1.74, -22.11) * mm});
            skLineSegment(sketch, "E43.83.0.7", {"start": v(0.4, -21.8) * mm, "end": v(0.4, -21.55) * mm});
            skPoint(sketch, "E43.83.0.8", {"position": v(-0.95, -23.72) * mm});
            skArc(sketch, "E43.83.0.9", {"start": v(-1.72, -21.55) * mm, "mid": v(-1.94, -20.97) * mm, "end": v(-2.5, -20.73) * mm});
            skLineSegment(sketch, "E43.83.0.10", {"start": v(1.18, -20.73) * mm, "end": v(0.43, -20.73) * mm});
            skArc(sketch, "E43.83.0.11", {"start": v(0.3, -22.45) * mm, "mid": v(0.38, -22.13) * mm, "end": v(0.4, -21.8) * mm});
            skArc(sketch, "E43.83.0.12", {"start": v(-1.73, -21.8) * mm, "mid": v(-1.7, -22.13) * mm, "end": v(-1.62, -22.45) * mm});
            skPoint(sketch, "E43.83.0.13", {"position": v(-0.57, -23.73) * mm});
            skArc(sketch, "E43.83.0.14", {"start": v(-1.1, -23.48) * mm, "mid": v(-0.92, -23.66) * mm, "end": v(-0.68, -23.72) * mm});
            skArc(sketch, "E43.83.0.15", {"start": v(1.18, -20.73) * mm, "mid": v(0.6, -20.97) * mm, "end": v(0.4, -21.55) * mm});
            skArc(sketch, "E43.83.0.16", {"start": v(-0.66, -23.73) * mm, "mid": v(-0.41, -23.66) * mm, "end": v(-0.22, -23.48) * mm});
            skLineSegment(sketch, "E43.83.0.17", {"start": v(-0.66, -23.73) * mm, "end": v(-0.68, -23.72) * mm});
            skLineSegment(sketch, "E43.83.0.18", {"start": v(-0.68, -23.72) * mm, "end": v(-0.66, -23.73) * mm});
            skArc(sketch, "E43.84.0.0", {"start": v(-5.96, -22.45) * mm, "mid": v(-5.73, -22.98) * mm, "end": v(-5.45, -23.48) * mm});
            skPoint(sketch, "E43.84.0.1", {"position": v(-6.02, -20.63) * mm});
            skLineSegment(sketch, "E43.84.0.2", {"start": v(-6.07, -21.8) * mm, "end": v(-6.06, -21.55) * mm});
            skPoint(sketch, "E43.84.0.3", {"position": v(-3.93, -22.11) * mm});
            skPoint(sketch, "E43.84.0.4", {"position": v(-4.73, -23.73) * mm});
            skArc(sketch, "E43.84.0.5", {"start": v(-4.05, -22.45) * mm, "mid": v(-4.29, -22.98) * mm, "end": v(-4.57, -23.48) * mm});
            skPoint(sketch, "E43.84.0.6", {"position": v(-6.09, -22.11) * mm});
            skLineSegment(sketch, "E43.84.0.7", {"start": v(-3.94, -21.8) * mm, "end": v(-3.95, -21.55) * mm});
            skPoint(sketch, "E43.84.0.8", {"position": v(-5.3, -23.72) * mm});
            skArc(sketch, "E43.84.0.9", {"start": v(-6.06, -21.55) * mm, "mid": v(-6.28, -20.97) * mm, "end": v(-6.85, -20.73) * mm});
            skLineSegment(sketch, "E43.84.0.10", {"start": v(-3.17, -20.73) * mm, "end": v(-3.91, -20.73) * mm});
            skArc(sketch, "E43.84.0.11", {"start": v(-4.05, -22.45) * mm, "mid": v(-3.96, -22.13) * mm, "end": v(-3.94, -21.8) * mm});
            skArc(sketch, "E43.84.0.12", {"start": v(-6.07, -21.8) * mm, "mid": v(-6.05, -22.13) * mm, "end": v(-5.96, -22.45) * mm});
            skPoint(sketch, "E43.84.0.13", {"position": v(-4.92, -23.73) * mm});
            skArc(sketch, "E43.84.0.14", {"start": v(-5.45, -23.48) * mm, "mid": v(-5.26, -23.66) * mm, "end": v(-5.02, -23.72) * mm});
            skArc(sketch, "E43.84.0.15", {"start": v(-3.17, -20.73) * mm, "mid": v(-3.73, -20.97) * mm, "end": v(-3.95, -21.55) * mm});
            skArc(sketch, "E43.84.0.16", {"start": v(-5, -23.73) * mm, "mid": v(-4.75, -23.66) * mm, "end": v(-4.57, -23.48) * mm});
            skLineSegment(sketch, "E43.84.0.17", {"start": v(-5, -23.73) * mm, "end": v(-5.02, -23.72) * mm});
            skLineSegment(sketch, "E43.84.0.18", {"start": v(-5.02, -23.72) * mm, "end": v(-5, -23.73) * mm});
            skArc(sketch, "E43.85.0.0", {"start": v(-10.3, -22.45) * mm, "mid": v(-10.07, -22.98) * mm, "end": v(-9.79, -23.48) * mm});
            skPoint(sketch, "E43.85.0.1", {"position": v(-10.37, -20.63) * mm});
            skLineSegment(sketch, "E43.85.0.2", {"start": v(-10.42, -21.8) * mm, "end": v(-10.4, -21.55) * mm});
            skPoint(sketch, "E43.85.0.3", {"position": v(-8.27, -22.11) * mm});
            skPoint(sketch, "E43.85.0.4", {"position": v(-9.07, -23.73) * mm});
            skArc(sketch, "E43.85.0.5", {"start": v(-8.4, -22.45) * mm, "mid": v(-8.63, -22.98) * mm, "end": v(-8.91, -23.48) * mm});
            skPoint(sketch, "E43.85.0.6", {"position": v(-10.43, -22.11) * mm});
            skLineSegment(sketch, "E43.85.0.7", {"start": v(-8.28, -21.8) * mm, "end": v(-8.3, -21.55) * mm});
            skPoint(sketch, "E43.85.0.8", {"position": v(-9.64, -23.72) * mm});
            skArc(sketch, "E43.85.0.9", {"start": v(-10.4, -21.55) * mm, "mid": v(-10.62, -20.97) * mm, "end": v(-11.2, -20.73) * mm});
            skLineSegment(sketch, "E43.85.0.10", {"start": v(-7.5, -20.73) * mm, "end": v(-8.26, -20.73) * mm});
            skArc(sketch, "E43.85.0.11", {"start": v(-8.4, -22.45) * mm, "mid": v(-8.3, -22.13) * mm, "end": v(-8.28, -21.8) * mm});
            skArc(sketch, "E43.85.0.12", {"start": v(-10.42, -21.8) * mm, "mid": v(-10.4, -22.13) * mm, "end": v(-10.3, -22.45) * mm});
            skPoint(sketch, "E43.85.0.13", {"position": v(-9.26, -23.73) * mm});
            skArc(sketch, "E43.85.0.14", {"start": v(-9.79, -23.48) * mm, "mid": v(-9.6, -23.66) * mm, "end": v(-9.36, -23.72) * mm});
            skArc(sketch, "E43.85.0.15", {"start": v(-7.5, -20.73) * mm, "mid": v(-8.08, -20.97) * mm, "end": v(-8.3, -21.55) * mm});
            skArc(sketch, "E43.85.0.16", {"start": v(-9.35, -23.73) * mm, "mid": v(-9.1, -23.66) * mm, "end": v(-8.91, -23.48) * mm});
            skLineSegment(sketch, "E43.85.0.17", {"start": v(-9.35, -23.73) * mm, "end": v(-9.36, -23.72) * mm});
            skLineSegment(sketch, "E43.85.0.18", {"start": v(-9.36, -23.72) * mm, "end": v(-9.35, -23.73) * mm});
            skArc(sketch, "E43.86.0.0", {"start": v(-14.65, -22.45) * mm, "mid": v(-14.41, -22.98) * mm, "end": v(-14.13, -23.48) * mm});
            skPoint(sketch, "E43.86.0.1", {"position": v(-14.7, -20.63) * mm});
            skLineSegment(sketch, "E43.86.0.2", {"start": v(-14.76, -21.8) * mm, "end": v(-14.75, -21.55) * mm});
            skPoint(sketch, "E43.86.0.3", {"position": v(-12.61, -22.11) * mm});
            skPoint(sketch, "E43.86.0.4", {"position": v(-13.41, -23.73) * mm});
            skArc(sketch, "E43.86.0.5", {"start": v(-12.74, -22.45) * mm, "mid": v(-12.97, -22.98) * mm, "end": v(-13.25, -23.48) * mm});
            skPoint(sketch, "E43.86.0.6", {"position": v(-14.77, -22.11) * mm});
            skLineSegment(sketch, "E43.86.0.7", {"start": v(-12.63, -21.8) * mm, "end": v(-12.64, -21.55) * mm});
            skPoint(sketch, "E43.86.0.8", {"position": v(-13.98, -23.72) * mm});
            skArc(sketch, "E43.86.0.9", {"start": v(-14.75, -21.55) * mm, "mid": v(-14.97, -20.97) * mm, "end": v(-15.54, -20.73) * mm});
            skLineSegment(sketch, "E43.86.0.10", {"start": v(-11.85, -20.73) * mm, "end": v(-12.6, -20.73) * mm});
            skArc(sketch, "E43.86.0.11", {"start": v(-12.74, -22.45) * mm, "mid": v(-12.65, -22.13) * mm, "end": v(-12.63, -21.8) * mm});
            skArc(sketch, "E43.86.0.12", {"start": v(-14.76, -21.8) * mm, "mid": v(-14.74, -22.13) * mm, "end": v(-14.65, -22.45) * mm});
            skPoint(sketch, "E43.86.0.13", {"position": v(-13.6, -23.73) * mm});
            skArc(sketch, "E43.86.0.14", {"start": v(-14.13, -23.48) * mm, "mid": v(-13.95, -23.66) * mm, "end": v(-13.7, -23.72) * mm});
            skArc(sketch, "E43.86.0.15", {"start": v(-11.85, -20.73) * mm, "mid": v(-12.42, -20.97) * mm, "end": v(-12.64, -21.55) * mm});
            skArc(sketch, "E43.86.0.16", {"start": v(-13.7, -23.73) * mm, "mid": v(-13.44, -23.66) * mm, "end": v(-13.25, -23.48) * mm});
            skLineSegment(sketch, "E43.86.0.17", {"start": v(-13.7, -23.73) * mm, "end": v(-13.7, -23.72) * mm});
            skLineSegment(sketch, "E43.86.0.18", {"start": v(-13.7, -23.72) * mm, "end": v(-13.7, -23.73) * mm});
            skArc(sketch, "E43.87.0.0", {"start": v(-19, -22.45) * mm, "mid": v(-18.76, -22.98) * mm, "end": v(-18.48, -23.48) * mm});
            skPoint(sketch, "E43.87.0.1", {"position": v(-19.05, -20.63) * mm});
            skLineSegment(sketch, "E43.87.0.2", {"start": v(-19.1, -21.8) * mm, "end": v(-19.1, -21.55) * mm});
            skPoint(sketch, "E43.87.0.3", {"position": v(-16.96, -22.11) * mm});
            skPoint(sketch, "E43.87.0.4", {"position": v(-17.76, -23.73) * mm});
            skArc(sketch, "E43.87.0.5", {"start": v(-17.08, -22.45) * mm, "mid": v(-17.32, -22.98) * mm, "end": v(-17.6, -23.48) * mm});
            skPoint(sketch, "E43.87.0.6", {"position": v(-19.12, -22.11) * mm});
            skLineSegment(sketch, "E43.87.0.7", {"start": v(-16.97, -21.8) * mm, "end": v(-16.98, -21.55) * mm});
            skPoint(sketch, "E43.87.0.8", {"position": v(-18.32, -23.72) * mm});
            skArc(sketch, "E43.87.0.9", {"start": v(-19.1, -21.55) * mm, "mid": v(-19.31, -20.97) * mm, "end": v(-19.88, -20.73) * mm});
            skLineSegment(sketch, "E43.87.0.10", {"start": v(-16.2, -20.73) * mm, "end": v(-16.94, -20.73) * mm});
            skArc(sketch, "E43.87.0.11", {"start": v(-17.08, -22.45) * mm, "mid": v(-17, -22.13) * mm, "end": v(-16.97, -21.8) * mm});
            skArc(sketch, "E43.87.0.12", {"start": v(-19.1, -21.8) * mm, "mid": v(-19.08, -22.13) * mm, "end": v(-19, -22.45) * mm});
            skPoint(sketch, "E43.87.0.13", {"position": v(-17.95, -23.73) * mm});
            skArc(sketch, "E43.87.0.14", {"start": v(-18.48, -23.48) * mm, "mid": v(-18.3, -23.66) * mm, "end": v(-18.05, -23.72) * mm});
            skArc(sketch, "E43.87.0.15", {"start": v(-16.2, -20.73) * mm, "mid": v(-16.76, -20.97) * mm, "end": v(-16.98, -21.55) * mm});
            skArc(sketch, "E43.87.0.16", {"start": v(-18.04, -23.73) * mm, "mid": v(-17.78, -23.66) * mm, "end": v(-17.6, -23.48) * mm});
            skLineSegment(sketch, "E43.87.0.17", {"start": v(-18.04, -23.73) * mm, "end": v(-18.05, -23.72) * mm});
            skLineSegment(sketch, "E43.87.0.18", {"start": v(-18.05, -23.72) * mm, "end": v(-18.04, -23.73) * mm});
            skArc(sketch, "E43.88.0.0", {"start": v(-23.33, -22.45) * mm, "mid": v(-23.1, -22.98) * mm, "end": v(-22.82, -23.48) * mm});
            skPoint(sketch, "E43.88.0.1", {"position": v(-23.4, -20.63) * mm});
            skLineSegment(sketch, "E43.88.0.2", {"start": v(-23.45, -21.8) * mm, "end": v(-23.44, -21.55) * mm});
            skPoint(sketch, "E43.88.0.3", {"position": v(-21.3, -22.11) * mm});
            skPoint(sketch, "E43.88.0.4", {"position": v(-22.1, -23.73) * mm});
            skArc(sketch, "E43.88.0.5", {"start": v(-21.43, -22.45) * mm, "mid": v(-21.66, -22.98) * mm, "end": v(-21.94, -23.48) * mm});
            skPoint(sketch, "E43.88.0.6", {"position": v(-23.46, -22.11) * mm});
            skLineSegment(sketch, "E43.88.0.7", {"start": v(-21.31, -21.8) * mm, "end": v(-21.33, -21.55) * mm});
            skPoint(sketch, "E43.88.0.8", {"position": v(-22.67, -23.72) * mm});
            skArc(sketch, "E43.88.0.9", {"start": v(-23.44, -21.55) * mm, "mid": v(-23.65, -20.97) * mm, "end": v(-24.22, -20.73) * mm});
            skLineSegment(sketch, "E43.88.0.10", {"start": v(-20.54, -20.73) * mm, "end": v(-21.29, -20.73) * mm});
            skArc(sketch, "E43.88.0.11", {"start": v(-21.43, -22.45) * mm, "mid": v(-21.34, -22.13) * mm, "end": v(-21.31, -21.8) * mm});
            skArc(sketch, "E43.88.0.12", {"start": v(-23.45, -21.8) * mm, "mid": v(-23.43, -22.13) * mm, "end": v(-23.33, -22.45) * mm});
            skPoint(sketch, "E43.88.0.13", {"position": v(-22.3, -23.73) * mm});
            skArc(sketch, "E43.88.0.14", {"start": v(-22.82, -23.48) * mm, "mid": v(-22.64, -23.66) * mm, "end": v(-22.4, -23.72) * mm});
            skArc(sketch, "E43.88.0.15", {"start": v(-20.54, -20.73) * mm, "mid": v(-21.1, -20.97) * mm, "end": v(-21.33, -21.55) * mm});
            skArc(sketch, "E43.88.0.16", {"start": v(-22.38, -23.73) * mm, "mid": v(-22.13, -23.66) * mm, "end": v(-21.94, -23.48) * mm});
            skLineSegment(sketch, "E43.88.0.17", {"start": v(-22.38, -23.73) * mm, "end": v(-22.4, -23.72) * mm});
            skLineSegment(sketch, "E43.88.0.18", {"start": v(-22.4, -23.72) * mm, "end": v(-22.38, -23.73) * mm});
            skArc(sketch, "E43.89.0.0", {"start": v(-27.68, -22.45) * mm, "mid": v(-27.44, -22.98) * mm, "end": v(-27.16, -23.48) * mm});
            skPoint(sketch, "E43.89.0.1", {"position": v(-27.74, -20.63) * mm});
            skLineSegment(sketch, "E43.89.0.2", {"start": v(-27.79, -21.8) * mm, "end": v(-27.78, -21.55) * mm});
            skPoint(sketch, "E43.89.0.3", {"position": v(-25.64, -22.11) * mm});
            skPoint(sketch, "E43.89.0.4", {"position": v(-26.44, -23.73) * mm});
            skArc(sketch, "E43.89.0.5", {"start": v(-25.77, -22.45) * mm, "mid": v(-26, -22.98) * mm, "end": v(-26.28, -23.48) * mm});
            skPoint(sketch, "E43.89.0.6", {"position": v(-27.8, -22.11) * mm});
            skLineSegment(sketch, "E43.89.0.7", {"start": v(-25.66, -21.8) * mm, "end": v(-25.67, -21.55) * mm});
            skPoint(sketch, "E43.89.0.8", {"position": v(-27, -23.72) * mm});
            skArc(sketch, "E43.89.0.9", {"start": v(-27.78, -21.55) * mm, "mid": v(-28, -20.97) * mm, "end": v(-28.57, -20.73) * mm});
            skLineSegment(sketch, "E43.89.0.10", {"start": v(-24.88, -20.73) * mm, "end": v(-25.63, -20.73) * mm});
            skArc(sketch, "E43.89.0.11", {"start": v(-25.77, -22.45) * mm, "mid": v(-25.68, -22.13) * mm, "end": v(-25.66, -21.8) * mm});
            skArc(sketch, "E43.89.0.12", {"start": v(-27.79, -21.8) * mm, "mid": v(-27.77, -22.13) * mm, "end": v(-27.68, -22.45) * mm});
            skPoint(sketch, "E43.89.0.13", {"position": v(-26.63, -23.73) * mm});
            skArc(sketch, "E43.89.0.14", {"start": v(-27.16, -23.48) * mm, "mid": v(-26.98, -23.66) * mm, "end": v(-26.74, -23.72) * mm});
            skArc(sketch, "E43.89.0.15", {"start": v(-24.88, -20.73) * mm, "mid": v(-25.45, -20.97) * mm, "end": v(-25.67, -21.55) * mm});
            skArc(sketch, "E43.89.0.16", {"start": v(-26.72, -23.73) * mm, "mid": v(-26.47, -23.66) * mm, "end": v(-26.28, -23.48) * mm});
            skLineSegment(sketch, "E43.89.0.17", {"start": v(-26.72, -23.73) * mm, "end": v(-26.74, -23.72) * mm});
            skLineSegment(sketch, "E43.89.0.18", {"start": v(-26.74, -23.72) * mm, "end": v(-26.72, -23.73) * mm});
            skArc(sketch, "E43.90.0.0", {"start": v(-32.02, -22.45) * mm, "mid": v(-31.79, -22.98) * mm, "end": v(-31.5, -23.48) * mm});
            skPoint(sketch, "E43.90.0.1", {"position": v(-32.08, -20.63) * mm});
            skLineSegment(sketch, "E43.90.0.2", {"start": v(-32.13, -21.8) * mm, "end": v(-32.12, -21.55) * mm});
            skPoint(sketch, "E43.90.0.3", {"position": v(-29.99, -22.11) * mm});
            skPoint(sketch, "E43.90.0.4", {"position": v(-30.79, -23.73) * mm});
            skArc(sketch, "E43.90.0.5", {"start": v(-30.11, -22.45) * mm, "mid": v(-30.35, -22.98) * mm, "end": v(-30.63, -23.48) * mm});
            skPoint(sketch, "E43.90.0.6", {"position": v(-32.15, -22.11) * mm});
            skLineSegment(sketch, "E43.90.0.7", {"start": v(-30, -21.8) * mm, "end": v(-30.01, -21.55) * mm});
            skPoint(sketch, "E43.90.0.8", {"position": v(-31.35, -23.72) * mm});
            skArc(sketch, "E43.90.0.9", {"start": v(-32.12, -21.55) * mm, "mid": v(-32.34, -20.97) * mm, "end": v(-32.9, -20.73) * mm});
            skLineSegment(sketch, "E43.90.0.10", {"start": v(-29.23, -20.73) * mm, "end": v(-29.97, -20.73) * mm});
            skArc(sketch, "E43.90.0.11", {"start": v(-30.11, -22.45) * mm, "mid": v(-30.02, -22.13) * mm, "end": v(-30, -21.8) * mm});
            skArc(sketch, "E43.90.0.12", {"start": v(-32.13, -21.8) * mm, "mid": v(-32.11, -22.13) * mm, "end": v(-32.02, -22.45) * mm});
            skPoint(sketch, "E43.90.0.13", {"position": v(-30.98, -23.73) * mm});
            skArc(sketch, "E43.90.0.14", {"start": v(-31.5, -23.48) * mm, "mid": v(-31.32, -23.66) * mm, "end": v(-31.08, -23.72) * mm});
            skArc(sketch, "E43.90.0.15", {"start": v(-29.23, -20.73) * mm, "mid": v(-29.8, -20.97) * mm, "end": v(-30.01, -21.55) * mm});
            skArc(sketch, "E43.90.0.16", {"start": v(-31.07, -23.73) * mm, "mid": v(-30.82, -23.66) * mm, "end": v(-30.63, -23.48) * mm});
            skLineSegment(sketch, "E43.90.0.17", {"start": v(-31.07, -23.73) * mm, "end": v(-31.08, -23.72) * mm});
            skLineSegment(sketch, "E43.90.0.18", {"start": v(-31.08, -23.72) * mm, "end": v(-31.07, -23.73) * mm});
            skArc(sketch, "E43.91.0.0", {"start": v(-36.36, -22.45) * mm, "mid": v(-36.13, -22.98) * mm, "end": v(-35.85, -23.48) * mm});
            skPoint(sketch, "E43.91.0.1", {"position": v(-36.43, -20.63) * mm});
            skLineSegment(sketch, "E43.91.0.2", {"start": v(-36.48, -21.8) * mm, "end": v(-36.47, -21.55) * mm});
            skPoint(sketch, "E43.91.0.3", {"position": v(-34.33, -22.11) * mm});
            skPoint(sketch, "E43.91.0.4", {"position": v(-35.13, -23.73) * mm});
            skArc(sketch, "E43.91.0.5", {"start": v(-34.46, -22.45) * mm, "mid": v(-34.7, -22.98) * mm, "end": v(-34.97, -23.48) * mm});
            skPoint(sketch, "E43.91.0.6", {"position": v(-36.5, -22.11) * mm});
            skLineSegment(sketch, "E43.91.0.7", {"start": v(-34.35, -21.8) * mm, "end": v(-34.36, -21.55) * mm});
            skPoint(sketch, "E43.91.0.8", {"position": v(-35.7, -23.72) * mm});
            skArc(sketch, "E43.91.0.9", {"start": v(-36.47, -21.55) * mm, "mid": v(-36.68, -20.97) * mm, "end": v(-37.25, -20.73) * mm});
            skLineSegment(sketch, "E43.91.0.10", {"start": v(-33.57, -20.73) * mm, "end": v(-34.32, -20.73) * mm});
            skArc(sketch, "E43.91.0.11", {"start": v(-34.46, -22.45) * mm, "mid": v(-34.37, -22.13) * mm, "end": v(-34.35, -21.8) * mm});
            skArc(sketch, "E43.91.0.12", {"start": v(-36.48, -21.8) * mm, "mid": v(-36.46, -22.13) * mm, "end": v(-36.36, -22.45) * mm});
            skPoint(sketch, "E43.91.0.13", {"position": v(-35.32, -23.73) * mm});
            skArc(sketch, "E43.91.0.14", {"start": v(-35.85, -23.48) * mm, "mid": v(-35.67, -23.66) * mm, "end": v(-35.42, -23.72) * mm});
            skArc(sketch, "E43.91.0.15", {"start": v(-33.57, -20.73) * mm, "mid": v(-34.14, -20.97) * mm, "end": v(-34.36, -21.55) * mm});
            skArc(sketch, "E43.91.0.16", {"start": v(-35.41, -23.73) * mm, "mid": v(-35.16, -23.66) * mm, "end": v(-34.97, -23.48) * mm});
            skLineSegment(sketch, "E43.91.0.17", {"start": v(-35.41, -23.73) * mm, "end": v(-35.42, -23.72) * mm});
            skLineSegment(sketch, "E43.91.0.18", {"start": v(-35.42, -23.72) * mm, "end": v(-35.41, -23.73) * mm});
            skArc(sketch, "E43.92.0.0", {"start": v(-40.7, -22.45) * mm, "mid": v(-40.47, -22.98) * mm, "end": v(-40.2, -23.48) * mm});
            skPoint(sketch, "E43.92.0.1", {"position": v(-40.77, -20.63) * mm});
            skLineSegment(sketch, "E43.92.0.2", {"start": v(-40.82, -21.8) * mm, "end": v(-40.8, -21.55) * mm});
            skPoint(sketch, "E43.92.0.3", {"position": v(-38.67, -22.11) * mm});
            skPoint(sketch, "E43.92.0.4", {"position": v(-39.47, -23.73) * mm});
            skArc(sketch, "E43.92.0.5", {"start": v(-38.8, -22.45) * mm, "mid": v(-39.03, -22.98) * mm, "end": v(-39.31, -23.48) * mm});
            skPoint(sketch, "E43.92.0.6", {"position": v(-40.83, -22.11) * mm});
            skLineSegment(sketch, "E43.92.0.7", {"start": v(-38.69, -21.8) * mm, "end": v(-38.7, -21.55) * mm});
            skPoint(sketch, "E43.92.0.8", {"position": v(-40.04, -23.72) * mm});
            skArc(sketch, "E43.92.0.9", {"start": v(-40.8, -21.55) * mm, "mid": v(-41.03, -20.97) * mm, "end": v(-41.6, -20.73) * mm});
            skLineSegment(sketch, "E43.92.0.10", {"start": v(-37.91, -20.73) * mm, "end": v(-38.66, -20.73) * mm});
            skArc(sketch, "E43.92.0.11", {"start": v(-38.8, -22.45) * mm, "mid": v(-38.7, -22.13) * mm, "end": v(-38.69, -21.8) * mm});
            skArc(sketch, "E43.92.0.12", {"start": v(-40.82, -21.8) * mm, "mid": v(-40.8, -22.13) * mm, "end": v(-40.7, -22.45) * mm});
            skPoint(sketch, "E43.92.0.13", {"position": v(-39.66, -23.73) * mm});
            skArc(sketch, "E43.92.0.14", {"start": v(-40.2, -23.48) * mm, "mid": v(-40.01, -23.66) * mm, "end": v(-39.77, -23.72) * mm});
            skArc(sketch, "E43.92.0.15", {"start": v(-37.91, -20.73) * mm, "mid": v(-38.48, -20.97) * mm, "end": v(-38.7, -21.55) * mm});
            skArc(sketch, "E43.92.0.16", {"start": v(-39.75, -23.73) * mm, "mid": v(-39.5, -23.66) * mm, "end": v(-39.31, -23.48) * mm});
            skLineSegment(sketch, "E43.92.0.17", {"start": v(-39.75, -23.73) * mm, "end": v(-39.77, -23.72) * mm});
            skLineSegment(sketch, "E43.92.0.18", {"start": v(-39.77, -23.72) * mm, "end": v(-39.75, -23.73) * mm});
            skArc(sketch, "E43.93.0.0", {"start": v(-45.05, -22.45) * mm, "mid": v(-44.82, -22.98) * mm, "end": v(-44.54, -23.48) * mm});
            skPoint(sketch, "E43.93.0.1", {"position": v(-45.11, -20.63) * mm});
            skLineSegment(sketch, "E43.93.0.2", {"start": v(-45.16, -21.8) * mm, "end": v(-45.15, -21.55) * mm});
            skPoint(sketch, "E43.93.0.3", {"position": v(-43.02, -22.11) * mm});
            skPoint(sketch, "E43.93.0.4", {"position": v(-43.82, -23.73) * mm});
            skArc(sketch, "E43.93.0.5", {"start": v(-43.14, -22.45) * mm, "mid": v(-43.38, -22.98) * mm, "end": v(-43.66, -23.48) * mm});
            skPoint(sketch, "E43.93.0.6", {"position": v(-45.18, -22.11) * mm});
            skLineSegment(sketch, "E43.93.0.7", {"start": v(-43.03, -21.8) * mm, "end": v(-43.04, -21.55) * mm});
            skPoint(sketch, "E43.93.0.8", {"position": v(-44.38, -23.72) * mm});
            skArc(sketch, "E43.93.0.9", {"start": v(-45.15, -21.55) * mm, "mid": v(-45.37, -20.97) * mm, "end": v(-45.94, -20.73) * mm});
            skLineSegment(sketch, "E43.93.0.10", {"start": v(-42.26, -20.73) * mm, "end": v(-43, -20.73) * mm});
            skArc(sketch, "E43.93.0.11", {"start": v(-43.14, -22.45) * mm, "mid": v(-43.05, -22.13) * mm, "end": v(-43.03, -21.8) * mm});
            skArc(sketch, "E43.93.0.12", {"start": v(-45.16, -21.8) * mm, "mid": v(-45.14, -22.13) * mm, "end": v(-45.05, -22.45) * mm});
            skPoint(sketch, "E43.93.0.13", {"position": v(-44, -23.73) * mm});
            skArc(sketch, "E43.93.0.14", {"start": v(-44.54, -23.48) * mm, "mid": v(-44.35, -23.66) * mm, "end": v(-44.1, -23.72) * mm});
            skArc(sketch, "E43.93.0.15", {"start": v(-42.26, -20.73) * mm, "mid": v(-42.83, -20.97) * mm, "end": v(-43.04, -21.55) * mm});
            skArc(sketch, "E43.93.0.16", {"start": v(-44.1, -23.73) * mm, "mid": v(-43.85, -23.66) * mm, "end": v(-43.66, -23.48) * mm});
            skLineSegment(sketch, "E43.93.0.17", {"start": v(-44.1, -23.73) * mm, "end": v(-44.1, -23.72) * mm});
            skLineSegment(sketch, "E43.93.0.18", {"start": v(-44.1, -23.72) * mm, "end": v(-44.1, -23.73) * mm});
            skArc(sketch, "E43.94.0.0", {"start": v(-49.4, -22.45) * mm, "mid": v(-49.16, -22.98) * mm, "end": v(-48.88, -23.48) * mm});
            skPoint(sketch, "E43.94.0.1", {"position": v(-49.46, -20.63) * mm});
            skLineSegment(sketch, "E43.94.0.2", {"start": v(-49.5, -21.8) * mm, "end": v(-49.5, -21.55) * mm});
            skPoint(sketch, "E43.94.0.3", {"position": v(-47.36, -22.11) * mm});
            skPoint(sketch, "E43.94.0.4", {"position": v(-48.16, -23.73) * mm});
            skArc(sketch, "E43.94.0.5", {"start": v(-47.49, -22.45) * mm, "mid": v(-47.72, -22.98) * mm, "end": v(-48, -23.48) * mm});
            skPoint(sketch, "E43.94.0.6", {"position": v(-49.52, -22.11) * mm});
            skLineSegment(sketch, "E43.94.0.7", {"start": v(-47.38, -21.8) * mm, "end": v(-47.39, -21.55) * mm});
            skPoint(sketch, "E43.94.0.8", {"position": v(-48.73, -23.72) * mm});
            skArc(sketch, "E43.94.0.9", {"start": v(-49.5, -21.55) * mm, "mid": v(-49.71, -20.97) * mm, "end": v(-50.28, -20.73) * mm});
            skLineSegment(sketch, "E43.94.0.10", {"start": v(-46.6, -20.73) * mm, "end": v(-47.35, -20.73) * mm});
            skArc(sketch, "E43.94.0.11", {"start": v(-47.49, -22.45) * mm, "mid": v(-47.4, -22.13) * mm, "end": v(-47.38, -21.8) * mm});
            skArc(sketch, "E43.94.0.12", {"start": v(-49.5, -21.8) * mm, "mid": v(-49.49, -22.13) * mm, "end": v(-49.4, -22.45) * mm});
            skPoint(sketch, "E43.94.0.13", {"position": v(-48.35, -23.73) * mm});
            skArc(sketch, "E43.94.0.14", {"start": v(-48.88, -23.48) * mm, "mid": v(-48.7, -23.66) * mm, "end": v(-48.45, -23.72) * mm});
            skArc(sketch, "E43.94.0.15", {"start": v(-46.6, -20.73) * mm, "mid": v(-47.17, -20.97) * mm, "end": v(-47.39, -21.55) * mm});
            skArc(sketch, "E43.94.0.16", {"start": v(-48.44, -23.73) * mm, "mid": v(-48.19, -23.66) * mm, "end": v(-48, -23.48) * mm});
            skLineSegment(sketch, "E43.94.0.17", {"start": v(-48.44, -23.73) * mm, "end": v(-48.45, -23.72) * mm});
            skLineSegment(sketch, "E43.94.0.18", {"start": v(-48.45, -23.72) * mm, "end": v(-48.44, -23.73) * mm});
            skLineSegment(sketch, "E43.direction1", {"start": v(354.57, -19.98) * mm, "end": v(350.22, -19.98) * mm, "construction": true});
            skArc(sketch, "E44.0.95.0", {"start": v(-53.74, -22.45) * mm, "mid": v(-53.5, -22.98) * mm, "end": v(-53.22, -23.48) * mm});
            skPoint(sketch, "E44.4.95.0", {"position": v(-53.8, -20.63) * mm});
            skLineSegment(sketch, "E44.5.95.0", {"start": v(-53.85, -21.8) * mm, "end": v(-53.84, -21.55) * mm});
            skPoint(sketch, "E44.8.95.0", {"position": v(-51.7, -22.11) * mm});
            skPoint(sketch, "E44.9.95.0", {"position": v(-52.5, -23.73) * mm});
            skArc(sketch, "E44.10.95.0", {"start": v(-51.83, -22.45) * mm, "mid": v(-52.06, -22.98) * mm, "end": v(-52.34, -23.48) * mm});
            skPoint(sketch, "E44.14.95.0", {"position": v(-53.86, -22.11) * mm});
            skLineSegment(sketch, "E44.15.95.0", {"start": v(-51.72, -21.8) * mm, "end": v(-51.73, -21.55) * mm});
            skPoint(sketch, "E44.18.95.0", {"position": v(-53.07, -23.72) * mm});
            skArc(sketch, "E44.19.95.0", {"start": v(-53.84, -21.55) * mm, "mid": v(-54.06, -20.97) * mm, "end": v(-54.63, -20.73) * mm});
            skLineSegment(sketch, "E44.23.95.0", {"start": v(-50.94, -20.73) * mm, "end": v(-51.69, -20.73) * mm});
            skArc(sketch, "E44.26.95.0", {"start": v(-51.83, -22.45) * mm, "mid": v(-51.74, -22.13) * mm, "end": v(-51.72, -21.8) * mm});
            skArc(sketch, "E44.30.95.0", {"start": v(-53.85, -21.8) * mm, "mid": v(-53.83, -22.13) * mm, "end": v(-53.74, -22.45) * mm});
            skPoint(sketch, "E44.34.95.0", {"position": v(-52.7, -23.73) * mm});
            skArc(sketch, "E44.35.95.0", {"start": v(-53.22, -23.48) * mm, "mid": v(-53.04, -23.66) * mm, "end": v(-52.8, -23.72) * mm});
            skArc(sketch, "E44.39.95.0", {"start": v(-50.94, -20.73) * mm, "mid": v(-51.51, -20.97) * mm, "end": v(-51.73, -21.55) * mm});
            skArc(sketch, "E44.43.95.0", {"start": v(-52.78, -23.73) * mm, "mid": v(-52.53, -23.66) * mm, "end": v(-52.34, -23.48) * mm});
            skLineSegment(sketch, "E44.47.95.0", {"start": v(-52.78, -23.73) * mm, "end": v(-52.8, -23.72) * mm});
            skLineSegment(sketch, "E44.50.95.0", {"start": v(-52.8, -23.72) * mm, "end": v(-52.78, -23.73) * mm});
            skArc(sketch, "E44.0.96.0", {"start": v(-58.08, -22.45) * mm, "mid": v(-57.85, -22.98) * mm, "end": v(-57.57, -23.48) * mm});
            skPoint(sketch, "E44.4.96.0", {"position": v(-58.14, -20.63) * mm});
            skLineSegment(sketch, "E44.5.96.0", {"start": v(-58.2, -21.8) * mm, "end": v(-58.18, -21.55) * mm});
            skPoint(sketch, "E44.8.96.0", {"position": v(-56.05, -22.11) * mm});
            skPoint(sketch, "E44.9.96.0", {"position": v(-56.85, -23.73) * mm});
            skArc(sketch, "E44.10.96.0", {"start": v(-56.17, -22.45) * mm, "mid": v(-56.4, -22.98) * mm, "end": v(-56.69, -23.48) * mm});
            skPoint(sketch, "E44.14.96.0", {"position": v(-58.2, -22.11) * mm});
            skLineSegment(sketch, "E44.15.96.0", {"start": v(-56.06, -21.8) * mm, "end": v(-56.07, -21.55) * mm});
            skPoint(sketch, "E44.18.96.0", {"position": v(-57.41, -23.72) * mm});
            skArc(sketch, "E44.19.96.0", {"start": v(-58.18, -21.55) * mm, "mid": v(-58.4, -20.97) * mm, "end": v(-58.97, -20.73) * mm});
            skLineSegment(sketch, "E44.23.96.0", {"start": v(-55.29, -20.73) * mm, "end": v(-56.03, -20.73) * mm});
            skArc(sketch, "E44.26.96.0", {"start": v(-56.17, -22.45) * mm, "mid": v(-56.08, -22.13) * mm, "end": v(-56.06, -21.8) * mm});
            skArc(sketch, "E44.30.96.0", {"start": v(-58.2, -21.8) * mm, "mid": v(-58.17, -22.13) * mm, "end": v(-58.08, -22.45) * mm});
            skPoint(sketch, "E44.34.96.0", {"position": v(-57.04, -23.73) * mm});
            skArc(sketch, "E44.35.96.0", {"start": v(-57.57, -23.48) * mm, "mid": v(-57.38, -23.66) * mm, "end": v(-57.14, -23.72) * mm});
            skArc(sketch, "E44.39.96.0", {"start": v(-55.29, -20.73) * mm, "mid": v(-55.86, -20.97) * mm, "end": v(-56.07, -21.55) * mm});
            skArc(sketch, "E44.43.96.0", {"start": v(-57.13, -23.73) * mm, "mid": v(-56.88, -23.66) * mm, "end": v(-56.69, -23.48) * mm});
            skLineSegment(sketch, "E44.47.96.0", {"start": v(-57.13, -23.73) * mm, "end": v(-57.14, -23.72) * mm});
            skLineSegment(sketch, "E44.50.96.0", {"start": v(-57.14, -23.72) * mm, "end": v(-57.13, -23.73) * mm});
            skArc(sketch, "E44.0.97.0", {"start": v(-62.43, -22.45) * mm, "mid": v(-62.19, -22.98) * mm, "end": v(-61.9, -23.48) * mm});
            skPoint(sketch, "E44.4.97.0", {"position": v(-62.49, -20.63) * mm});
            skLineSegment(sketch, "E44.5.97.0", {"start": v(-62.54, -21.8) * mm, "end": v(-62.53, -21.55) * mm});
            skPoint(sketch, "E44.8.97.0", {"position": v(-60.4, -22.11) * mm});
            skPoint(sketch, "E44.9.97.0", {"position": v(-61.19, -23.73) * mm});
            skArc(sketch, "E44.10.97.0", {"start": v(-60.52, -22.45) * mm, "mid": v(-60.75, -22.98) * mm, "end": v(-61.03, -23.48) * mm});
            skPoint(sketch, "E44.14.97.0", {"position": v(-62.55, -22.11) * mm});
            skLineSegment(sketch, "E44.15.97.0", {"start": v(-60.4, -21.8) * mm, "end": v(-60.42, -21.55) * mm});
            skPoint(sketch, "E44.18.97.0", {"position": v(-61.76, -23.72) * mm});
            skArc(sketch, "E44.19.97.0", {"start": v(-62.53, -21.55) * mm, "mid": v(-62.74, -20.97) * mm, "end": v(-63.31, -20.73) * mm});
            skLineSegment(sketch, "E44.23.97.0", {"start": v(-59.63, -20.73) * mm, "end": v(-60.38, -20.73) * mm});
            skArc(sketch, "E44.26.97.0", {"start": v(-60.52, -22.45) * mm, "mid": v(-60.43, -22.13) * mm, "end": v(-60.4, -21.8) * mm});
            skArc(sketch, "E44.30.97.0", {"start": v(-62.54, -21.8) * mm, "mid": v(-62.52, -22.13) * mm, "end": v(-62.43, -22.45) * mm});
            skPoint(sketch, "E44.34.97.0", {"position": v(-61.38, -23.73) * mm});
            skArc(sketch, "E44.35.97.0", {"start": v(-61.9, -23.48) * mm, "mid": v(-61.73, -23.66) * mm, "end": v(-61.48, -23.72) * mm});
            skArc(sketch, "E44.39.97.0", {"start": v(-59.63, -20.73) * mm, "mid": v(-60.2, -20.97) * mm, "end": v(-60.42, -21.55) * mm});
            skArc(sketch, "E44.43.97.0", {"start": v(-61.47, -23.73) * mm, "mid": v(-61.22, -23.66) * mm, "end": v(-61.03, -23.48) * mm});
            skLineSegment(sketch, "E44.47.97.0", {"start": v(-61.47, -23.73) * mm, "end": v(-61.48, -23.72) * mm});
            skLineSegment(sketch, "E44.50.97.0", {"start": v(-61.48, -23.72) * mm, "end": v(-61.47, -23.73) * mm});
            skArc(sketch, "E44.0.98.0", {"start": v(-66.77, -22.45) * mm, "mid": v(-66.53, -22.98) * mm, "end": v(-66.25, -23.48) * mm});
            skPoint(sketch, "E44.4.98.0", {"position": v(-66.83, -20.63) * mm});
            skLineSegment(sketch, "E44.5.98.0", {"start": v(-66.88, -21.8) * mm, "end": v(-66.87, -21.55) * mm});
            skPoint(sketch, "E44.8.98.0", {"position": v(-64.73, -22.11) * mm});
            skPoint(sketch, "E44.9.98.0", {"position": v(-65.53, -23.73) * mm});
            skArc(sketch, "E44.10.98.0", {"start": v(-64.86, -22.45) * mm, "mid": v(-65.1, -22.98) * mm, "end": v(-65.37, -23.48) * mm});
            skPoint(sketch, "E44.14.98.0", {"position": v(-66.9, -22.11) * mm});
            skLineSegment(sketch, "E44.15.98.0", {"start": v(-64.75, -21.8) * mm, "end": v(-64.76, -21.55) * mm});
            skPoint(sketch, "E44.18.98.0", {"position": v(-66.1, -23.72) * mm});
            skArc(sketch, "E44.19.98.0", {"start": v(-66.87, -21.55) * mm, "mid": v(-67.09, -20.97) * mm, "end": v(-67.66, -20.73) * mm});
            skLineSegment(sketch, "E44.23.98.0", {"start": v(-63.97, -20.73) * mm, "end": v(-64.72, -20.73) * mm});
            skArc(sketch, "E44.26.98.0", {"start": v(-64.86, -22.45) * mm, "mid": v(-64.77, -22.13) * mm, "end": v(-64.75, -21.8) * mm});
            skArc(sketch, "E44.30.98.0", {"start": v(-66.88, -21.8) * mm, "mid": v(-66.86, -22.13) * mm, "end": v(-66.77, -22.45) * mm});
            skPoint(sketch, "E44.34.98.0", {"position": v(-65.72, -23.73) * mm});
            skArc(sketch, "E44.35.98.0", {"start": v(-66.25, -23.48) * mm, "mid": v(-66.07, -23.66) * mm, "end": v(-65.83, -23.72) * mm});
            skArc(sketch, "E44.39.98.0", {"start": v(-63.97, -20.73) * mm, "mid": v(-64.54, -20.97) * mm, "end": v(-64.76, -21.55) * mm});
            skArc(sketch, "E44.43.98.0", {"start": v(-65.81, -23.73) * mm, "mid": v(-65.56, -23.66) * mm, "end": v(-65.37, -23.48) * mm});
            skLineSegment(sketch, "E44.47.98.0", {"start": v(-65.81, -23.73) * mm, "end": v(-65.83, -23.72) * mm});
            skLineSegment(sketch, "E44.50.98.0", {"start": v(-65.83, -23.72) * mm, "end": v(-65.81, -23.73) * mm});
            skArc(sketch, "E44.0.99.0", {"start": v(-70.87, -23) * mm, "mid": v(-70.74, -23.24) * mm, "end": v(-70.6, -23.48) * mm});
            skPoint(sketch, "E44.8.99.0", {"position": v(-69.08, -22.11) * mm});
            skPoint(sketch, "E44.9.99.0", {"position": v(-69.88, -23.73) * mm});
            skArc(sketch, "E44.10.99.0", {"start": v(-69.2, -22.45) * mm, "mid": v(-69.44, -22.98) * mm, "end": v(-69.72, -23.48) * mm});
            skLineSegment(sketch, "E44.15.99.0", {"start": v(-69.1, -21.8) * mm, "end": v(-69.1, -21.55) * mm});
            skPoint(sketch, "E44.18.99.0", {"position": v(-70.44, -23.72) * mm});
            skLineSegment(sketch, "E44.23.99.0", {"start": v(-68.32, -20.73) * mm, "end": v(-69.06, -20.73) * mm});
            skArc(sketch, "E44.26.99.0", {"start": v(-69.2, -22.45) * mm, "mid": v(-69.11, -22.13) * mm, "end": v(-69.1, -21.8) * mm});
            skPoint(sketch, "E44.34.99.0", {"position": v(-70.07, -23.73) * mm});
            skArc(sketch, "E44.35.99.0", {"start": v(-70.6, -23.48) * mm, "mid": v(-70.41, -23.66) * mm, "end": v(-70.17, -23.72) * mm});
            skArc(sketch, "E44.39.99.0", {"start": v(-68.32, -20.73) * mm, "mid": v(-68.89, -20.97) * mm, "end": v(-69.1, -21.55) * mm});
            skArc(sketch, "E44.43.99.0", {"start": v(-70.16, -23.73) * mm, "mid": v(-69.9, -23.66) * mm, "end": v(-69.72, -23.48) * mm});
            skLineSegment(sketch, "E44.47.99.0", {"start": v(-70.16, -23.73) * mm, "end": v(-70.17, -23.72) * mm});
            skLineSegment(sketch, "E44.50.99.0", {"start": v(-70.17, -23.72) * mm, "end": v(-70.16, -23.73) * mm});
            skLineSegment(sketch, "E45", {"start": v(-70.87, -20.73) * mm, "end": v(-70.87, -23) * mm});
            skLineSegment(sketch, "E46", {"start": v(360.93, -20.73) * mm, "end": v(360.93, -21.26) * mm});
            skSolve(sketch);
        }
        {
            var Q0;
            Q0=makeQuery(id+"F5.imprint","IMPRINT",FACE,{"disambiguationData":[TD([[makeQuery(id+"F5.imprint","IMPRINT",EDGE,{"derivedFrom":sQuery(id+"F5.wireOp",EDGE,"E29.trimOffspring")}),1.0]])]});
            var Q1;
            Q1=makeQuery(id+"F5.imprint","IMPRINT",FACE,{"disambiguationData":[TD([[makeQuery(id+"F5.imprint","IMPRINT",EDGE,{"derivedFrom":sQuery(id+"F5.wireOp",EDGE,"E43.1.0.0")}),1.0]])]});
            var Q2;
            Q2=makeQuery(id+"F5.imprint","IMPRINT",FACE,{"disambiguationData":[TD([[makeQuery(id+"F5.imprint","IMPRINT",EDGE,{"derivedFrom":sQuery(id+"F5.wireOp",EDGE,"E43.2.0.0")}),1.0]])]});
            var Q3;
            Q3=makeQuery(id+"F5.imprint","IMPRINT",FACE,{"disambiguationData":[TD([[makeQuery(id+"F5.imprint","IMPRINT",EDGE,{"derivedFrom":sQuery(id+"F5.wireOp",EDGE,"E43.3.0.0")}),1.0]])]});
            var Q4;
            Q4=makeQuery(id+"F5.imprint","IMPRINT",FACE,{"disambiguationData":[TD([[makeQuery(id+"F5.imprint","IMPRINT",EDGE,{"derivedFrom":sQuery(id+"F5.wireOp",EDGE,"E43.4.0.0")}),1.0]])]});
            var Q5;
            Q5=makeQuery(id+"F5.imprint","IMPRINT",FACE,{"disambiguationData":[TD([[makeQuery(id+"F5.imprint","IMPRINT",EDGE,{"derivedFrom":sQuery(id+"F5.wireOp",EDGE,"E43.5.0.0")}),1.0]])]});
            var Q6;
            Q6=makeQuery(id+"F5.imprint","IMPRINT",FACE,{"disambiguationData":[TD([[makeQuery(id+"F5.imprint","IMPRINT",EDGE,{"derivedFrom":sQuery(id+"F5.wireOp",EDGE,"E43.6.0.0")}),1.0]])]});
            var Q7;
            Q7=makeQuery(id+"F5.imprint","IMPRINT",FACE,{"disambiguationData":[TD([[makeQuery(id+"F5.imprint","IMPRINT",EDGE,{"derivedFrom":sQuery(id+"F5.wireOp",EDGE,"E43.7.0.0")}),1.0]])]});
            var Q8;
            Q8=makeQuery(id+"F5.imprint","IMPRINT",FACE,{"disambiguationData":[TD([[makeQuery(id+"F5.imprint","IMPRINT",EDGE,{"derivedFrom":sQuery(id+"F5.wireOp",EDGE,"E43.8.0.0")}),1.0]])]});
            var Q9;
            Q9=makeQuery(id+"F5.imprint","IMPRINT",FACE,{"disambiguationData":[TD([[makeQuery(id+"F5.imprint","IMPRINT",EDGE,{"derivedFrom":sQuery(id+"F5.wireOp",EDGE,"E43.9.0.0")}),1.0]])]});
            var Q10;
            Q10=makeQuery(id+"F5.imprint","IMPRINT",FACE,{"disambiguationData":[TD([[makeQuery(id+"F5.imprint","IMPRINT",EDGE,{"derivedFrom":sQuery(id+"F5.wireOp",EDGE,"E43.10.0.0")}),1.0]])]});
            var Q11;
            Q11=makeQuery(id+"F5.imprint","IMPRINT",FACE,{"disambiguationData":[TD([[makeQuery(id+"F5.imprint","IMPRINT",EDGE,{"derivedFrom":sQuery(id+"F5.wireOp",EDGE,"E43.11.0.0")}),1.0]])]});
            var Q12;
            Q12=makeQuery(id+"F5.imprint","IMPRINT",FACE,{"disambiguationData":[TD([[makeQuery(id+"F5.imprint","IMPRINT",EDGE,{"derivedFrom":sQuery(id+"F5.wireOp",EDGE,"E43.12.0.0")}),1.0]])]});
            var Q13;
            Q13=makeQuery(id+"F5.imprint","IMPRINT",FACE,{"disambiguationData":[TD([[makeQuery(id+"F5.imprint","IMPRINT",EDGE,{"derivedFrom":sQuery(id+"F5.wireOp",EDGE,"E43.13.0.0")}),1.0]])]});
            var Q14;
            Q14=makeQuery(id+"F5.imprint","IMPRINT",FACE,{"disambiguationData":[TD([[makeQuery(id+"F5.imprint","IMPRINT",EDGE,{"derivedFrom":sQuery(id+"F5.wireOp",EDGE,"E43.14.0.0")}),1.0]])]});
            var Q15;
            Q15=makeQuery(id+"F5.imprint","IMPRINT",FACE,{"disambiguationData":[TD([[makeQuery(id+"F5.imprint","IMPRINT",EDGE,{"derivedFrom":sQuery(id+"F5.wireOp",EDGE,"E43.15.0.0")}),1.0]])]});
            var Q16;
            Q16=makeQuery(id+"F5.imprint","IMPRINT",FACE,{"disambiguationData":[TD([[makeQuery(id+"F5.imprint","IMPRINT",EDGE,{"derivedFrom":sQuery(id+"F5.wireOp",EDGE,"E43.16.0.0")}),1.0]])]});
            var Q17;
            Q17=makeQuery(id+"F5.imprint","IMPRINT",FACE,{"disambiguationData":[TD([[makeQuery(id+"F5.imprint","IMPRINT",EDGE,{"derivedFrom":sQuery(id+"F5.wireOp",EDGE,"E43.17.0.0")}),1.0]])]});
            var Q18;
            Q18=makeQuery(id+"F5.imprint","IMPRINT",FACE,{"disambiguationData":[TD([[makeQuery(id+"F5.imprint","IMPRINT",EDGE,{"derivedFrom":sQuery(id+"F5.wireOp",EDGE,"E43.18.0.0")}),1.0]])]});
            var Q19;
            Q19=makeQuery(id+"F5.imprint","IMPRINT",FACE,{"disambiguationData":[TD([[makeQuery(id+"F5.imprint","IMPRINT",EDGE,{"derivedFrom":sQuery(id+"F5.wireOp",EDGE,"E43.19.0.0")}),1.0]])]});
            var Q20;
            Q20=makeQuery(id+"F5.imprint","IMPRINT",FACE,{"disambiguationData":[TD([[makeQuery(id+"F5.imprint","IMPRINT",EDGE,{"derivedFrom":sQuery(id+"F5.wireOp",EDGE,"E43.20.0.0")}),1.0]])]});
            var Q21;
            Q21=makeQuery(id+"F5.imprint","IMPRINT",FACE,{"disambiguationData":[TD([[makeQuery(id+"F5.imprint","IMPRINT",EDGE,{"derivedFrom":sQuery(id+"F5.wireOp",EDGE,"E43.21.0.0")}),1.0]])]});
            var Q22;
            Q22=makeQuery(id+"F5.imprint","IMPRINT",FACE,{"disambiguationData":[TD([[makeQuery(id+"F5.imprint","IMPRINT",EDGE,{"derivedFrom":sQuery(id+"F5.wireOp",EDGE,"E43.22.0.0")}),1.0]])]});
            var Q23;
            Q23=makeQuery(id+"F5.imprint","IMPRINT",FACE,{"disambiguationData":[TD([[makeQuery(id+"F5.imprint","IMPRINT",EDGE,{"derivedFrom":sQuery(id+"F5.wireOp",EDGE,"E43.23.0.0")}),1.0]])]});
            var Q24;
            Q24=makeQuery(id+"F5.imprint","IMPRINT",FACE,{"disambiguationData":[TD([[makeQuery(id+"F5.imprint","IMPRINT",EDGE,{"derivedFrom":sQuery(id+"F5.wireOp",EDGE,"E43.24.0.0")}),1.0]])]});
            var Q25;
            Q25=makeQuery(id+"F5.imprint","IMPRINT",FACE,{"disambiguationData":[TD([[makeQuery(id+"F5.imprint","IMPRINT",EDGE,{"derivedFrom":sQuery(id+"F5.wireOp",EDGE,"E43.25.0.0")}),1.0]])]});
            var Q26;
            Q26=makeQuery(id+"F5.imprint","IMPRINT",FACE,{"disambiguationData":[TD([[makeQuery(id+"F5.imprint","IMPRINT",EDGE,{"derivedFrom":sQuery(id+"F5.wireOp",EDGE,"E43.26.0.0")}),1.0]])]});
            var Q27;
            Q27=makeQuery(id+"F5.imprint","IMPRINT",FACE,{"disambiguationData":[TD([[makeQuery(id+"F5.imprint","IMPRINT",EDGE,{"derivedFrom":sQuery(id+"F5.wireOp",EDGE,"E43.27.0.0")}),1.0]])]});
            var Q28;
            Q28=makeQuery(id+"F5.imprint","IMPRINT",FACE,{"disambiguationData":[TD([[makeQuery(id+"F5.imprint","IMPRINT",EDGE,{"derivedFrom":sQuery(id+"F5.wireOp",EDGE,"E43.28.0.0")}),1.0]])]});
            var Q29;
            Q29=makeQuery(id+"F5.imprint","IMPRINT",FACE,{"disambiguationData":[TD([[makeQuery(id+"F5.imprint","IMPRINT",EDGE,{"derivedFrom":sQuery(id+"F5.wireOp",EDGE,"E43.29.0.0")}),1.0]])]});
            var Q30;
            Q30=makeQuery(id+"F5.imprint","IMPRINT",FACE,{"disambiguationData":[TD([[makeQuery(id+"F5.imprint","IMPRINT",EDGE,{"derivedFrom":sQuery(id+"F5.wireOp",EDGE,"E43.30.0.0")}),1.0]])]});
            var Q31;
            Q31=makeQuery(id+"F5.imprint","IMPRINT",FACE,{"disambiguationData":[TD([[makeQuery(id+"F5.imprint","IMPRINT",EDGE,{"derivedFrom":sQuery(id+"F5.wireOp",EDGE,"E43.31.0.0")}),1.0]])]});
            var Q32;
            Q32=makeQuery(id+"F5.imprint","IMPRINT",FACE,{"disambiguationData":[TD([[makeQuery(id+"F5.imprint","IMPRINT",EDGE,{"derivedFrom":sQuery(id+"F5.wireOp",EDGE,"E43.32.0.0")}),1.0]])]});
            var Q33;
            Q33=makeQuery(id+"F5.imprint","IMPRINT",FACE,{"disambiguationData":[TD([[makeQuery(id+"F5.imprint","IMPRINT",EDGE,{"derivedFrom":sQuery(id+"F5.wireOp",EDGE,"E43.33.0.0")}),1.0]])]});
            var Q34;
            Q34=makeQuery(id+"F5.imprint","IMPRINT",FACE,{"disambiguationData":[TD([[makeQuery(id+"F5.imprint","IMPRINT",EDGE,{"derivedFrom":sQuery(id+"F5.wireOp",EDGE,"E43.34.0.0")}),1.0]])]});
            var Q35;
            Q35=makeQuery(id+"F5.imprint","IMPRINT",FACE,{"disambiguationData":[TD([[makeQuery(id+"F5.imprint","IMPRINT",EDGE,{"derivedFrom":sQuery(id+"F5.wireOp",EDGE,"E43.39.0.0")}),1.0]])]});
            var Q36;
            Q36=makeQuery(id+"F5.imprint","IMPRINT",FACE,{"disambiguationData":[TD([[makeQuery(id+"F5.imprint","IMPRINT",EDGE,{"derivedFrom":sQuery(id+"F5.wireOp",EDGE,"E43.40.0.0")}),1.0]])]});
            var Q37;
            Q37=makeQuery(id+"F5.imprint","IMPRINT",FACE,{"disambiguationData":[TD([[makeQuery(id+"F5.imprint","IMPRINT",EDGE,{"derivedFrom":sQuery(id+"F5.wireOp",EDGE,"E43.41.0.0")}),1.0]])]});
            var Q38;
            Q38=makeQuery(id+"F5.imprint","IMPRINT",FACE,{"disambiguationData":[TD([[makeQuery(id+"F5.imprint","IMPRINT",EDGE,{"derivedFrom":sQuery(id+"F5.wireOp",EDGE,"E43.42.0.0")}),1.0]])]});
            var Q39;
            Q39=makeQuery(id+"F5.imprint","IMPRINT",FACE,{"disambiguationData":[TD([[makeQuery(id+"F5.imprint","IMPRINT",EDGE,{"derivedFrom":sQuery(id+"F5.wireOp",EDGE,"E43.43.0.0")}),1.0]])]});
            var Q40;
            Q40=makeQuery(id+"F5.imprint","IMPRINT",FACE,{"disambiguationData":[TD([[makeQuery(id+"F5.imprint","IMPRINT",EDGE,{"derivedFrom":sQuery(id+"F5.wireOp",EDGE,"E43.44.0.0")}),1.0]])]});
            var Q41;
            Q41=makeQuery(id+"F5.imprint","IMPRINT",FACE,{"disambiguationData":[TD([[makeQuery(id+"F5.imprint","IMPRINT",EDGE,{"derivedFrom":sQuery(id+"F5.wireOp",EDGE,"E43.45.0.0")}),1.0]])]});
            var Q42;
            Q42=makeQuery(id+"F5.imprint","IMPRINT",FACE,{"disambiguationData":[TD([[makeQuery(id+"F5.imprint","IMPRINT",EDGE,{"derivedFrom":sQuery(id+"F5.wireOp",EDGE,"E43.46.0.0")}),1.0]])]});
            var Q43;
            Q43=makeQuery(id+"F5.imprint","IMPRINT",FACE,{"disambiguationData":[TD([[makeQuery(id+"F5.imprint","IMPRINT",EDGE,{"derivedFrom":sQuery(id+"F5.wireOp",EDGE,"E43.47.0.0")}),1.0]])]});
            var Q44;
            Q44=makeQuery(id+"F5.imprint","IMPRINT",FACE,{"disambiguationData":[TD([[makeQuery(id+"F5.imprint","IMPRINT",EDGE,{"derivedFrom":sQuery(id+"F5.wireOp",EDGE,"E43.48.0.0")}),1.0]])]});
            var Q45;
            Q45=makeQuery(id+"F5.imprint","IMPRINT",FACE,{"disambiguationData":[TD([[makeQuery(id+"F5.imprint","IMPRINT",EDGE,{"derivedFrom":sQuery(id+"F5.wireOp",EDGE,"E43.49.0.0")}),1.0]])]});
            var Q46;
            Q46=makeQuery(id+"F5.imprint","IMPRINT",FACE,{"disambiguationData":[TD([[makeQuery(id+"F5.imprint","IMPRINT",EDGE,{"derivedFrom":sQuery(id+"F5.wireOp",EDGE,"E43.50.0.0")}),1.0]])]});
            var Q47;
            Q47=makeQuery(id+"F5.imprint","IMPRINT",FACE,{"disambiguationData":[TD([[makeQuery(id+"F5.imprint","IMPRINT",EDGE,{"derivedFrom":sQuery(id+"F5.wireOp",EDGE,"E43.35.0.0")}),1.0]])]});
            var Q48;
            Q48=makeQuery(id+"F5.imprint","IMPRINT",FACE,{"disambiguationData":[TD([[makeQuery(id+"F5.imprint","IMPRINT",EDGE,{"derivedFrom":sQuery(id+"F5.wireOp",EDGE,"E43.36.0.0")}),1.0]])]});
            var Q49;
            Q49=makeQuery(id+"F5.imprint","IMPRINT",FACE,{"disambiguationData":[TD([[makeQuery(id+"F5.imprint","IMPRINT",EDGE,{"derivedFrom":sQuery(id+"F5.wireOp",EDGE,"E43.37.0.0")}),1.0]])]});
            var Q50;
            Q50=makeQuery(id+"F5.imprint","IMPRINT",FACE,{"disambiguationData":[TD([[makeQuery(id+"F5.imprint","IMPRINT",EDGE,{"derivedFrom":sQuery(id+"F5.wireOp",EDGE,"E43.38.0.0")}),1.0]])]});
            var Q51;
            Q51=makeQuery(id+"F5.imprint","IMPRINT",FACE,{"disambiguationData":[TD([[makeQuery(id+"F5.imprint","IMPRINT",EDGE,{"derivedFrom":sQuery(id+"F5.wireOp",EDGE,"E43.51.0.0")}),1.0]])]});
            var Q52;
            Q52=makeQuery(id+"F5.imprint","IMPRINT",FACE,{"disambiguationData":[TD([[makeQuery(id+"F5.imprint","IMPRINT",EDGE,{"derivedFrom":sQuery(id+"F5.wireOp",EDGE,"E43.52.0.0")}),1.0]])]});
            var Q53;
            Q53=makeQuery(id+"F5.imprint","IMPRINT",FACE,{"disambiguationData":[TD([[makeQuery(id+"F5.imprint","IMPRINT",EDGE,{"derivedFrom":sQuery(id+"F5.wireOp",EDGE,"E43.53.0.0")}),1.0]])]});
            var Q54;
            Q54=makeQuery(id+"F5.imprint","IMPRINT",FACE,{"disambiguationData":[TD([[makeQuery(id+"F5.imprint","IMPRINT",EDGE,{"derivedFrom":sQuery(id+"F5.wireOp",EDGE,"E43.54.0.0")}),1.0]])]});
            var Q55;
            Q55=makeQuery(id+"F5.imprint","IMPRINT",FACE,{"disambiguationData":[TD([[makeQuery(id+"F5.imprint","IMPRINT",EDGE,{"derivedFrom":sQuery(id+"F5.wireOp",EDGE,"E43.55.0.0")}),1.0]])]});
            var Q56;
            Q56=makeQuery(id+"F5.imprint","IMPRINT",FACE,{"disambiguationData":[TD([[makeQuery(id+"F5.imprint","IMPRINT",EDGE,{"derivedFrom":sQuery(id+"F5.wireOp",EDGE,"E43.56.0.0")}),1.0]])]});
            var Q57;
            Q57=makeQuery(id+"F5.imprint","IMPRINT",FACE,{"disambiguationData":[TD([[makeQuery(id+"F5.imprint","IMPRINT",EDGE,{"derivedFrom":sQuery(id+"F5.wireOp",EDGE,"E43.57.0.0")}),1.0]])]});
            var Q58;
            Q58=makeQuery(id+"F5.imprint","IMPRINT",FACE,{"disambiguationData":[TD([[makeQuery(id+"F5.imprint","IMPRINT",EDGE,{"derivedFrom":sQuery(id+"F5.wireOp",EDGE,"E43.58.0.0")}),1.0]])]});
            var Q59;
            Q59=makeQuery(id+"F5.imprint","IMPRINT",FACE,{"disambiguationData":[TD([[makeQuery(id+"F5.imprint","IMPRINT",EDGE,{"derivedFrom":sQuery(id+"F5.wireOp",EDGE,"E43.59.0.0")}),1.0]])]});
            var Q60;
            Q60=makeQuery(id+"F5.imprint","IMPRINT",FACE,{"disambiguationData":[TD([[makeQuery(id+"F5.imprint","IMPRINT",EDGE,{"derivedFrom":sQuery(id+"F5.wireOp",EDGE,"E43.57.0.0")}),1.0]])]});
            var Q61;
            Q61=makeQuery(id+"F5.imprint","IMPRINT",FACE,{"disambiguationData":[TD([[makeQuery(id+"F5.imprint","IMPRINT",EDGE,{"derivedFrom":sQuery(id+"F5.wireOp",EDGE,"E43.60.0.0")}),1.0]])]});
            var Q62;
            Q62=makeQuery(id+"F5.imprint","IMPRINT",FACE,{"disambiguationData":[TD([[makeQuery(id+"F5.imprint","IMPRINT",EDGE,{"derivedFrom":sQuery(id+"F5.wireOp",EDGE,"E43.61.0.0")}),1.0]])]});
            var Q63;
            Q63=makeQuery(id+"F5.imprint","IMPRINT",FACE,{"disambiguationData":[TD([[makeQuery(id+"F5.imprint","IMPRINT",EDGE,{"derivedFrom":sQuery(id+"F5.wireOp",EDGE,"E43.62.0.0")}),1.0]])]});
            var Q64;
            Q64=makeQuery(id+"F5.imprint","IMPRINT",FACE,{"disambiguationData":[TD([[makeQuery(id+"F5.imprint","IMPRINT",EDGE,{"derivedFrom":sQuery(id+"F5.wireOp",EDGE,"E43.63.0.0")}),1.0]])]});
            var Q65;
            Q65=makeQuery(id+"F5.imprint","IMPRINT",FACE,{"disambiguationData":[TD([[makeQuery(id+"F5.imprint","IMPRINT",EDGE,{"derivedFrom":sQuery(id+"F5.wireOp",EDGE,"E43.64.0.0")}),1.0]])]});
            var Q66;
            Q66=makeQuery(id+"F5.imprint","IMPRINT",FACE,{"disambiguationData":[TD([[makeQuery(id+"F5.imprint","IMPRINT",EDGE,{"derivedFrom":sQuery(id+"F5.wireOp",EDGE,"E43.65.0.0")}),1.0]])]});
            var Q67;
            Q67=makeQuery(id+"F5.imprint","IMPRINT",FACE,{"disambiguationData":[TD([[makeQuery(id+"F5.imprint","IMPRINT",EDGE,{"derivedFrom":sQuery(id+"F5.wireOp",EDGE,"E43.66.0.0")}),1.0]])]});
            var Q68;
            Q68=makeQuery(id+"F5.imprint","IMPRINT",FACE,{"disambiguationData":[TD([[makeQuery(id+"F5.imprint","IMPRINT",EDGE,{"derivedFrom":sQuery(id+"F5.wireOp",EDGE,"E43.67.0.0")}),1.0]])]});
            var Q69;
            Q69=makeQuery(id+"F5.imprint","IMPRINT",FACE,{"disambiguationData":[TD([[makeQuery(id+"F5.imprint","IMPRINT",EDGE,{"derivedFrom":sQuery(id+"F5.wireOp",EDGE,"E43.68.0.0")}),1.0]])]});
            var Q70;
            Q70=makeQuery(id+"F5.imprint","IMPRINT",FACE,{"disambiguationData":[TD([[makeQuery(id+"F5.imprint","IMPRINT",EDGE,{"derivedFrom":sQuery(id+"F5.wireOp",EDGE,"E43.69.0.0")}),1.0]])]});
            var Q71;
            Q71=makeQuery(id+"F5.imprint","IMPRINT",FACE,{"disambiguationData":[TD([[makeQuery(id+"F5.imprint","IMPRINT",EDGE,{"derivedFrom":sQuery(id+"F5.wireOp",EDGE,"E43.70.0.0")}),1.0]])]});
            var Q72;
            Q72=makeQuery(id+"F5.imprint","IMPRINT",FACE,{"disambiguationData":[TD([[makeQuery(id+"F5.imprint","IMPRINT",EDGE,{"derivedFrom":sQuery(id+"F5.wireOp",EDGE,"E43.71.0.0")}),1.0]])]});
            var Q73;
            Q73=makeQuery(id+"F5.imprint","IMPRINT",FACE,{"disambiguationData":[TD([[makeQuery(id+"F5.imprint","IMPRINT",EDGE,{"derivedFrom":sQuery(id+"F5.wireOp",EDGE,"E43.72.0.0")}),1.0]])]});
            var Q74;
            Q74=makeQuery(id+"F5.imprint","IMPRINT",FACE,{"disambiguationData":[TD([[makeQuery(id+"F5.imprint","IMPRINT",EDGE,{"derivedFrom":sQuery(id+"F5.wireOp",EDGE,"E43.73.0.0")}),1.0]])]});
            var Q75;
            Q75=makeQuery(id+"F5.imprint","IMPRINT",FACE,{"disambiguationData":[TD([[makeQuery(id+"F5.imprint","IMPRINT",EDGE,{"derivedFrom":sQuery(id+"F5.wireOp",EDGE,"E43.74.0.0")}),1.0]])]});
            var Q76;
            Q76=makeQuery(id+"F5.imprint","IMPRINT",FACE,{"disambiguationData":[TD([[makeQuery(id+"F5.imprint","IMPRINT",EDGE,{"derivedFrom":sQuery(id+"F5.wireOp",EDGE,"E43.75.0.0")}),1.0]])]});
            var Q77;
            Q77=makeQuery(id+"F5.imprint","IMPRINT",FACE,{"disambiguationData":[TD([[makeQuery(id+"F5.imprint","IMPRINT",EDGE,{"derivedFrom":sQuery(id+"F5.wireOp",EDGE,"E43.76.0.0")}),1.0]])]});
            var Q78;
            Q78=makeQuery(id+"F5.imprint","IMPRINT",FACE,{"disambiguationData":[TD([[makeQuery(id+"F5.imprint","IMPRINT",EDGE,{"derivedFrom":sQuery(id+"F5.wireOp",EDGE,"E43.77.0.0")}),1.0]])]});
            var Q79;
            Q79=makeQuery(id+"F5.imprint","IMPRINT",FACE,{"disambiguationData":[TD([[makeQuery(id+"F5.imprint","IMPRINT",EDGE,{"derivedFrom":sQuery(id+"F5.wireOp",EDGE,"E43.78.0.0")}),1.0]])]});
            var Q80;
            Q80=makeQuery(id+"F5.imprint","IMPRINT",FACE,{"disambiguationData":[TD([[makeQuery(id+"F5.imprint","IMPRINT",EDGE,{"derivedFrom":sQuery(id+"F5.wireOp",EDGE,"E43.79.0.0")}),1.0]])]});
            var Q81;
            Q81=makeQuery(id+"F5.imprint","IMPRINT",FACE,{"disambiguationData":[TD([[makeQuery(id+"F5.imprint","IMPRINT",EDGE,{"derivedFrom":sQuery(id+"F5.wireOp",EDGE,"E43.80.0.0")}),1.0]])]});
            var Q82;
            Q82=makeQuery(id+"F5.imprint","IMPRINT",FACE,{"disambiguationData":[TD([[makeQuery(id+"F5.imprint","IMPRINT",EDGE,{"derivedFrom":sQuery(id+"F5.wireOp",EDGE,"E43.81.0.0")}),1.0]])]});
            var Q83;
            Q83=makeQuery(id+"F5.imprint","IMPRINT",FACE,{"disambiguationData":[TD([[makeQuery(id+"F5.imprint","IMPRINT",EDGE,{"derivedFrom":sQuery(id+"F5.wireOp",EDGE,"E43.82.0.0")}),1.0]])]});
            var Q84;
            Q84=makeQuery(id+"F5.imprint","IMPRINT",FACE,{"disambiguationData":[TD([[makeQuery(id+"F5.imprint","IMPRINT",EDGE,{"derivedFrom":sQuery(id+"F5.wireOp",EDGE,"E43.83.0.0")}),1.0]])]});
            var Q85;
            Q85=makeQuery(id+"F5.imprint","IMPRINT",FACE,{"disambiguationData":[TD([[makeQuery(id+"F5.imprint","IMPRINT",EDGE,{"derivedFrom":sQuery(id+"F5.wireOp",EDGE,"E43.84.0.0")}),1.0]])]});
            var Q86;
            Q86=makeQuery(id+"F5.imprint","IMPRINT",FACE,{"disambiguationData":[TD([[makeQuery(id+"F5.imprint","IMPRINT",EDGE,{"derivedFrom":sQuery(id+"F5.wireOp",EDGE,"E43.85.0.0")}),1.0]])]});
            var Q87;
            Q87=makeQuery(id+"F5.imprint","IMPRINT",FACE,{"disambiguationData":[TD([[makeQuery(id+"F5.imprint","IMPRINT",EDGE,{"derivedFrom":sQuery(id+"F5.wireOp",EDGE,"E43.86.0.0")}),1.0]])]});
            var Q88;
            Q88=makeQuery(id+"F5.imprint","IMPRINT",FACE,{"disambiguationData":[TD([[makeQuery(id+"F5.imprint","IMPRINT",EDGE,{"derivedFrom":sQuery(id+"F5.wireOp",EDGE,"E43.87.0.0")}),1.0]])]});
            var Q89;
            Q89=makeQuery(id+"F5.imprint","IMPRINT",FACE,{"disambiguationData":[TD([[makeQuery(id+"F5.imprint","IMPRINT",EDGE,{"derivedFrom":sQuery(id+"F5.wireOp",EDGE,"E43.88.0.0")}),1.0]])]});
            var Q90;
            Q90=makeQuery(id+"F5.imprint","IMPRINT",FACE,{"disambiguationData":[TD([[makeQuery(id+"F5.imprint","IMPRINT",EDGE,{"derivedFrom":sQuery(id+"F5.wireOp",EDGE,"E43.89.0.0")}),1.0]])]});
            var Q91;
            Q91=makeQuery(id+"F5.imprint","IMPRINT",FACE,{"disambiguationData":[TD([[makeQuery(id+"F5.imprint","IMPRINT",EDGE,{"derivedFrom":sQuery(id+"F5.wireOp",EDGE,"E43.90.0.0")}),1.0]])]});
            var Q92;
            Q92=makeQuery(id+"F5.imprint","IMPRINT",FACE,{"disambiguationData":[TD([[makeQuery(id+"F5.imprint","IMPRINT",EDGE,{"derivedFrom":sQuery(id+"F5.wireOp",EDGE,"E43.91.0.0")}),1.0]])]});
            var Q93;
            Q93=makeQuery(id+"F5.imprint","IMPRINT",FACE,{"disambiguationData":[TD([[makeQuery(id+"F5.imprint","IMPRINT",EDGE,{"derivedFrom":sQuery(id+"F5.wireOp",EDGE,"E43.92.0.0")}),1.0]])]});
            var Q94;
            Q94=makeQuery(id+"F5.imprint","IMPRINT",FACE,{"disambiguationData":[TD([[makeQuery(id+"F5.imprint","IMPRINT",EDGE,{"derivedFrom":sQuery(id+"F5.wireOp",EDGE,"E43.93.0.0")}),1.0]])]});
            var Q95;
            Q95=makeQuery(id+"F5.imprint","IMPRINT",FACE,{"disambiguationData":[TD([[makeQuery(id+"F5.imprint","IMPRINT",EDGE,{"derivedFrom":sQuery(id+"F5.wireOp",EDGE,"E43.94.0.0")}),1.0]])]});
            var Q96;
            Q96=makeQuery(id+"F5.imprint","IMPRINT",FACE,{"disambiguationData":[TD([[makeQuery(id+"F5.imprint","IMPRINT",EDGE,{"derivedFrom":sQuery(id+"F5.wireOp",EDGE,"E44.0.95.0")}),1.0]])]});
            var Q97;
            Q97=makeQuery(id+"F5.imprint","IMPRINT",FACE,{"disambiguationData":[TD([[makeQuery(id+"F5.imprint","IMPRINT",EDGE,{"derivedFrom":sQuery(id+"F5.wireOp",EDGE,"E44.0.96.0")}),1.0]])]});
            var Q98;
            Q98=makeQuery(id+"F5.imprint","IMPRINT",FACE,{"disambiguationData":[TD([[makeQuery(id+"F5.imprint","IMPRINT",EDGE,{"derivedFrom":sQuery(id+"F5.wireOp",EDGE,"E44.0.97.0")}),1.0]])]});
            var Q99;
            Q99=makeQuery(id+"F5.imprint","IMPRINT",FACE,{"disambiguationData":[TD([[makeQuery(id+"F5.imprint","IMPRINT",EDGE,{"derivedFrom":sQuery(id+"F5.wireOp",EDGE,"E44.0.98.0")}),1.0]])]});
            var Q100;
            Q100=makeQuery(id+"F5.imprint","IMPRINT",FACE,{"disambiguationData":[TD([[makeQuery(id+"F5.imprint","IMPRINT",EDGE,{"derivedFrom":sQuery(id+"F5.wireOp",EDGE,"E44.0.99.0")}),1.0]])]});
            extrude(context, id + "F6", {"entities" : qUnion([Q0, Q1, Q2, Q3, Q4, Q5, Q6, Q7, Q8, Q9, Q10, Q11, Q12, Q13, Q14, Q15, Q16, Q17, Q18, Q19, Q20, Q21, Q22, Q23, Q24, Q25, Q26, Q27, Q28, Q29, Q30, Q31, Q32, Q33, Q34, Q35, Q36, Q37, Q38, Q39, Q40, Q41, Q42, Q43, Q44, Q45, Q46, Q47, Q48, Q49, Q50, Q51, Q52, Q53, Q54, Q55, Q56, Q57, Q58, Q59, Q60, Q61, Q62, Q63, Q64, Q65, Q66, Q67, Q68, Q69, Q70, Q71, Q72, Q73, Q74, Q75, Q76, Q77, Q78, Q79, Q80, Q81, Q82, Q83, Q84, Q85, Q86, Q87, Q88, Q89, Q90, Q91, Q92, Q93, Q94, Q95, Q96, Q97, Q98, Q99, Q100]), "operationType" : NewBodyOperationType.ADD, "oppositeDirection" : true, "depth" : 50.8 * mm});
        }
    });
